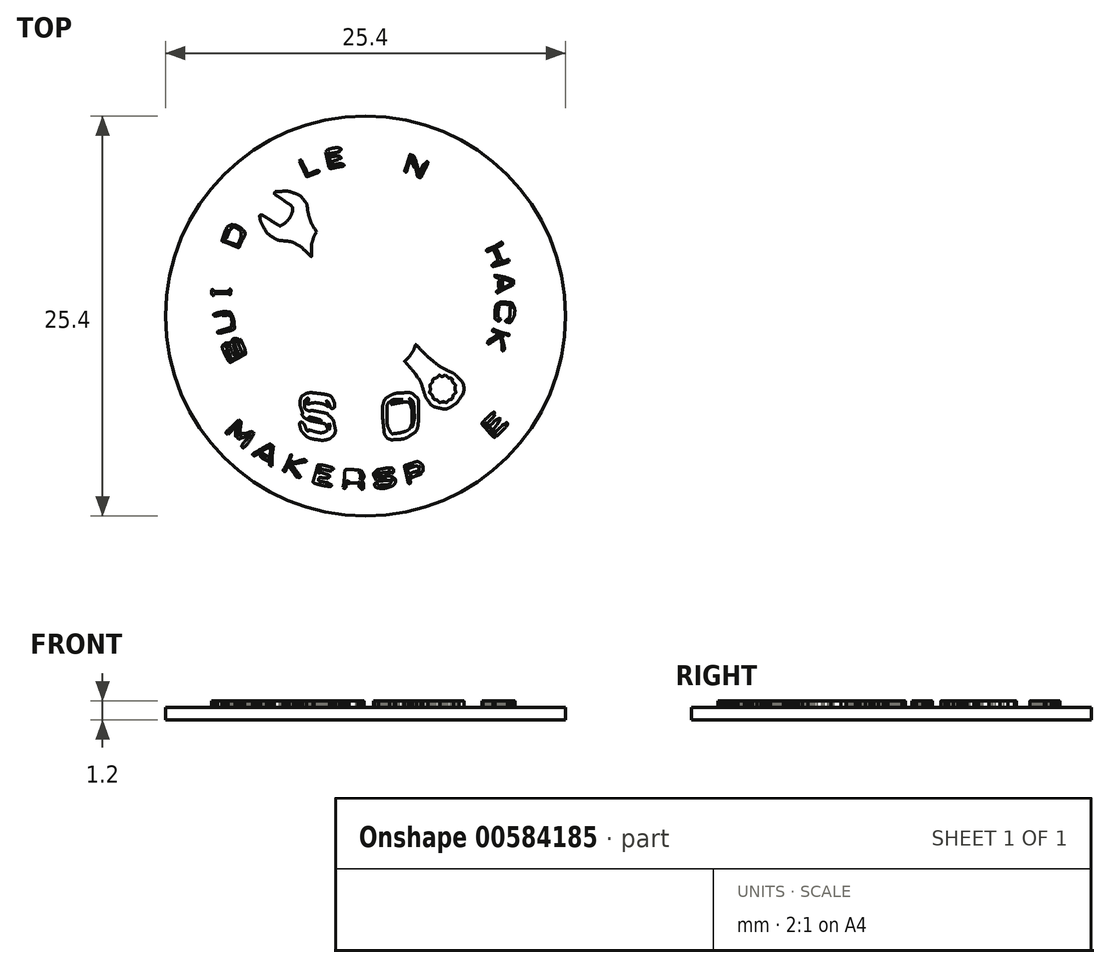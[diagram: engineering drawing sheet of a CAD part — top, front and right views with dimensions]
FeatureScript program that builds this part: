
annotation { "Feature Type Name" : "Feature", "Feature Type Description" : "" }
export const myFeature = defineFeature(function(context is Context, id is Id, definition is map)
    precondition{}
    {
        {
            var Q0;
            Q0=qCreatedBy(makeId("Top.planeOp"),FACE);
            var sketch = newSketch(context, id + "F0", { "sketchPlane" : qUnion([Q0])});
            skCircle(sketch, "E0", {"center": v(0, 0) * mm, "radius": 12.7 * mm});
            skSolve(sketch);
        }
        {
            var Q0;
            Q0=makeQuery(id+"F0.imprint","IMPRINT",FACE,{"disambiguationData":[TD([[makeQuery(id+"F0.imprint","IMPRINT",EDGE,{"derivedFrom":sQuery(id+"F0.wireOp",EDGE,"E0")}),1.0]])]});
            extrude(context, id + "F1", {"entities" : qUnion([Q0]), "depth" : .8 * mm, "offsetDistance" : 25.4 * mm});
        }
        {
            var Q0;
            Q0=makeQuery(id+"F1.opExtrude","CAP_FACE",FACE,{"disambiguationData":[OSD([sQuery(id+"F0.wireOp",EDGE,"E0")])],"isStart":false});
            var sketch = newSketch(context, id + "F2", { "sketchPlane" : qUnion([Q0])});
            skFitSpline(sketch, "E1", {"points": [v(-0.28, -10.95) * mm, v(-0.3, -10.92) * mm, v(-0.3, -10.87) * mm, v(-0.3, -10.8) * mm]});
            skFitSpline(sketch, "E2", {"points": [v(-0.3, -10.8) * mm, v(-0.28, -10.68) * mm, v(-0.3, -10.63) * mm, v(-0.35, -10.58) * mm]});
            skFitSpline(sketch, "E3", {"points": [v(-0.35, -10.58) * mm, v(-0.4, -10.53) * mm, v(-0.42, -10.54) * mm, v(-0.38, -10.6) * mm]});
            skFitSpline(sketch, "E4", {"points": [v(-0.38, -10.6) * mm, v(-0.36, -10.63) * mm, v(-0.35, -10.67) * mm, v(-0.35, -10.76) * mm]});
            skFitSpline(sketch, "E5", {"points": [v(-0.35, -10.76) * mm, v(-0.35, -10.82) * mm, v(-0.36, -10.87) * mm, v(-0.36, -10.87) * mm]});
            skFitSpline(sketch, "E6", {"points": [v(-0.36, -10.87) * mm, v(-0.38, -10.88) * mm, v(-0.41, -10.8) * mm, v(-0.41, -10.76) * mm]});
            skFitSpline(sketch, "E7", {"points": [v(-0.41, -10.76) * mm, v(-0.41, -10.7) * mm, v(-0.44, -10.66) * mm, v(-0.49, -10.64) * mm]});
            skFitSpline(sketch, "E8", {"points": [v(-0.49, -10.64) * mm, v(-0.54, -10.62) * mm, v(-0.96, -10.61) * mm, v(-1.05, -10.63) * mm]});
            skFitSpline(sketch, "E9", {"points": [v(-1.05, -10.63) * mm, v(-1.12, -10.64) * mm, v(-1.13, -10.62) * mm, v(-1.08, -10.57) * mm]});
            skFitSpline(sketch, "E10", {"points": [v(-1.08, -10.57) * mm, v(-1.04, -10.53) * mm, v(-1.04, -10.5) * mm, v(-1.08, -10.5) * mm]});
            skFitSpline(sketch, "E11", {"points": [v(-1.08, -10.5) * mm, v(-1.2, -10.47) * mm, v(-1.22, -10.5) * mm, v(-1.23, -10.7) * mm]});
            skFitSpline(sketch, "E12", {"points": [v(-1.23, -10.7) * mm, v(-1.24, -10.84) * mm, v(-1.24, -10.87) * mm, v(-1.27, -10.9) * mm]});
            skFitSpline(sketch, "E13", {"points": [v(-1.27, -10.9) * mm, v(-1.31, -10.96) * mm, v(-1.35, -10.97) * mm, v(-1.4, -10.92) * mm]});
            skLineSegment(sketch, "E14", {"start": v(-1.4, -10.92) * mm, "end": v(-1.43, -10.89) * mm});
            skLineSegment(sketch, "E15", {"start": v(-1.43, -10.89) * mm, "end": v(-1.4, -10.75) * mm});
            skFitSpline(sketch, "E16", {"points": [v(-1.4, -10.75) * mm, v(-1.38, -10.67) * mm, v(-1.36, -10.44) * mm, v(-1.35, -10.25) * mm]});
            skFitSpline(sketch, "E17", {"points": [v(-1.35, -10.25) * mm, v(-1.32, -9.83) * mm, v(-1.31, -9.8) * mm, v(-1.28, -9.77) * mm]});
            skFitSpline(sketch, "E18", {"points": [v(-1.28, -9.77) * mm, v(-1.24, -9.75) * mm, v(-0.81, -9.76) * mm, v(-0.62, -9.77) * mm]});
            skFitSpline(sketch, "E19", {"points": [v(-0.62, -9.77) * mm, v(-0.36, -9.8) * mm, v(-0.23, -9.86) * mm, v(-0.17, -10) * mm]});
            skFitSpline(sketch, "E20", {"points": [v(-0.17, -10) * mm, v(-0.12, -10.1) * mm, v(-0.1, -10.25) * mm, v(-0.15, -10.33) * mm]});
            skFitSpline(sketch, "E21", {"points": [v(-0.15, -10.33) * mm, v(-0.17, -10.36) * mm, v(-0.2, -10.4) * mm, v(-0.2, -10.4) * mm]});
            skFitSpline(sketch, "E22", {"points": [v(-0.2, -10.4) * mm, v(-0.22, -10.43) * mm, v(-0.22, -10.44) * mm, v(-0.18, -10.52) * mm]});
            skFitSpline(sketch, "E23", {"points": [v(-0.18, -10.52) * mm, v(-0.13, -10.61) * mm, v(-0.13, -10.62) * mm, v(-0.13, -10.8) * mm]});
            skFitSpline(sketch, "E24", {"points": [v(-0.13, -10.8) * mm, v(-0.14, -10.9) * mm, v(-0.14, -10.98) * mm, v(-0.14, -10.98) * mm]});
            skFitSpline(sketch, "E25", {"points": [v(-0.14, -10.98) * mm, v(-0.14, -10.98) * mm, v(-0.17, -11) * mm, v(-0.2, -11) * mm]});
            skFitSpline(sketch, "E26", {"points": [v(-0.2, -11) * mm, v(-0.26, -11) * mm, v(-0.26, -11) * mm, v(-0.28, -10.95) * mm]});
            skLineSegment(sketch, "E27", {"start": v(-0.28, -10.95) * mm, "end": v(-0.28, -10.95) * mm});
            skFitSpline(sketch, "E28", {"points": [v(-1.09, -10.33) * mm, v(-1.02, -10.3) * mm, v(-0.88, -10.3) * mm, v(-0.71, -10.33) * mm]});
            skFitSpline(sketch, "E29", {"points": [v(-0.71, -10.33) * mm, v(-0.45, -10.38) * mm, v(-0.4, -10.36) * mm, v(-0.4, -10.2) * mm]});
            skLineSegment(sketch, "E30", {"start": v(-0.4, -10.2) * mm, "end": v(-0.4, -10.1) * mm});
            skLineSegment(sketch, "E31", {"start": v(-0.4, -10.1) * mm, "end": v(-0.47, -10.07) * mm});
            skFitSpline(sketch, "E32", {"points": [v(-0.47, -10.07) * mm, v(-0.53, -10.04) * mm, v(-0.57, -10.04) * mm, v(-0.8, -10.03) * mm]});
            skLineSegment(sketch, "E33", {"start": v(-0.8, -10.03) * mm, "end": v(-1.08, -10.03) * mm});
            skLineSegment(sketch, "E34", {"start": v(-1.08, -10.03) * mm, "end": v(-1.08, -9.97) * mm});
            skFitSpline(sketch, "E35", {"points": [v(-1.08, -9.97) * mm, v(-1.08, -9.94) * mm, v(-1.1, -9.92) * mm, v(-1.1, -9.92) * mm]});
            skFitSpline(sketch, "E36", {"points": [v(-1.1, -9.92) * mm, v(-1.13, -9.92) * mm, v(-1.14, -9.95) * mm, v(-1.16, -10.05) * mm]});
            skFitSpline(sketch, "E37", {"points": [v(-1.16, -10.05) * mm, v(-1.2, -10.3) * mm, v(-1.2, -10.3) * mm, v(-1.18, -10.33) * mm]});
            skFitSpline(sketch, "E38", {"points": [v(-1.18, -10.33) * mm, v(-1.15, -10.36) * mm, v(-1.16, -10.36) * mm, v(-1.09, -10.33) * mm]});
            skLineSegment(sketch, "E39", {"start": v(-1.09, -10.33) * mm, "end": v(-1.09, -10.33) * mm});
            skFitSpline(sketch, "E40", {"points": [v(-0.3, -10.28) * mm, v(-0.27, -10.2) * mm, v(-0.3, -10.06) * mm, v(-0.34, -10) * mm]});
            skFitSpline(sketch, "E41", {"points": [v(-0.34, -10) * mm, v(-0.4, -9.94) * mm, v(-0.42, -9.94) * mm, v(-0.38, -10) * mm]});
            skFitSpline(sketch, "E42", {"points": [v(-0.38, -10) * mm, v(-0.32, -10.08) * mm, v(-0.31, -10.23) * mm, v(-0.35, -10.3) * mm]});
            skFitSpline(sketch, "E43", {"points": [v(-0.35, -10.3) * mm, v(-0.36, -10.33) * mm, v(-0.36, -10.34) * mm, v(-0.35, -10.34) * mm]});
            skFitSpline(sketch, "E44", {"points": [v(-0.35, -10.34) * mm, v(-0.34, -10.34) * mm, v(-0.32, -10.31) * mm, v(-0.3, -10.28) * mm]});
            skFitSpline(sketch, "E45", {"points": [v(1.08, -11) * mm, v(1.08, -11) * mm, v(1.15, -10.99) * mm, v(1.22, -10.98) * mm]});
            skFitSpline(sketch, "E46", {"points": [v(1.22, -10.98) * mm, v(1.31, -10.98) * mm, v(1.34, -10.98) * mm, v(1.3, -10.99) * mm]});
            skFitSpline(sketch, "E47", {"points": [v(1.3, -10.99) * mm, v(1.24, -11) * mm, v(1.07, -11) * mm, v(1.08, -11) * mm]});
            skFitSpline(sketch, "E48", {"points": [v(0.84, -10.93) * mm, v(0.7, -10.9) * mm, v(0.6, -10.82) * mm, v(0.58, -10.72) * mm]});
            skFitSpline(sketch, "E49", {"points": [v(0.58, -10.72) * mm, v(0.57, -10.67) * mm, v(0.6, -10.63) * mm, v(0.66, -10.62) * mm]});
            skFitSpline(sketch, "E50", {"points": [v(0.66, -10.62) * mm, v(0.7, -10.6) * mm, v(0.7, -10.61) * mm, v(0.78, -10.7) * mm]});
            skFitSpline(sketch, "E51", {"points": [v(0.78, -10.7) * mm, v(0.86, -10.78) * mm, v(0.88, -10.8) * mm, v(0.93, -10.75) * mm]});
            skFitSpline(sketch, "E52", {"points": [v(0.93, -10.75) * mm, v(0.95, -10.74) * mm, v(1, -10.73) * mm, v(1.08, -10.73) * mm]});
            skFitSpline(sketch, "E53", {"points": [v(1.08, -10.73) * mm, v(1.3, -10.73) * mm, v(1.57, -10.65) * mm, v(1.6, -10.58) * mm]});
            skFitSpline(sketch, "E54", {"points": [v(1.6, -10.58) * mm, v(1.63, -10.55) * mm, v(1.6, -10.49) * mm, v(1.55, -10.46) * mm]});
            skFitSpline(sketch, "E55", {"points": [v(1.55, -10.46) * mm, v(1.5, -10.44) * mm, v(1.5, -10.44) * mm, v(1, -10.47) * mm]});
            skFitSpline(sketch, "E56", {"points": [v(1, -10.47) * mm, v(0.83, -10.48) * mm, v(0.76, -10.46) * mm, v(0.67, -10.41) * mm]});
            skFitSpline(sketch, "E57", {"points": [v(0.67, -10.41) * mm, v(0.63, -10.39) * mm, v(0.62, -10.38) * mm, v(0.64, -10.37) * mm]});
            skFitSpline(sketch, "E58", {"points": [v(0.64, -10.37) * mm, v(0.66, -10.35) * mm, v(0.66, -10.35) * mm, v(0.64, -10.32) * mm]});
            skFitSpline(sketch, "E59", {"points": [v(0.64, -10.32) * mm, v(0.52, -10.13) * mm, v(0.52, -10) * mm, v(0.63, -9.86) * mm]});
            skFitSpline(sketch, "E60", {"points": [v(0.63, -9.86) * mm, v(0.7, -9.8) * mm, v(0.79, -9.76) * mm, v(0.99, -9.72) * mm]});
            skFitSpline(sketch, "E61", {"points": [v(0.99, -9.72) * mm, v(1.47, -9.64) * mm, v(1.75, -9.7) * mm, v(1.76, -9.89) * mm]});
            skFitSpline(sketch, "E62", {"points": [v(1.76, -9.89) * mm, v(1.77, -9.92) * mm, v(1.76, -9.94) * mm, v(1.72, -9.96) * mm]});
            skLineSegment(sketch, "E63", {"start": v(1.72, -9.96) * mm, "end": v(1.67, -10) * mm});
            skLineSegment(sketch, "E64", {"start": v(1.67, -10) * mm, "end": v(1.6, -9.91) * mm});
            skFitSpline(sketch, "E65", {"points": [v(1.6, -9.91) * mm, v(1.56, -9.87) * mm, v(1.51, -9.83) * mm, v(1.5, -9.83) * mm]});
            skFitSpline(sketch, "E66", {"points": [v(1.5, -9.83) * mm, v(1.47, -9.83) * mm, v(1.47, -9.84) * mm, v(1.5, -9.88) * mm]});
            skFitSpline(sketch, "E67", {"points": [v(1.5, -9.88) * mm, v(1.51, -9.9) * mm, v(1.53, -9.93) * mm, v(1.54, -9.93) * mm]});
            skFitSpline(sketch, "E68", {"points": [v(1.54, -9.93) * mm, v(1.54, -9.94) * mm, v(1.47, -9.95) * mm, v(1.32, -9.95) * mm]});
            skFitSpline(sketch, "E69", {"points": [v(1.32, -9.95) * mm, v(1.11, -9.95) * mm, v(1.1, -9.95) * mm, v(0.96, -10) * mm]});
            skFitSpline(sketch, "E70", {"points": [v(0.96, -10) * mm, v(0.88, -10.03) * mm, v(0.81, -10.05) * mm, v(0.81, -10.05) * mm]});
            skFitSpline(sketch, "E71", {"points": [v(0.81, -10.05) * mm, v(0.8, -10.05) * mm, v(0.81, -10.02) * mm, v(0.82, -9.99) * mm]});
            skFitSpline(sketch, "E72", {"points": [v(0.82, -9.99) * mm, v(0.84, -9.89) * mm, v(0.81, -9.87) * mm, v(0.74, -9.94) * mm]});
            skFitSpline(sketch, "E73", {"points": [v(0.74, -9.94) * mm, v(0.69, -10) * mm, v(0.68, -10.07) * mm, v(0.72, -10.15) * mm]});
            skFitSpline(sketch, "E74", {"points": [v(0.72, -10.15) * mm, v(0.76, -10.22) * mm, v(0.84, -10.25) * mm, v(0.91, -10.22) * mm]});
            skFitSpline(sketch, "E75", {"points": [v(0.91, -10.22) * mm, v(0.94, -10.2) * mm, v(1.09, -10.19) * mm, v(1.24, -10.17) * mm]});
            skLineSegment(sketch, "E76", {"start": v(1.24, -10.17) * mm, "end": v(1.51, -10.15) * mm});
            skLineSegment(sketch, "E77", {"start": v(1.51, -10.15) * mm, "end": v(1.62, -10.2) * mm});
            skFitSpline(sketch, "E78", {"points": [v(1.62, -10.2) * mm, v(1.68, -10.21) * mm, v(1.75, -10.25) * mm, v(1.78, -10.27) * mm]});
            skFitSpline(sketch, "E79", {"points": [v(1.78, -10.27) * mm, v(1.87, -10.35) * mm, v(1.91, -10.53) * mm, v(1.85, -10.64) * mm]});
            skFitSpline(sketch, "E80", {"points": [v(1.85, -10.64) * mm, v(1.81, -10.71) * mm, v(1.66, -10.81) * mm, v(1.52, -10.86) * mm]});
            skFitSpline(sketch, "E81", {"points": [v(1.52, -10.86) * mm, v(1.3, -10.93) * mm, v(1, -10.96) * mm, v(0.84, -10.93) * mm]});
            skFitSpline(sketch, "E82", {"points": [v(1.68, -10.4) * mm, v(1.64, -10.37) * mm, v(1.63, -10.38) * mm, v(1.66, -10.43) * mm]});
            skFitSpline(sketch, "E83", {"points": [v(1.66, -10.43) * mm, v(1.68, -10.45) * mm, v(1.7, -10.46) * mm, v(1.7, -10.44) * mm]});
            skFitSpline(sketch, "E84", {"points": [v(1.7, -10.44) * mm, v(1.7, -10.43) * mm, v(1.7, -10.41) * mm, v(1.68, -10.4) * mm]});
            skFitSpline(sketch, "E85", {"points": [v(1.29, -10.38) * mm, v(1.33, -10.37) * mm, v(1.29, -10.37) * mm, v(1.16, -10.38) * mm]});
            skFitSpline(sketch, "E86", {"points": [v(1.16, -10.38) * mm, v(1.07, -10.38) * mm, v(0.97, -10.39) * mm, v(0.94, -10.4) * mm]});
            skFitSpline(sketch, "E87", {"points": [v(0.94, -10.4) * mm, v(0.89, -10.42) * mm, v(1.22, -10.4) * mm, v(1.29, -10.38) * mm]});
            skFitSpline(sketch, "E88", {"points": [v(-2.66, -10.83) * mm, v(-2.82, -10.8) * mm, v(-2.98, -10.76) * mm, v(-2.97, -10.75) * mm]});
            skFitSpline(sketch, "E89", {"points": [v(-2.97, -10.75) * mm, v(-2.97, -10.75) * mm, v(-2.88, -10.77) * mm, v(-2.76, -10.8) * mm]});
            skFitSpline(sketch, "E90", {"points": [v(-2.76, -10.8) * mm, v(-2.65, -10.81) * mm, v(-2.58, -10.83) * mm, v(-2.6, -10.83) * mm]});
            skFitSpline(sketch, "E91", {"points": [v(-2.6, -10.83) * mm, v(-2.62, -10.83) * mm, v(-2.65, -10.83) * mm, v(-2.66, -10.83) * mm]});
            skFitSpline(sketch, "E92", {"points": [v(-2.29, -10.83) * mm, v(-2.48, -10.8) * mm, v(-3.25, -10.63) * mm, v(-3.29, -10.6) * mm]});
            skFitSpline(sketch, "E93", {"points": [v(-3.29, -10.6) * mm, v(-3.33, -10.56) * mm, v(-3.31, -10.43) * mm, v(-3.21, -10.1) * mm]});
            skFitSpline(sketch, "E94", {"points": [v(-3.21, -10.1) * mm, v(-3.17, -9.95) * mm, v(-3.1, -9.75) * mm, v(-3.09, -9.66) * mm]});
            skFitSpline(sketch, "E95", {"points": [v(-3.09, -9.66) * mm, v(-3.04, -9.47) * mm, v(-3.02, -9.46) * mm, v(-2.9, -9.46) * mm]});
            skFitSpline(sketch, "E96", {"points": [v(-2.9, -9.46) * mm, v(-2.84, -9.46) * mm, v(-2.48, -9.53) * mm, v(-2.3, -9.58) * mm]});
            skFitSpline(sketch, "E97", {"points": [v(-2.3, -9.58) * mm, v(-2.17, -9.61) * mm, v(-2.04, -9.68) * mm, v(-2.04, -9.7) * mm]});
            skFitSpline(sketch, "E98", {"points": [v(-2.04, -9.7) * mm, v(-2.04, -9.74) * mm, v(-2.07, -9.76) * mm, v(-2.13, -9.76) * mm]});
            skFitSpline(sketch, "E99", {"points": [v(-2.13, -9.76) * mm, v(-2.19, -9.76) * mm, v(-2.19, -9.76) * mm, v(-2.18, -9.8) * mm]});
            skFitSpline(sketch, "E100", {"points": [v(-2.18, -9.8) * mm, v(-2.17, -9.83) * mm, v(-2.17, -9.83) * mm, v(-2.23, -9.83) * mm]});
            skFitSpline(sketch, "E101", {"points": [v(-2.23, -9.83) * mm, v(-2.26, -9.83) * mm, v(-2.4, -9.81) * mm, v(-2.55, -9.78) * mm]});
            skLineSegment(sketch, "E102", {"start": v(-2.55, -9.78) * mm, "end": v(-2.82, -9.73) * mm});
            skLineSegment(sketch, "E103", {"start": v(-2.82, -9.73) * mm, "end": v(-2.84, -9.76) * mm});
            skFitSpline(sketch, "E104", {"points": [v(-2.84, -9.76) * mm, v(-2.86, -9.78) * mm, v(-2.87, -9.81) * mm, v(-2.87, -9.84) * mm]});
            skFitSpline(sketch, "E105", {"points": [v(-2.87, -9.84) * mm, v(-2.87, -9.86) * mm, v(-2.88, -9.88) * mm, v(-2.89, -9.89) * mm]});
            skFitSpline(sketch, "E106", {"points": [v(-2.89, -9.89) * mm, v(-2.9, -9.9) * mm, v(-2.9, -9.8) * mm, v(-2.86, -9.7) * mm]});
            skFitSpline(sketch, "E107", {"points": [v(-2.86, -9.7) * mm, v(-2.85, -9.66) * mm, v(-2.84, -9.63) * mm, v(-2.84, -9.63) * mm]});
            skFitSpline(sketch, "E108", {"points": [v(-2.84, -9.63) * mm, v(-2.85, -9.62) * mm, v(-2.86, -9.63) * mm, v(-2.88, -9.65) * mm]});
            skFitSpline(sketch, "E109", {"points": [v(-2.88, -9.65) * mm, v(-2.92, -9.68) * mm, v(-2.97, -9.76) * mm, v(-3, -9.86) * mm]});
            skFitSpline(sketch, "E110", {"points": [v(-3, -9.86) * mm, v(-3, -9.92) * mm, v(-3, -9.93) * mm, v(-2.98, -9.95) * mm]});
            skFitSpline(sketch, "E111", {"points": [v(-2.98, -9.95) * mm, v(-2.94, -9.98) * mm, v(-2.88, -9.98) * mm, v(-2.88, -9.95) * mm]});
            skFitSpline(sketch, "E112", {"points": [v(-2.88, -9.95) * mm, v(-2.88, -9.94) * mm, v(-2.88, -9.93) * mm, v(-2.87, -9.93) * mm]});
            skFitSpline(sketch, "E113", {"points": [v(-2.87, -9.93) * mm, v(-2.87, -9.93) * mm, v(-2.76, -9.96) * mm, v(-2.64, -10) * mm]});
            skFitSpline(sketch, "E114", {"points": [v(-2.64, -10) * mm, v(-2.4, -10.08) * mm, v(-2.3, -10.13) * mm, v(-2.3, -10.2) * mm]});
            skFitSpline(sketch, "E115", {"points": [v(-2.3, -10.2) * mm, v(-2.3, -10.25) * mm, v(-2.3, -10.25) * mm, v(-2.37, -10.26) * mm]});
            skFitSpline(sketch, "E116", {"points": [v(-2.37, -10.26) * mm, v(-2.44, -10.26) * mm, v(-2.44, -10.26) * mm, v(-2.43, -10.28) * mm]});
            skFitSpline(sketch, "E117", {"points": [v(-2.43, -10.28) * mm, v(-2.4, -10.3) * mm, v(-2.41, -10.3) * mm, v(-2.72, -10.27) * mm]});
            skFitSpline(sketch, "E118", {"points": [v(-2.72, -10.27) * mm, v(-2.92, -10.25) * mm, v(-2.92, -10.25) * mm, v(-2.96, -10.31) * mm]});
            skFitSpline(sketch, "E119", {"points": [v(-2.96, -10.31) * mm, v(-2.98, -10.34) * mm, v(-3, -10.38) * mm, v(-2.99, -10.4) * mm]});
            skFitSpline(sketch, "E120", {"points": [v(-2.99, -10.4) * mm, v(-2.98, -10.46) * mm, v(-2.9, -10.5) * mm, v(-2.59, -10.56) * mm]});
            skFitSpline(sketch, "E121", {"points": [v(-2.59, -10.56) * mm, v(-2.4, -10.6) * mm, v(-2.35, -10.6) * mm, v(-2.38, -10.62) * mm]});
            skFitSpline(sketch, "E122", {"points": [v(-2.38, -10.62) * mm, v(-2.41, -10.63) * mm, v(-2.4, -10.64) * mm, v(-2.33, -10.66) * mm]});
            skFitSpline(sketch, "E123", {"points": [v(-2.33, -10.66) * mm, v(-2.22, -10.7) * mm, v(-2.17, -10.73) * mm, v(-2.17, -10.78) * mm]});
            skFitSpline(sketch, "E124", {"points": [v(-2.17, -10.78) * mm, v(-2.18, -10.82) * mm, v(-2.22, -10.83) * mm, v(-2.29, -10.83) * mm]});
            skFitSpline(sketch, "E125", {"points": [v(-3, -10.33) * mm, v(-2.95, -10.14) * mm, v(-2.95, -10.14) * mm, v(-3, -10.14) * mm]});
            skFitSpline(sketch, "E126", {"points": [v(-3, -10.14) * mm, v(-3.02, -10.14) * mm, v(-3.04, -10.15) * mm, v(-3.05, -10.16) * mm]});
            skFitSpline(sketch, "E127", {"points": [v(-3.05, -10.16) * mm, v(-3.07, -10.19) * mm, v(-3.11, -10.34) * mm, v(-3.11, -10.4) * mm]});
            skFitSpline(sketch, "E128", {"points": [v(-3.11, -10.4) * mm, v(-3.11, -10.45) * mm, v(-3.07, -10.5) * mm, v(-3.05, -10.5) * mm]});
            skFitSpline(sketch, "E129", {"points": [v(-3.05, -10.5) * mm, v(-3.04, -10.5) * mm, v(-3.02, -10.42) * mm, v(-3, -10.33) * mm]});
            skFitSpline(sketch, "E130", {"points": [v(2.77, -10.64) * mm, v(2.75, -10.64) * mm, v(2.73, -10.63) * mm, v(2.73, -10.63) * mm]});
            skFitSpline(sketch, "E131", {"points": [v(2.73, -10.63) * mm, v(2.72, -10.62) * mm, v(2.66, -10.38) * mm, v(2.6, -10.1) * mm]});
            skFitSpline(sketch, "E132", {"points": [v(2.6, -10.1) * mm, v(2.53, -9.82) * mm, v(2.47, -9.57) * mm, v(2.47, -9.56) * mm]});
            skFitSpline(sketch, "E133", {"points": [v(2.47, -9.56) * mm, v(2.46, -9.52) * mm, v(2.58, -9.46) * mm, v(2.84, -9.38) * mm]});
            skFitSpline(sketch, "E134", {"points": [v(2.84, -9.38) * mm, v(3.17, -9.27) * mm, v(3.34, -9.25) * mm, v(3.46, -9.32) * mm]});
            skFitSpline(sketch, "E135", {"points": [v(3.46, -9.32) * mm, v(3.56, -9.38) * mm, v(3.66, -9.6) * mm, v(3.66, -9.76) * mm]});
            skFitSpline(sketch, "E136", {"points": [v(3.66, -9.76) * mm, v(3.66, -9.85) * mm, v(3.63, -9.88) * mm, v(3.49, -9.94) * mm]});
            skFitSpline(sketch, "E137", {"points": [v(3.49, -9.94) * mm, v(3.32, -10) * mm, v(3.24, -10.05) * mm, v(3.26, -10.07) * mm]});
            skFitSpline(sketch, "E138", {"points": [v(3.26, -10.07) * mm, v(3.27, -10.08) * mm, v(3.3, -10.07) * mm, v(3.4, -10.05) * mm]});
            skFitSpline(sketch, "E139", {"points": [v(3.4, -10.05) * mm, v(3.46, -10.03) * mm, v(3.51, -10.02) * mm, v(3.52, -10.02) * mm]});
            skFitSpline(sketch, "E140", {"points": [v(3.52, -10.02) * mm, v(3.53, -10.04) * mm, v(3.41, -10.08) * mm, v(3.23, -10.15) * mm]});
            skFitSpline(sketch, "E141", {"points": [v(3.23, -10.15) * mm, v(3.13, -10.19) * mm, v(3.02, -10.23) * mm, v(3, -10.25) * mm]});
            skFitSpline(sketch, "E142", {"points": [v(3, -10.25) * mm, v(2.93, -10.28) * mm, v(2.9, -10.27) * mm, v(2.92, -10.2) * mm]});
            skFitSpline(sketch, "E143", {"points": [v(2.92, -10.2) * mm, v(2.93, -10.16) * mm, v(2.93, -10.15) * mm, v(2.88, -10.15) * mm]});
            skFitSpline(sketch, "E144", {"points": [v(2.88, -10.15) * mm, v(2.82, -10.15) * mm, v(2.8, -10.21) * mm, v(2.83, -10.42) * mm]});
            skFitSpline(sketch, "E145", {"points": [v(2.83, -10.42) * mm, v(2.85, -10.54) * mm, v(2.85, -10.6) * mm, v(2.84, -10.62) * mm]});
            skFitSpline(sketch, "E146", {"points": [v(2.84, -10.62) * mm, v(2.83, -10.64) * mm, v(2.82, -10.65) * mm, v(2.81, -10.65) * mm]});
            skFitSpline(sketch, "E147", {"points": [v(2.81, -10.65) * mm, v(2.8, -10.65) * mm, v(2.79, -10.65) * mm, v(2.77, -10.64) * mm]});
            skFitSpline(sketch, "E148", {"points": [v(2.88, -9.98) * mm, v(2.92, -9.96) * mm, v(3.02, -9.93) * mm, v(3.1, -9.9) * mm]});
            skFitSpline(sketch, "E149", {"points": [v(3.1, -9.9) * mm, v(3.25, -9.86) * mm, v(3.33, -9.82) * mm, v(3.37, -9.78) * mm]});
            skFitSpline(sketch, "E150", {"points": [v(3.37, -9.78) * mm, v(3.4, -9.75) * mm, v(3.4, -9.74) * mm, v(3.38, -9.68) * mm]});
            skFitSpline(sketch, "E151", {"points": [v(3.38, -9.68) * mm, v(3.37, -9.64) * mm, v(3.35, -9.6) * mm, v(3.33, -9.57) * mm]});
            skFitSpline(sketch, "E152", {"points": [v(3.33, -9.57) * mm, v(3.3, -9.53) * mm, v(3.3, -9.53) * mm, v(3.23, -9.54) * mm]});
            skFitSpline(sketch, "E153", {"points": [v(3.23, -9.54) * mm, v(3.15, -9.54) * mm, v(2.98, -9.6) * mm, v(2.84, -9.65) * mm]});
            skLineSegment(sketch, "E154", {"start": v(2.84, -9.65) * mm, "end": v(2.76, -9.68) * mm});
            skLineSegment(sketch, "E155", {"start": v(2.76, -9.68) * mm, "end": v(2.73, -9.63) * mm});
            skFitSpline(sketch, "E156", {"points": [v(2.73, -9.63) * mm, v(2.7, -9.57) * mm, v(2.63, -9.55) * mm, v(2.64, -9.6) * mm]});
            skFitSpline(sketch, "E157", {"points": [v(2.64, -9.6) * mm, v(2.65, -9.62) * mm, v(2.66, -9.68) * mm, v(2.67, -9.74) * mm]});
            skFitSpline(sketch, "E158", {"points": [v(2.67, -9.74) * mm, v(2.7, -9.89) * mm, v(2.71, -9.97) * mm, v(2.73, -10) * mm]});
            skFitSpline(sketch, "E159", {"points": [v(2.73, -10) * mm, v(2.76, -10.03) * mm, v(2.8, -10.02) * mm, v(2.88, -9.98) * mm]});
            skFitSpline(sketch, "E160", {"points": [v(3.45, -9.58) * mm, v(3.43, -9.55) * mm, v(3.42, -9.56) * mm, v(3.44, -9.6) * mm]});
            skFitSpline(sketch, "E161", {"points": [v(3.44, -9.6) * mm, v(3.44, -9.61) * mm, v(3.45, -9.62) * mm, v(3.45, -9.62) * mm]});
            skFitSpline(sketch, "E162", {"points": [v(3.45, -9.62) * mm, v(3.46, -9.61) * mm, v(3.45, -9.6) * mm, v(3.45, -9.58) * mm]});
            skFitSpline(sketch, "E163", {"points": [v(2.99, -9.51) * mm, v(3.06, -9.5) * mm, v(3.07, -9.46) * mm, v(3, -9.48) * mm]});
            skFitSpline(sketch, "E164", {"points": [v(3, -9.48) * mm, v(2.96, -9.5) * mm, v(2.88, -9.53) * mm, v(2.88, -9.54) * mm]});
            skFitSpline(sketch, "E165", {"points": [v(2.88, -9.54) * mm, v(2.88, -9.55) * mm, v(2.9, -9.55) * mm, v(2.9, -9.54) * mm]});
            skFitSpline(sketch, "E166", {"points": [v(2.9, -9.54) * mm, v(2.92, -9.54) * mm, v(2.95, -9.53) * mm, v(2.99, -9.51) * mm]});
            skLineSegment(sketch, "E167", {"start": v(2.99, -9.51) * mm, "end": v(2.99, -9.51) * mm});
            skFitSpline(sketch, "E168", {"points": [v(-4.3, -10.23) * mm, v(-4.34, -10.21) * mm, v(-4.37, -10.2) * mm, v(-4.37, -10.22) * mm]});
            skFitSpline(sketch, "E169", {"points": [v(-4.37, -10.22) * mm, v(-4.38, -10.23) * mm, v(-4.44, -10.15) * mm, v(-4.58, -9.94) * mm]});
            skFitSpline(sketch, "E170", {"points": [v(-4.58, -9.94) * mm, v(-4.64, -9.86) * mm, v(-4.72, -9.74) * mm, v(-4.77, -9.7) * mm]});
            skFitSpline(sketch, "E171", {"points": [v(-4.77, -9.7) * mm, v(-4.84, -9.63) * mm, v(-4.86, -9.6) * mm, v(-4.85, -9.58) * mm]});
            skFitSpline(sketch, "E172", {"points": [v(-4.85, -9.58) * mm, v(-4.84, -9.53) * mm, v(-4.82, -9.54) * mm, v(-4.77, -9.63) * mm]});
            skFitSpline(sketch, "E173", {"points": [v(-4.77, -9.63) * mm, v(-4.7, -9.72) * mm, v(-4.45, -10.08) * mm, v(-4.4, -10.14) * mm]});
            skLineSegment(sketch, "E174", {"start": v(-4.4, -10.14) * mm, "end": v(-4.37, -10.18) * mm});
            skLineSegment(sketch, "E175", {"start": v(-4.37, -10.18) * mm, "end": v(-4.4, -10.12) * mm});
            skFitSpline(sketch, "E176", {"points": [v(-4.4, -10.12) * mm, v(-4.42, -10.08) * mm, v(-4.52, -9.9) * mm, v(-4.63, -9.72) * mm]});
            skFitSpline(sketch, "E177", {"points": [v(-4.63, -9.72) * mm, v(-4.82, -9.41) * mm, v(-4.84, -9.39) * mm, v(-4.88, -9.39) * mm]});
            skFitSpline(sketch, "E178", {"points": [v(-4.88, -9.39) * mm, v(-4.92, -9.39) * mm, v(-4.93, -9.4) * mm, v(-5, -9.61) * mm]});
            skFitSpline(sketch, "E179", {"points": [v(-5, -9.61) * mm, v(-5.04, -9.74) * mm, v(-5.08, -9.85) * mm, v(-5.1, -9.86) * mm]});
            skFitSpline(sketch, "E180", {"points": [v(-5.1, -9.86) * mm, v(-5.12, -9.89) * mm, v(-5.19, -9.87) * mm, v(-5.22, -9.83) * mm]});
            skFitSpline(sketch, "E181", {"points": [v(-5.22, -9.83) * mm, v(-5.23, -9.8) * mm, v(-5.23, -9.78) * mm, v(-5.17, -9.68) * mm]});
            skFitSpline(sketch, "E182", {"points": [v(-5.17, -9.68) * mm, v(-5.06, -9.52) * mm, v(-4.92, -9.22) * mm, v(-4.83, -9) * mm]});
            skFitSpline(sketch, "E183", {"points": [v(-4.83, -9) * mm, v(-4.77, -8.84) * mm, v(-4.76, -8.82) * mm, v(-4.73, -8.82) * mm]});
            skFitSpline(sketch, "E184", {"points": [v(-4.73, -8.82) * mm, v(-4.69, -8.83) * mm, v(-4.7, -8.87) * mm, v(-4.78, -9.03) * mm]});
            skFitSpline(sketch, "E185", {"points": [v(-4.78, -9.03) * mm, v(-4.85, -9.18) * mm, v(-4.86, -9.25) * mm, v(-4.81, -9.3) * mm]});
            skFitSpline(sketch, "E186", {"points": [v(-4.81, -9.3) * mm, v(-4.79, -9.34) * mm, v(-4.78, -9.34) * mm, v(-4.74, -9.32) * mm]});
            skFitSpline(sketch, "E187", {"points": [v(-4.74, -9.32) * mm, v(-4.7, -9.3) * mm, v(-4.7, -9.3) * mm, v(-4.7, -9.27) * mm]});
            skFitSpline(sketch, "E188", {"points": [v(-4.7, -9.27) * mm, v(-4.7, -9.24) * mm, v(-4.7, -9.23) * mm, v(-4.65, -9.24) * mm]});
            skFitSpline(sketch, "E189", {"points": [v(-4.65, -9.24) * mm, v(-4.63, -9.24) * mm, v(-4.62, -9.25) * mm, v(-4.63, -9.27) * mm]});
            skFitSpline(sketch, "E190", {"points": [v(-4.63, -9.27) * mm, v(-4.64, -9.3) * mm, v(-4.5, -9.28) * mm, v(-4.25, -9.2) * mm]});
            skFitSpline(sketch, "E191", {"points": [v(-4.25, -9.2) * mm, v(-4.13, -9.17) * mm, v(-4, -9.13) * mm, v(-3.94, -9.13) * mm]});
            skFitSpline(sketch, "E192", {"points": [v(-3.94, -9.13) * mm, v(-3.87, -9.12) * mm, v(-3.85, -9.12) * mm, v(-3.82, -9.15) * mm]});
            skFitSpline(sketch, "E193", {"points": [v(-3.82, -9.15) * mm, v(-3.74, -9.23) * mm, v(-3.77, -9.25) * mm, v(-4, -9.29) * mm]});
            skFitSpline(sketch, "E194", {"points": [v(-4, -9.29) * mm, v(-4.28, -9.34) * mm, v(-4.64, -9.42) * mm, v(-4.64, -9.43) * mm]});
            skFitSpline(sketch, "E195", {"points": [v(-4.64, -9.43) * mm, v(-4.65, -9.46) * mm, v(-4.5, -9.68) * mm, v(-4.36, -9.88) * mm]});
            skFitSpline(sketch, "E196", {"points": [v(-4.36, -9.88) * mm, v(-4.3, -9.97) * mm, v(-4.22, -10.08) * mm, v(-4.19, -10.13) * mm]});
            skFitSpline(sketch, "E197", {"points": [v(-4.19, -10.13) * mm, v(-4.13, -10.2) * mm, v(-4.13, -10.21) * mm, v(-4.16, -10.24) * mm]});
            skFitSpline(sketch, "E198", {"points": [v(-4.16, -10.24) * mm, v(-4.2, -10.27) * mm, v(-4.23, -10.26) * mm, v(-4.3, -10.23) * mm]});
            skFitSpline(sketch, "E199", {"points": [v(4.56, -9.51) * mm, v(4.56, -9.24) * mm, v(4.57, -8.95) * mm, v(4.58, -8.88) * mm]});
            skFitSpline(sketch, "E200", {"points": [v(4.58, -8.88) * mm, v(4.59, -8.74) * mm, v(4.6, -8.72) * mm, v(4.74, -8.67) * mm]});
            skLineSegment(sketch, "E201", {"start": v(4.74, -8.67) * mm, "end": v(4.83, -8.63) * mm});
            skLineSegment(sketch, "E202", {"start": v(4.83, -8.63) * mm, "end": v(4.96, -8.75) * mm});
            skFitSpline(sketch, "E203", {"points": [v(4.96, -8.75) * mm, v(5.15, -8.93) * mm, v(5.3, -9.05) * mm, v(5.56, -9.23) * mm]});
            skFitSpline(sketch, "E204", {"points": [v(5.56, -9.23) * mm, v(5.7, -9.31) * mm, v(5.8, -9.4) * mm, v(5.8, -9.4) * mm]});
            skFitSpline(sketch, "E205", {"points": [v(5.8, -9.4) * mm, v(5.8, -9.41) * mm, v(5.78, -9.44) * mm, v(5.75, -9.46) * mm]});
            skLineSegment(sketch, "E206", {"start": v(5.75, -9.46) * mm, "end": v(5.7, -9.5) * mm});
            skLineSegment(sketch, "E207", {"start": v(5.7, -9.5) * mm, "end": v(5.65, -9.46) * mm});
            skFitSpline(sketch, "E208", {"points": [v(5.65, -9.46) * mm, v(5.62, -9.44) * mm, v(5.58, -9.4) * mm, v(5.55, -9.39) * mm]});
            skFitSpline(sketch, "E209", {"points": [v(5.55, -9.39) * mm, v(5.49, -9.34) * mm, v(5.44, -9.34) * mm, v(5.4, -9.38) * mm]});
            skLineSegment(sketch, "E210", {"start": v(5.4, -9.38) * mm, "end": v(5.36, -9.42) * mm});
            skLineSegment(sketch, "E211", {"start": v(5.36, -9.42) * mm, "end": v(5.4, -9.43) * mm});
            skFitSpline(sketch, "E212", {"points": [v(5.4, -9.43) * mm, v(5.45, -9.43) * mm, v(5.43, -9.45) * mm, v(5.21, -9.55) * mm]});
            skFitSpline(sketch, "E213", {"points": [v(5.21, -9.55) * mm, v(5.08, -9.62) * mm, v(4.97, -9.67) * mm, v(4.97, -9.67) * mm]});
            skFitSpline(sketch, "E214", {"points": [v(4.97, -9.67) * mm, v(4.97, -9.66) * mm, v(5.03, -9.63) * mm, v(5.11, -9.59) * mm]});
            skFitSpline(sketch, "E215", {"points": [v(5.11, -9.59) * mm, v(5.2, -9.55) * mm, v(5.28, -9.5) * mm, v(5.3, -9.48) * mm]});
            skFitSpline(sketch, "E216", {"points": [v(5.3, -9.48) * mm, v(5.36, -9.43) * mm, v(5.38, -9.42) * mm, v(5.03, -9.56) * mm]});
            skFitSpline(sketch, "E217", {"points": [v(5.03, -9.56) * mm, v(4.7, -9.69) * mm, v(4.7, -9.7) * mm, v(4.7, -9.85) * mm]});
            skFitSpline(sketch, "E218", {"points": [v(4.7, -9.85) * mm, v(4.7, -9.95) * mm, v(4.68, -10) * mm, v(4.6, -10.01) * mm]});
            skLineSegment(sketch, "E219", {"start": v(4.6, -10.01) * mm, "end": v(4.55, -10.02) * mm});
            skLineSegment(sketch, "E220", {"start": v(4.55, -10.02) * mm, "end": v(4.56, -9.51) * mm});
            skFitSpline(sketch, "E221", {"points": [v(4.8, -9.5) * mm, v(4.82, -9.48) * mm, v(4.84, -9.46) * mm, v(4.84, -9.44) * mm]});
            skFitSpline(sketch, "E222", {"points": [v(4.84, -9.44) * mm, v(4.84, -9.42) * mm, v(4.85, -9.4) * mm, v(4.86, -9.4) * mm]});
            skFitSpline(sketch, "E223", {"points": [v(4.86, -9.4) * mm, v(4.9, -9.4) * mm, v(5.03, -9.36) * mm, v(5.13, -9.3) * mm]});
            skFitSpline(sketch, "E224", {"points": [v(5.13, -9.3) * mm, v(5.2, -9.26) * mm, v(5.24, -9.24) * mm, v(5.26, -9.25) * mm]});
            skFitSpline(sketch, "E225", {"points": [v(5.26, -9.25) * mm, v(5.35, -9.27) * mm, v(5.3, -9.21) * mm, v(4.88, -8.87) * mm]});
            skLineSegment(sketch, "E226", {"start": v(4.88, -8.87) * mm, "end": v(4.77, -8.78) * mm});
            skLineSegment(sketch, "E227", {"start": v(4.77, -8.78) * mm, "end": v(4.76, -8.86) * mm});
            skFitSpline(sketch, "E228", {"points": [v(4.76, -8.86) * mm, v(4.76, -8.91) * mm, v(4.75, -8.97) * mm, v(4.73, -9) * mm]});
            skFitSpline(sketch, "E229", {"points": [v(4.73, -9) * mm, v(4.72, -9.02) * mm, v(4.71, -9.14) * mm, v(4.7, -9.28) * mm]});
            skFitSpline(sketch, "E230", {"points": [v(4.7, -9.28) * mm, v(4.7, -9.56) * mm, v(4.7, -9.56) * mm, v(4.8, -9.5) * mm]});
            skFitSpline(sketch, "E231", {"points": [v(4.82, -8.95) * mm, v(4.82, -8.9) * mm, v(4.83, -8.9) * mm, v(4.85, -8.93) * mm]});
            skFitSpline(sketch, "E232", {"points": [v(4.85, -8.93) * mm, v(4.88, -8.95) * mm, v(4.88, -8.96) * mm, v(4.85, -8.98) * mm]});
            skFitSpline(sketch, "E233", {"points": [v(4.85, -8.98) * mm, v(4.83, -9) * mm, v(4.82, -9) * mm, v(4.82, -8.95) * mm]});
            skFitSpline(sketch, "E234", {"points": [v(-4.5, -9.58) * mm, v(-4.5, -9.56) * mm, v(-4.52, -9.54) * mm, v(-4.52, -9.53) * mm]});
            skFitSpline(sketch, "E235", {"points": [v(-4.52, -9.53) * mm, v(-4.52, -9.52) * mm, v(-4.46, -9.5) * mm, v(-4.36, -9.48) * mm]});
            skFitSpline(sketch, "E236", {"points": [v(-4.36, -9.48) * mm, v(-4.33, -9.47) * mm, v(-4.33, -9.47) * mm, v(-4.35, -9.49) * mm]});
            skFitSpline(sketch, "E237", {"points": [v(-4.35, -9.49) * mm, v(-4.37, -9.5) * mm, v(-4.4, -9.5) * mm, v(-4.42, -9.52) * mm]});
            skFitSpline(sketch, "E238", {"points": [v(-4.42, -9.52) * mm, v(-4.46, -9.53) * mm, v(-4.46, -9.54) * mm, v(-4.46, -9.58) * mm]});
            skFitSpline(sketch, "E239", {"points": [v(-4.46, -9.58) * mm, v(-4.44, -9.63) * mm, v(-4.45, -9.63) * mm, v(-4.5, -9.58) * mm]});
            skFitSpline(sketch, "E240", {"points": [v(-6.07, -9.5) * mm, v(-6.1, -9.48) * mm, v(-6.1, -9.48) * mm, v(-6.1, -9.35) * mm]});
            skFitSpline(sketch, "E241", {"points": [v(-6.1, -9.35) * mm, v(-6.08, -9.2) * mm, v(-6.1, -9.17) * mm, v(-6.18, -9.17) * mm]});
            skFitSpline(sketch, "E242", {"points": [v(-6.18, -9.17) * mm, v(-6.22, -9.17) * mm, v(-6.23, -9.17) * mm, v(-6.21, -9.19) * mm]});
            skFitSpline(sketch, "E243", {"points": [v(-6.21, -9.19) * mm, v(-6.17, -9.23) * mm, v(-6.2, -9.23) * mm, v(-6.27, -9.19) * mm]});
            skFitSpline(sketch, "E244", {"points": [v(-6.27, -9.19) * mm, v(-6.36, -9.15) * mm, v(-6.68, -8.94) * mm, v(-6.68, -8.93) * mm]});
            skFitSpline(sketch, "E245", {"points": [v(-6.68, -8.93) * mm, v(-6.68, -8.92) * mm, v(-6.68, -8.92) * mm, v(-6.52, -9.02) * mm]});
            skFitSpline(sketch, "E246", {"points": [v(-6.52, -9.02) * mm, v(-6.4, -9.1) * mm, v(-6.27, -9.16) * mm, v(-6.26, -9.15) * mm]});
            skFitSpline(sketch, "E247", {"points": [v(-6.26, -9.15) * mm, v(-6.26, -9.15) * mm, v(-6.37, -9.06) * mm, v(-6.51, -8.96) * mm]});
            skFitSpline(sketch, "E248", {"points": [v(-6.51, -8.96) * mm, v(-6.69, -8.83) * mm, v(-6.79, -8.77) * mm, v(-6.81, -8.77) * mm]});
            skFitSpline(sketch, "E249", {"points": [v(-6.81, -8.77) * mm, v(-6.84, -8.77) * mm, v(-6.89, -8.8) * mm, v(-6.93, -8.81) * mm]});
            skFitSpline(sketch, "E250", {"points": [v(-6.93, -8.81) * mm, v(-7.05, -8.88) * mm, v(-7.08, -8.88) * mm, v(-7.14, -8.84) * mm]});
            skFitSpline(sketch, "E251", {"points": [v(-7.14, -8.84) * mm, v(-7.17, -8.8) * mm, v(-7.18, -8.8) * mm, v(-7.16, -8.78) * mm]});
            skFitSpline(sketch, "E252", {"points": [v(-7.16, -8.78) * mm, v(-7.14, -8.76) * mm, v(-6.26, -8.23) * mm, v(-6.17, -8.18) * mm]});
            skFitSpline(sketch, "E253", {"points": [v(-6.17, -8.18) * mm, v(-6.1, -8.14) * mm, v(-6.05, -8.14) * mm, v(-6, -8.18) * mm]});
            skFitSpline(sketch, "E254", {"points": [v(-6, -8.18) * mm, v(-5.87, -8.26) * mm, v(-5.85, -8.28) * mm, v(-5.85, -8.3) * mm]});
            skFitSpline(sketch, "E255", {"points": [v(-5.85, -8.3) * mm, v(-5.86, -8.3) * mm, v(-5.87, -8.41) * mm, v(-5.9, -8.53) * mm]});
            skFitSpline(sketch, "E256", {"points": [v(-5.9, -8.53) * mm, v(-5.92, -8.77) * mm, v(-5.95, -9.11) * mm, v(-5.95, -9.36) * mm]});
            skLineSegment(sketch, "E257", {"start": v(-5.95, -9.36) * mm, "end": v(-5.95, -9.52) * mm});
            skLineSegment(sketch, "E258", {"start": v(-5.95, -9.52) * mm, "end": v(-6, -9.52) * mm});
            skFitSpline(sketch, "E259", {"points": [v(-6, -9.52) * mm, v(-6.02, -9.51) * mm, v(-6.05, -9.5) * mm, v(-6.07, -9.5) * mm]});
            skLineSegment(sketch, "E260", {"start": v(-6.07, -9.5) * mm, "end": v(-6.07, -9.5) * mm});
            skFitSpline(sketch, "E261", {"points": [v(-6.08, -8.91) * mm, v(-6.07, -8.86) * mm, v(-6.06, -8.72) * mm, v(-6.04, -8.61) * mm]});
            skFitSpline(sketch, "E262", {"points": [v(-6.04, -8.61) * mm, v(-6.02, -8.5) * mm, v(-6.01, -8.4) * mm, v(-6.01, -8.36) * mm]});
            skLineSegment(sketch, "E263", {"start": v(-6.01, -8.36) * mm, "end": v(-6.01, -8.3) * mm});
            skLineSegment(sketch, "E264", {"start": v(-6.01, -8.3) * mm, "end": v(-6.07, -8.34) * mm});
            skFitSpline(sketch, "E265", {"points": [v(-6.07, -8.34) * mm, v(-6.1, -8.36) * mm, v(-6.15, -8.38) * mm, v(-6.18, -8.39) * mm]});
            skFitSpline(sketch, "E266", {"points": [v(-6.18, -8.39) * mm, v(-6.26, -8.4) * mm, v(-6.35, -8.45) * mm, v(-6.48, -8.53) * mm]});
            skFitSpline(sketch, "E267", {"points": [v(-6.48, -8.53) * mm, v(-6.54, -8.57) * mm, v(-6.61, -8.61) * mm, v(-6.64, -8.62) * mm]});
            skFitSpline(sketch, "E268", {"points": [v(-6.64, -8.62) * mm, v(-6.66, -8.63) * mm, v(-6.68, -8.65) * mm, v(-6.68, -8.65) * mm]});
            skFitSpline(sketch, "E269", {"points": [v(-6.68, -8.65) * mm, v(-6.68, -8.68) * mm, v(-6.58, -8.73) * mm, v(-6.54, -8.72) * mm]});
            skFitSpline(sketch, "E270", {"points": [v(-6.54, -8.72) * mm, v(-6.51, -8.72) * mm, v(-6.48, -8.74) * mm, v(-6.44, -8.78) * mm]});
            skFitSpline(sketch, "E271", {"points": [v(-6.44, -8.78) * mm, v(-6.4, -8.8) * mm, v(-6.32, -8.86) * mm, v(-6.25, -8.9) * mm]});
            skFitSpline(sketch, "E272", {"points": [v(-6.25, -8.9) * mm, v(-6.17, -8.93) * mm, v(-6.13, -8.96) * mm, v(-6.13, -8.98) * mm]});
            skFitSpline(sketch, "E273", {"points": [v(-6.13, -8.98) * mm, v(-6.1, -9.04) * mm, v(-6.1, -9.02) * mm, v(-6.08, -8.91) * mm]});
            skLineSegment(sketch, "E274", {"start": v(-6.08, -8.91) * mm, "end": v(-6.08, -8.91) * mm});
            skFitSpline(sketch, "E275", {"points": [v(-6.14, -8.46) * mm, v(-6.1, -8.43) * mm, v(-6.09, -8.43) * mm, v(-6.09, -8.46) * mm]});
            skFitSpline(sketch, "E276", {"points": [v(-6.09, -8.46) * mm, v(-6.09, -8.48) * mm, v(-6.1, -8.48) * mm, v(-6.13, -8.48) * mm]});
            skFitSpline(sketch, "E277", {"points": [v(-6.13, -8.48) * mm, v(-6.17, -8.48) * mm, v(-6.17, -8.48) * mm, v(-6.14, -8.46) * mm]});
            skLineSegment(sketch, "E278", {"start": v(-6.14, -8.46) * mm, "end": v(-6.14, -8.46) * mm});
            skFitSpline(sketch, "E279", {"points": [v(-0.5, -9.21) * mm, v(-2.56, -9.16) * mm, v(-4.55, -8.48) * mm, v(-6.24, -7.25) * mm]});
            skFitSpline(sketch, "E280", {"points": [v(-6.24, -7.25) * mm, v(-6.5, -7.07) * mm, v(-6.84, -6.8) * mm, v(-6.88, -6.74) * mm]});
            skFitSpline(sketch, "E281", {"points": [v(-6.88, -6.74) * mm, v(-6.98, -6.6) * mm, v(-7.02, -6.43) * mm, v(-7, -6.28) * mm]});
            skFitSpline(sketch, "E282", {"points": [v(-7, -6.28) * mm, v(-6.97, -6.12) * mm, v(-6.92, -6.04) * mm, v(-6.7, -5.8) * mm]});
            skLineSegment(sketch, "E283", {"start": v(-6.7, -5.8) * mm, "end": v(-6.5, -5.6) * mm});
            skLineSegment(sketch, "E284", {"start": v(-6.5, -5.6) * mm, "end": v(-6.53, -5.53) * mm});
            skFitSpline(sketch, "E285", {"points": [v(-6.53, -5.53) * mm, v(-6.56, -5.46) * mm, v(-6.56, -5.39) * mm, v(-6.52, -5.29) * mm]});
            skFitSpline(sketch, "E286", {"points": [v(-6.52, -5.29) * mm, v(-6.5, -5.25) * mm, v(-5.56, -4.1) * mm, v(-5.07, -3.53) * mm]});
            skFitSpline(sketch, "E287", {"points": [v(-5.07, -3.53) * mm, v(-5, -3.45) * mm, v(-4.94, -3.38) * mm, v(-4.93, -3.36) * mm]});
            skFitSpline(sketch, "E288", {"points": [v(-4.93, -3.36) * mm, v(-4.9, -3.34) * mm, v(-4.87, -3.3) * mm, v(-4.84, -3.26) * mm]});
            skFitSpline(sketch, "E289", {"points": [v(-4.84, -3.26) * mm, v(-4.81, -3.22) * mm, v(-4.73, -3.12) * mm, v(-4.66, -3.04) * mm]});
            skFitSpline(sketch, "E290", {"points": [v(-4.66, -3.04) * mm, v(-4.6, -2.95) * mm, v(-4.47, -2.8) * mm, v(-4.4, -2.72) * mm]});
            skFitSpline(sketch, "E291", {"points": [v(-4.4, -2.72) * mm, v(-4.32, -2.63) * mm, v(-4.17, -2.45) * mm, v(-4.07, -2.32) * mm]});
            skFitSpline(sketch, "E292", {"points": [v(-4.07, -2.32) * mm, v(-3.96, -2.2) * mm, v(-3.87, -2.08) * mm, v(-3.86, -2.06) * mm]});
            skFitSpline(sketch, "E293", {"points": [v(-3.86, -2.06) * mm, v(-3.84, -2.05) * mm, v(-3.74, -1.93) * mm, v(-3.63, -1.8) * mm]});
            skFitSpline(sketch, "E294", {"points": [v(-3.63, -1.8) * mm, v(-3.52, -1.66) * mm, v(-3.42, -1.55) * mm, v(-3.42, -1.55) * mm]});
            skFitSpline(sketch, "E295", {"points": [v(-3.42, -1.55) * mm, v(-3.42, -1.56) * mm, v(-3.4, -1.6) * mm, v(-3.4, -1.67) * mm]});
            skFitSpline(sketch, "E296", {"points": [v(-3.4, -1.67) * mm, v(-3.38, -1.73) * mm, v(-3.35, -1.84) * mm, v(-3.33, -1.9) * mm]});
            skFitSpline(sketch, "E297", {"points": [v(-3.33, -1.9) * mm, v(-3.24, -2.18) * mm, v(-3.15, -2.34) * mm, v(-2.9, -2.64) * mm]});
            skLineSegment(sketch, "E298", {"start": v(-2.9, -2.64) * mm, "end": v(-2.87, -2.68) * mm});
            skLineSegment(sketch, "E299", {"start": v(-2.87, -2.68) * mm, "end": v(-3.08, -2.9) * mm});
            skFitSpline(sketch, "E300", {"points": [v(-3.08, -2.9) * mm, v(-3.2, -3.03) * mm, v(-3.44, -3.29) * mm, v(-3.62, -3.48) * mm]});
            skFitSpline(sketch, "E301", {"points": [v(-3.62, -3.48) * mm, v(-3.8, -3.67) * mm, v(-4.02, -3.9) * mm, v(-4.1, -3.99) * mm]});
            skFitSpline(sketch, "E302", {"points": [v(-4.1, -3.99) * mm, v(-4.18, -4.08) * mm, v(-4.33, -4.25) * mm, v(-4.45, -4.36) * mm]});
            skFitSpline(sketch, "E303", {"points": [v(-4.45, -4.36) * mm, v(-4.56, -4.48) * mm, v(-4.74, -4.66) * mm, v(-4.84, -4.77) * mm]});
            skFitSpline(sketch, "E304", {"points": [v(-4.84, -4.77) * mm, v(-4.94, -4.88) * mm, v(-5.07, -5.03) * mm, v(-5.14, -5.1) * mm]});
            skFitSpline(sketch, "E305", {"points": [v(-5.14, -5.1) * mm, v(-5.43, -5.4) * mm, v(-5.83, -5.8) * mm, v(-5.9, -5.85) * mm]});
            skFitSpline(sketch, "E306", {"points": [v(-5.9, -5.85) * mm, v(-6, -5.92) * mm, v(-6.08, -5.92) * mm, v(-6.18, -5.87) * mm]});
            skLineSegment(sketch, "E307", {"start": v(-6.18, -5.87) * mm, "end": v(-6.24, -5.83) * mm});
            skLineSegment(sketch, "E308", {"start": v(-6.24, -5.83) * mm, "end": v(-6.36, -5.93) * mm});
            skFitSpline(sketch, "E309", {"points": [v(-6.36, -5.93) * mm, v(-6.54, -6.08) * mm, v(-6.6, -6.18) * mm, v(-6.6, -6.34) * mm]});
            skFitSpline(sketch, "E310", {"points": [v(-6.6, -6.34) * mm, v(-6.6, -6.5) * mm, v(-6.54, -6.6) * mm, v(-6.33, -6.77) * mm]});
            skFitSpline(sketch, "E311", {"points": [v(-6.33, -6.77) * mm, v(-6.05, -6.98) * mm, v(-5.96, -7.04) * mm, v(-5.68, -7.23) * mm]});
            skFitSpline(sketch, "E312", {"points": [v(-5.68, -7.23) * mm, v(-4.43, -8.06) * mm, v(-3.02, -8.6) * mm, v(-1.51, -8.8) * mm]});
            skFitSpline(sketch, "E313", {"points": [v(-1.51, -8.8) * mm, v(-1, -8.86) * mm, v(-0.86, -8.87) * mm, v(-0.18, -8.87) * mm]});
            skFitSpline(sketch, "E314", {"points": [v(-0.18, -8.87) * mm, v(0.52, -8.87) * mm, v(0.7, -8.86) * mm, v(1.24, -8.78) * mm]});
            skFitSpline(sketch, "E315", {"points": [v(1.24, -8.78) * mm, v(2.62, -8.58) * mm, v(3.97, -8.08) * mm, v(5.15, -7.33) * mm]});
            skFitSpline(sketch, "E316", {"points": [v(5.15, -7.33) * mm, v(6.24, -6.63) * mm, v(7.18, -5.74) * mm, v(7.93, -4.69) * mm]});
            skFitSpline(sketch, "E317", {"points": [v(7.93, -4.69) * mm, v(8.8, -3.47) * mm, v(9.37, -2.06) * mm, v(9.62, -0.59) * mm]});
            skFitSpline(sketch, "E318", {"points": [v(9.62, -0.59) * mm, v(9.72, 0) * mm, v(9.75, 0.4) * mm, v(9.75, 1.08) * mm]});
            skFitSpline(sketch, "E319", {"points": [v(9.75, 1.08) * mm, v(9.75, 1.69) * mm, v(9.73, 1.97) * mm, v(9.66, 2.47) * mm]});
            skFitSpline(sketch, "E320", {"points": [v(9.66, 2.47) * mm, v(9.48, 3.7) * mm, v(9.07, 4.9) * mm, v(8.46, 5.99) * mm]});
            skFitSpline(sketch, "E321", {"points": [v(8.46, 5.99) * mm, v(7.4, 7.83) * mm, v(5.78, 9.3) * mm, v(3.84, 10.16) * mm]});
            skFitSpline(sketch, "E322", {"points": [v(3.84, 10.16) * mm, v(1.96, 11) * mm, v(-0.15, 11.23) * mm, v(-2.2, 10.81) * mm]});
            skFitSpline(sketch, "E323", {"points": [v(-2.2, 10.81) * mm, v(-3.6, 10.53) * mm, v(-5, 9.9) * mm, v(-6.15, 9.03) * mm]});
            skFitSpline(sketch, "E324", {"points": [v(-6.15, 9.03) * mm, v(-6.53, 8.75) * mm, v(-6.83, 8.48) * mm, v(-7.2, 8.11) * mm]});
            skFitSpline(sketch, "E325", {"points": [v(-7.2, 8.11) * mm, v(-7.76, 7.56) * mm, v(-8.08, 7.16) * mm, v(-8.51, 6.53) * mm]});
            skFitSpline(sketch, "E326", {"points": [v(-8.51, 6.53) * mm, v(-8.9, 5.94) * mm, v(-9.3, 5.13) * mm, v(-9.56, 4.42) * mm]});
            skFitSpline(sketch, "E327", {"points": [v(-9.56, 4.42) * mm, v(-9.97, 3.26) * mm, v(-10.16, 2.1) * mm, v(-10.13, 0.86) * mm]});
            skFitSpline(sketch, "E328", {"points": [v(-10.13, 0.86) * mm, v(-10.11, -0.23) * mm, v(-9.95, -1.14) * mm, v(-9.6, -2.16) * mm]});
            skFitSpline(sketch, "E329", {"points": [v(-9.6, -2.16) * mm, v(-9.34, -2.95) * mm, v(-8.9, -3.85) * mm, v(-8.56, -4.29) * mm]});
            skFitSpline(sketch, "E330", {"points": [v(-8.56, -4.29) * mm, v(-8.42, -4.48) * mm, v(-8.3, -4.55) * mm, v(-8.14, -4.55) * mm]});
            skFitSpline(sketch, "E331", {"points": [v(-8.14, -4.55) * mm, v(-8.01, -4.55) * mm, v(-7.98, -4.53) * mm, v(-7.8, -4.35) * mm]});
            skFitSpline(sketch, "E332", {"points": [v(-7.8, -4.35) * mm, v(-7.71, -4.26) * mm, v(-7.61, -4.15) * mm, v(-7.58, -4.12) * mm]});
            skLineSegment(sketch, "E333", {"start": v(-7.58, -4.12) * mm, "end": v(-7.53, -4.05) * mm});
            skLineSegment(sketch, "E334", {"start": v(-7.53, -4.05) * mm, "end": v(-7.57, -4) * mm});
            skFitSpline(sketch, "E335", {"points": [v(-7.57, -4) * mm, v(-7.6, -3.97) * mm, v(-7.62, -3.93) * mm, v(-7.62, -3.92) * mm]});
            skFitSpline(sketch, "E336", {"points": [v(-7.62, -3.92) * mm, v(-7.62, -3.9) * mm, v(-7.53, -3.79) * mm, v(-7.36, -3.59) * mm]});
            skFitSpline(sketch, "E337", {"points": [v(-7.36, -3.59) * mm, v(-7.2, -3.42) * mm, v(-7.12, -3.3) * mm, v(-7.1, -3.27) * mm]});
            skFitSpline(sketch, "E338", {"points": [v(-7.1, -3.27) * mm, v(-7.07, -3.22) * mm, v(-7.07, -3.22) * mm, v(-7.1, -3.15) * mm]});
            skLineSegment(sketch, "E339", {"start": v(-7.1, -3.15) * mm, "end": v(-7.14, -3.08) * mm});
            skLineSegment(sketch, "E340", {"start": v(-7.14, -3.08) * mm, "end": v(-7.08, -3.02) * mm});
            skFitSpline(sketch, "E341", {"points": [v(-7.08, -3.02) * mm, v(-7.03, -2.97) * mm, v(-7.01, -2.96) * mm, v(-6.97, -2.96) * mm]});
            skFitSpline(sketch, "E342", {"points": [v(-6.97, -2.96) * mm, v(-6.9, -2.96) * mm, v(-6.82, -2.9) * mm, v(-6.8, -2.83) * mm]});
            skFitSpline(sketch, "E343", {"points": [v(-6.8, -2.83) * mm, v(-6.8, -2.8) * mm, v(-6.78, -2.73) * mm, v(-6.77, -2.69) * mm]});
            skFitSpline(sketch, "E344", {"points": [v(-6.77, -2.69) * mm, v(-6.74, -2.55) * mm, v(-6.7, -2.46) * mm, v(-6.53, -2.28) * mm]});
            skFitSpline(sketch, "E345", {"points": [v(-6.53, -2.28) * mm, v(-6.37, -2.1) * mm, v(-6.36, -2.08) * mm, v(-6.41, -2.03) * mm]});
            skFitSpline(sketch, "E346", {"points": [v(-6.41, -2.03) * mm, v(-6.46, -2) * mm, v(-6.42, -1.89) * mm, v(-6.32, -1.77) * mm]});
            skFitSpline(sketch, "E347", {"points": [v(-6.32, -1.77) * mm, v(-6.24, -1.68) * mm, v(-6.25, -1.68) * mm, v(-6.08, -1.83) * mm]});
            skFitSpline(sketch, "E348", {"points": [v(-6.08, -1.83) * mm, v(-6.02, -1.88) * mm, v(-5.96, -1.93) * mm, v(-5.95, -1.93) * mm]});
            skFitSpline(sketch, "E349", {"points": [v(-5.95, -1.93) * mm, v(-5.95, -1.93) * mm, v(-5.8, -1.77) * mm, v(-5.62, -1.57) * mm]});
            skFitSpline(sketch, "E350", {"points": [v(-5.62, -1.57) * mm, v(-5.2, -1.12) * mm, v(-5.25, -1.16) * mm, v(-5.23, -1.19) * mm]});
            skFitSpline(sketch, "E351", {"points": [v(-5.23, -1.19) * mm, v(-5.21, -1.2) * mm, v(-5.2, -1.22) * mm, v(-5.22, -1.23) * mm]});
            skFitSpline(sketch, "E352", {"points": [v(-5.22, -1.23) * mm, v(-5.22, -1.25) * mm, v(-5.37, -1.42) * mm, v(-5.55, -1.61) * mm]});
            skFitSpline(sketch, "E353", {"points": [v(-5.55, -1.61) * mm, v(-5.72, -1.81) * mm, v(-5.87, -1.98) * mm, v(-5.87, -2) * mm]});
            skFitSpline(sketch, "E354", {"points": [v(-5.87, -2) * mm, v(-5.88, -2.01) * mm, v(-5.63, -2.24) * mm, v(-5.39, -2.46) * mm]});
            skLineSegment(sketch, "E355", {"start": v(-5.39, -2.46) * mm, "end": v(-5.33, -2.5) * mm});
            skLineSegment(sketch, "E356", {"start": v(-5.33, -2.5) * mm, "end": v(-4.96, -2.13) * mm});
            skFitSpline(sketch, "E357", {"points": [v(-4.96, -2.13) * mm, v(-4.61, -1.78) * mm, v(-4.6, -1.76) * mm, v(-4.57, -1.79) * mm]});
            skFitSpline(sketch, "E358", {"points": [v(-4.57, -1.79) * mm, v(-4.54, -1.8) * mm, v(-4.55, -1.82) * mm, v(-4.82, -2.1) * mm]});
            skFitSpline(sketch, "E359", {"points": [v(-4.82, -2.1) * mm, v(-4.97, -2.26) * mm, v(-5.13, -2.43) * mm, v(-5.17, -2.48) * mm]});
            skLineSegment(sketch, "E360", {"start": v(-5.17, -2.48) * mm, "end": v(-5.26, -2.57) * mm});
            skLineSegment(sketch, "E361", {"start": v(-5.26, -2.57) * mm, "end": v(-5.13, -2.7) * mm});
            skFitSpline(sketch, "E362", {"points": [v(-5.13, -2.7) * mm, v(-5.07, -2.76) * mm, v(-5, -2.83) * mm, v(-5, -2.84) * mm]});
            skFitSpline(sketch, "E363", {"points": [v(-5, -2.84) * mm, v(-5, -2.86) * mm, v(-5.21, -3.08) * mm, v(-5.23, -3.08) * mm]});
            skFitSpline(sketch, "E364", {"points": [v(-5.23, -3.08) * mm, v(-5.25, -3.08) * mm, v(-5.28, -3.06) * mm, v(-5.3, -3.04) * mm]});
            skFitSpline(sketch, "E365", {"points": [v(-5.3, -3.04) * mm, v(-5.33, -3.02) * mm, v(-5.37, -3) * mm, v(-5.38, -3) * mm]});
            skFitSpline(sketch, "E366", {"points": [v(-5.38, -3) * mm, v(-5.39, -3) * mm, v(-5.48, -3.08) * mm, v(-5.57, -3.18) * mm]});
            skFitSpline(sketch, "E367", {"points": [v(-5.57, -3.18) * mm, v(-5.79, -3.4) * mm, v(-5.85, -3.44) * mm, v(-5.96, -3.45) * mm]});
            skFitSpline(sketch, "E368", {"points": [v(-5.96, -3.45) * mm, v(-6.12, -3.47) * mm, v(-6.2, -3.56) * mm, v(-6.19, -3.67) * mm]});
            skFitSpline(sketch, "E369", {"points": [v(-6.19, -3.67) * mm, v(-6.18, -3.73) * mm, v(-6.19, -3.74) * mm, v(-6.25, -3.8) * mm]});
            skLineSegment(sketch, "E370", {"start": v(-6.25, -3.8) * mm, "end": v(-6.31, -3.86) * mm});
            skLineSegment(sketch, "E371", {"start": v(-6.31, -3.86) * mm, "end": v(-6.37, -3.83) * mm});
            skFitSpline(sketch, "E372", {"points": [v(-6.37, -3.83) * mm, v(-6.44, -3.78) * mm, v(-6.5, -3.8) * mm, v(-6.58, -3.89) * mm]});
            skFitSpline(sketch, "E373", {"points": [v(-6.58, -3.89) * mm, v(-6.71, -4.03) * mm, v(-7.05, -4.36) * mm, v(-7.09, -4.38) * mm]});
            skFitSpline(sketch, "E374", {"points": [v(-7.09, -4.38) * mm, v(-7.12, -4.4) * mm, v(-7.12, -4.4) * mm, v(-7.2, -4.36) * mm]});
            skLineSegment(sketch, "E375", {"start": v(-7.2, -4.36) * mm, "end": v(-7.26, -4.3) * mm});
            skLineSegment(sketch, "E376", {"start": v(-7.26, -4.3) * mm, "end": v(-7.51, -4.56) * mm});
            skFitSpline(sketch, "E377", {"points": [v(-7.51, -4.56) * mm, v(-7.65, -4.7) * mm, v(-7.8, -4.82) * mm, v(-7.83, -4.84) * mm]});
            skFitSpline(sketch, "E378", {"points": [v(-7.83, -4.84) * mm, v(-8.04, -4.97) * mm, v(-8.25, -4.99) * mm, v(-8.45, -4.89) * mm]});
            skFitSpline(sketch, "E379", {"points": [v(-8.45, -4.89) * mm, v(-8.68, -4.77) * mm, v(-8.98, -4.35) * mm, v(-9.36, -3.59) * mm]});
            skFitSpline(sketch, "E380", {"points": [v(-9.36, -3.59) * mm, v(-10.26, -1.83) * mm, v(-10.63, 0.16) * mm, v(-10.42, 2.16) * mm]});
            skFitSpline(sketch, "E381", {"points": [v(-10.42, 2.16) * mm, v(-10.34, 2.88) * mm, v(-10.17, 3.67) * mm, v(-9.95, 4.34) * mm]});
            skFitSpline(sketch, "E382", {"points": [v(-9.95, 4.34) * mm, v(-9.04, 7.02) * mm, v(-7.08, 9.2) * mm, v(-4.52, 10.4) * mm]});
            skFitSpline(sketch, "E383", {"points": [v(-4.52, 10.4) * mm, v(-3.6, 10.82) * mm, v(-2.5, 11.14) * mm, v(-1.51, 11.27) * mm]});
            skFitSpline(sketch, "E384", {"points": [v(-1.51, 11.27) * mm, v(-0.74, 11.37) * mm, v(0.1, 11.38) * mm, v(0.86, 11.3) * mm]});
            skFitSpline(sketch, "E385", {"points": [v(0.86, 11.3) * mm, v(2, 11.18) * mm, v(3.12, 10.87) * mm, v(4.16, 10.39) * mm]});
            skFitSpline(sketch, "E386", {"points": [v(4.16, 10.39) * mm, v(4.9, 10.04) * mm, v(5.67, 9.56) * mm, v(6.3, 9.05) * mm]});
            skFitSpline(sketch, "E387", {"points": [v(6.3, 9.05) * mm, v(8.25, 7.45) * mm, v(9.54, 5.24) * mm, v(9.95, 2.77) * mm]});
            skFitSpline(sketch, "E388", {"points": [v(9.95, 2.77) * mm, v(10.1, 1.9) * mm, v(10.13, 0.86) * mm, v(10.04, -0.02) * mm]});
            skFitSpline(sketch, "E389", {"points": [v(10.04, -0.02) * mm, v(9.79, -2.34) * mm, v(8.78, -4.47) * mm, v(7.16, -6.13) * mm]});
            skFitSpline(sketch, "E390", {"points": [v(7.16, -6.13) * mm, v(6, -7.3) * mm, v(4.66, -8.15) * mm, v(3.09, -8.69) * mm]});
            skFitSpline(sketch, "E391", {"points": [v(3.09, -8.69) * mm, v(2.28, -8.96) * mm, v(1.37, -9.14) * mm, v(0.47, -9.2) * mm]});
            skFitSpline(sketch, "E392", {"points": [v(0.47, -9.2) * mm, v(0.12, -9.22) * mm, v(-0.06, -9.22) * mm, v(-0.5, -9.21) * mm]});
            skFitSpline(sketch, "E393", {"points": [v(6.37, -8.88) * mm, v(6.28, -8.82) * mm, v(6.12, -8.6) * mm, v(6.03, -8.43) * mm]});
            skFitSpline(sketch, "E394", {"points": [v(6.03, -8.43) * mm, v(5.94, -8.25) * mm, v(5.93, -8.13) * mm, v(5.98, -8.03) * mm]});
            skFitSpline(sketch, "E395", {"points": [v(5.98, -8.03) * mm, v(6.06, -7.86) * mm, v(6.53, -7.5) * mm, v(6.72, -7.45) * mm]});
            skFitSpline(sketch, "E396", {"points": [v(6.72, -7.45) * mm, v(6.85, -7.42) * mm, v(7, -7.49) * mm, v(7.04, -7.6) * mm]});
            skFitSpline(sketch, "E397", {"points": [v(7.04, -7.6) * mm, v(7.06, -7.64) * mm, v(7.06, -7.65) * mm, v(7.03, -7.68) * mm]});
            skFitSpline(sketch, "E398", {"points": [v(7.03, -7.68) * mm, v(7, -7.73) * mm, v(6.95, -7.72) * mm, v(6.87, -7.64) * mm]});
            skFitSpline(sketch, "E399", {"points": [v(6.87, -7.64) * mm, v(6.8, -7.58) * mm, v(6.8, -7.57) * mm, v(6.76, -7.59) * mm]});
            skFitSpline(sketch, "E400", {"points": [v(6.76, -7.59) * mm, v(6.71, -7.6) * mm, v(6.71, -7.63) * mm, v(6.76, -7.64) * mm]});
            skFitSpline(sketch, "E401", {"points": [v(6.76, -7.64) * mm, v(6.81, -7.65) * mm, v(6.83, -7.64) * mm, v(6.6, -7.79) * mm]});
            skFitSpline(sketch, "E402", {"points": [v(6.6, -7.79) * mm, v(6.52, -7.84) * mm, v(6.4, -7.94) * mm, v(6.33, -8) * mm]});
            skFitSpline(sketch, "E403", {"points": [v(6.33, -8) * mm, v(6.25, -8.08) * mm, v(6.2, -8.14) * mm, v(6.18, -8.14) * mm]});
            skFitSpline(sketch, "E404", {"points": [v(6.18, -8.14) * mm, v(6.18, -8.14) * mm, v(6.18, -8.1) * mm, v(6.18, -8.07) * mm]});
            skLineSegment(sketch, "E405", {"start": v(6.18, -8.07) * mm, "end": v(6.2, -8.01) * mm});
            skLineSegment(sketch, "E406", {"start": v(6.2, -8.01) * mm, "end": v(6.15, -8.03) * mm});
            skFitSpline(sketch, "E407", {"points": [v(6.15, -8.03) * mm, v(6.1, -8.06) * mm, v(6.08, -8.09) * mm, v(6.09, -8.16) * mm]});
            skFitSpline(sketch, "E408", {"points": [v(6.09, -8.16) * mm, v(6.09, -8.24) * mm, v(6.14, -8.36) * mm, v(6.23, -8.5) * mm]});
            skFitSpline(sketch, "E409", {"points": [v(6.23, -8.5) * mm, v(6.32, -8.64) * mm, v(6.4, -8.72) * mm, v(6.45, -8.74) * mm]});
            skFitSpline(sketch, "E410", {"points": [v(6.45, -8.74) * mm, v(6.54, -8.77) * mm, v(6.68, -8.75) * mm, v(6.68, -8.7) * mm]});
            skFitSpline(sketch, "E411", {"points": [v(6.68, -8.7) * mm, v(6.68, -8.7) * mm, v(6.72, -8.66) * mm, v(6.76, -8.64) * mm]});
            skFitSpline(sketch, "E412", {"points": [v(6.76, -8.64) * mm, v(6.92, -8.55) * mm, v(7.06, -8.44) * mm, v(7.16, -8.34) * mm]});
            skFitSpline(sketch, "E413", {"points": [v(7.16, -8.34) * mm, v(7.22, -8.29) * mm, v(7.27, -8.24) * mm, v(7.28, -8.24) * mm]});
            skFitSpline(sketch, "E414", {"points": [v(7.28, -8.24) * mm, v(7.3, -8.24) * mm, v(7.3, -8.2) * mm, v(7.27, -8.11) * mm]});
            skFitSpline(sketch, "E415", {"points": [v(7.27, -8.11) * mm, v(7.24, -8.05) * mm, v(7.24, -8.04) * mm, v(7.26, -8) * mm]});
            skFitSpline(sketch, "E416", {"points": [v(7.26, -8) * mm, v(7.3, -7.96) * mm, v(7.33, -7.95) * mm, v(7.39, -7.97) * mm]});
            skFitSpline(sketch, "E417", {"points": [v(7.39, -7.97) * mm, v(7.61, -8.1) * mm, v(7.5, -8.35) * mm, v(7.06, -8.67) * mm]});
            skFitSpline(sketch, "E418", {"points": [v(7.06, -8.67) * mm, v(6.84, -8.83) * mm, v(6.68, -8.91) * mm, v(6.54, -8.92) * mm]});
            skFitSpline(sketch, "E419", {"points": [v(6.54, -8.92) * mm, v(6.45, -8.93) * mm, v(6.44, -8.92) * mm, v(6.37, -8.88) * mm]});
            skLineSegment(sketch, "E420", {"start": v(6.37, -8.88) * mm, "end": v(6.37, -8.88) * mm});
            skFitSpline(sketch, "E421", {"points": [v(-7.83, -8.33) * mm, v(-7.85, -8.31) * mm, v(-7.86, -8.29) * mm, v(-7.86, -8.27) * mm]});
            skFitSpline(sketch, "E422", {"points": [v(-7.86, -8.27) * mm, v(-7.86, -8.24) * mm, v(-7.55, -7.82) * mm, v(-7.41, -7.68) * mm]});
            skFitSpline(sketch, "E423", {"points": [v(-7.41, -7.68) * mm, v(-7.35, -7.62) * mm, v(-7.3, -7.56) * mm, v(-7.31, -7.55) * mm]});
            skFitSpline(sketch, "E424", {"points": [v(-7.31, -7.55) * mm, v(-7.32, -7.52) * mm, v(-7.4, -7.52) * mm, v(-7.43, -7.56) * mm]});
            skFitSpline(sketch, "E425", {"points": [v(-7.43, -7.56) * mm, v(-7.48, -7.61) * mm, v(-7.58, -7.66) * mm, v(-7.72, -7.7) * mm]});
            skFitSpline(sketch, "E426", {"points": [v(-7.72, -7.7) * mm, v(-7.8, -7.72) * mm, v(-7.9, -7.75) * mm, v(-7.93, -7.77) * mm]});
            skFitSpline(sketch, "E427", {"points": [v(-7.93, -7.77) * mm, v(-8.02, -7.8) * mm, v(-8.08, -7.8) * mm, v(-8.14, -7.73) * mm]});
            skFitSpline(sketch, "E428", {"points": [v(-8.14, -7.73) * mm, v(-8.17, -7.7) * mm, v(-8.17, -7.7) * mm, v(-8.15, -7.54) * mm]});
            skFitSpline(sketch, "E429", {"points": [v(-8.15, -7.54) * mm, v(-8.14, -7.39) * mm, v(-8.13, -7.15) * mm, v(-8.14, -7.16) * mm]});
            skFitSpline(sketch, "E430", {"points": [v(-8.14, -7.16) * mm, v(-8.15, -7.17) * mm, v(-8.17, -7.25) * mm, v(-8.19, -7.35) * mm]});
            skFitSpline(sketch, "E431", {"points": [v(-8.19, -7.35) * mm, v(-8.24, -7.6) * mm, v(-8.26, -7.63) * mm, v(-8.26, -7.48) * mm]});
            skFitSpline(sketch, "E432", {"points": [v(-8.26, -7.48) * mm, v(-8.25, -7.42) * mm, v(-8.26, -7.34) * mm, v(-8.27, -7.31) * mm]});
            skFitSpline(sketch, "E433", {"points": [v(-8.27, -7.31) * mm, v(-8.28, -7.23) * mm, v(-8.26, -7.18) * mm, v(-8.16, -7.1) * mm]});
            skFitSpline(sketch, "E434", {"points": [v(-8.16, -7.1) * mm, v(-8.07, -7.02) * mm, v(-8.02, -6.94) * mm, v(-8.04, -6.89) * mm]});
            skFitSpline(sketch, "E435", {"points": [v(-8.04, -6.89) * mm, v(-8.05, -6.86) * mm, v(-8.05, -6.86) * mm, v(-8.08, -6.88) * mm]});
            skFitSpline(sketch, "E436", {"points": [v(-8.08, -6.88) * mm, v(-8.15, -6.91) * mm, v(-8.27, -7.02) * mm, v(-8.5, -7.27) * mm]});
            skLineSegment(sketch, "E437", {"start": v(-8.5, -7.27) * mm, "end": v(-8.73, -7.53) * mm});
            skLineSegment(sketch, "E438", {"start": v(-8.73, -7.53) * mm, "end": v(-8.78, -7.5) * mm});
            skFitSpline(sketch, "E439", {"points": [v(-8.78, -7.5) * mm, v(-8.82, -7.48) * mm, v(-8.85, -7.44) * mm, v(-8.85, -7.4) * mm]});
            skFitSpline(sketch, "E440", {"points": [v(-8.85, -7.4) * mm, v(-8.85, -7.38) * mm, v(-8.7, -7.22) * mm, v(-8.46, -6.98) * mm]});
            skLineSegment(sketch, "E441", {"start": v(-8.46, -6.98) * mm, "end": v(-8.06, -6.6) * mm});
            skLineSegment(sketch, "E442", {"start": v(-8.06, -6.6) * mm, "end": v(-8, -6.62) * mm});
            skFitSpline(sketch, "E443", {"points": [v(-8, -6.62) * mm, v(-7.98, -6.64) * mm, v(-7.94, -6.67) * mm, v(-7.92, -6.69) * mm]});
            skFitSpline(sketch, "E444", {"points": [v(-7.92, -6.69) * mm, v(-7.9, -6.72) * mm, v(-7.9, -6.72) * mm, v(-7.91, -6.87) * mm]});
            skFitSpline(sketch, "E445", {"points": [v(-7.91, -6.87) * mm, v(-7.95, -7.08) * mm, v(-7.98, -7.37) * mm, v(-7.99, -7.49) * mm]});
            skFitSpline(sketch, "E446", {"points": [v(-7.99, -7.49) * mm, v(-8, -7.58) * mm, v(-7.99, -7.6) * mm, v(-7.96, -7.6) * mm]});
            skFitSpline(sketch, "E447", {"points": [v(-7.96, -7.6) * mm, v(-7.94, -7.6) * mm, v(-7.94, -7.6) * mm, v(-7.95, -7.56) * mm]});
            skFitSpline(sketch, "E448", {"points": [v(-7.95, -7.56) * mm, v(-7.96, -7.48) * mm, v(-7.93, -7.47) * mm, v(-7.77, -7.47) * mm]});
            skFitSpline(sketch, "E449", {"points": [v(-7.77, -7.47) * mm, v(-7.64, -7.47) * mm, v(-7.62, -7.47) * mm, v(-7.5, -7.42) * mm]});
            skFitSpline(sketch, "E450", {"points": [v(-7.5, -7.42) * mm, v(-7.38, -7.37) * mm, v(-7.26, -7.35) * mm, v(-7.2, -7.37) * mm]});
            skFitSpline(sketch, "E451", {"points": [v(-7.2, -7.37) * mm, v(-7.17, -7.37) * mm, v(-7.14, -7.4) * mm, v(-7.11, -7.41) * mm]});
            skLineSegment(sketch, "E452", {"start": v(-7.11, -7.41) * mm, "end": v(-7.07, -7.45) * mm});
            skLineSegment(sketch, "E453", {"start": v(-7.07, -7.45) * mm, "end": v(-7.1, -7.5) * mm});
            skFitSpline(sketch, "E454", {"points": [v(-7.1, -7.5) * mm, v(-7.28, -7.8) * mm, v(-7.6, -8.23) * mm, v(-7.68, -8.3) * mm]});
            skFitSpline(sketch, "E455", {"points": [v(-7.68, -8.3) * mm, v(-7.75, -8.37) * mm, v(-7.78, -8.38) * mm, v(-7.83, -8.33) * mm]});
            skFitSpline(sketch, "E456", {"points": [v(0.13, -8.3) * mm, v(0.16, -8.29) * mm, v(0.17, -8.29) * mm, v(0.18, -8.3) * mm]});
            skFitSpline(sketch, "E457", {"points": [v(0.18, -8.3) * mm, v(0.2, -8.31) * mm, v(0.19, -8.32) * mm, v(0.15, -8.32) * mm]});
            skFitSpline(sketch, "E458", {"points": [v(0.15, -8.32) * mm, v(0.1, -8.32) * mm, v(0.1, -8.31) * mm, v(0.13, -8.3) * mm]});
            skLineSegment(sketch, "E459", {"start": v(0.13, -8.3) * mm, "end": v(0.13, -8.3) * mm});
            skLineSegment(sketch, "E460", {"start": v(-0.71, -8.13) * mm, "end": v(-1, -8.12) * mm});
            skLineSegment(sketch, "E461", {"start": v(-1, -8.12) * mm, "end": v(-1.04, -8.07) * mm});
            skLineSegment(sketch, "E462", {"start": v(-1.04, -8.07) * mm, "end": v(-1.1, -8.02) * mm});
            skLineSegment(sketch, "E463", {"start": v(-1.1, -8.02) * mm, "end": v(-1.1, -6.58) * mm});
            skFitSpline(sketch, "E464", {"points": [v(-1.1, -6.58) * mm, v(-1.1, -4.96) * mm, v(-1.1, -5.1) * mm, v(-0.98, -5.08) * mm]});
            skFitSpline(sketch, "E465", {"points": [v(-0.98, -5.08) * mm, v(-0.92, -5.07) * mm, v(-0.9, -5.08) * mm, v(-0.87, -5.13) * mm]});
            skLineSegment(sketch, "E466", {"start": v(-0.87, -5.13) * mm, "end": v(-0.82, -5.18) * mm});
            skLineSegment(sketch, "E467", {"start": v(-0.82, -5.18) * mm, "end": v(-0.82, -5.81) * mm});
            skFitSpline(sketch, "E468", {"points": [v(-0.82, -5.81) * mm, v(-0.82, -6.16) * mm, v(-0.82, -6.73) * mm, v(-0.81, -7.08) * mm]});
            skLineSegment(sketch, "E469", {"start": v(-0.81, -7.08) * mm, "end": v(-0.8, -7.72) * mm});
            skLineSegment(sketch, "E470", {"start": v(-0.8, -7.72) * mm, "end": v(-0.72, -7.75) * mm});
            skFitSpline(sketch, "E471", {"points": [v(-0.72, -7.75) * mm, v(-0.6, -7.79) * mm, v(-0.44, -7.8) * mm, v(-0.17, -7.76) * mm]});
            skFitSpline(sketch, "E472", {"points": [v(-0.17, -7.76) * mm, v(0.27, -7.72) * mm, v(0.46, -7.73) * mm, v(0.6, -7.82) * mm]});
            skFitSpline(sketch, "E473", {"points": [v(0.6, -7.82) * mm, v(0.65, -7.84) * mm, v(0.67, -7.86) * mm, v(0.67, -7.88) * mm]});
            skFitSpline(sketch, "E474", {"points": [v(0.67, -7.88) * mm, v(0.67, -7.95) * mm, v(0.62, -8.07) * mm, v(0.58, -8.1) * mm]});
            skLineSegment(sketch, "E475", {"start": v(0.58, -8.1) * mm, "end": v(0.54, -8.14) * mm});
            skLineSegment(sketch, "E476", {"start": v(0.54, -8.14) * mm, "end": v(0.05, -8.14) * mm});
            skFitSpline(sketch, "E477", {"points": [v(0.05, -8.14) * mm, v(-0.21, -8.15) * mm, v(-0.56, -8.14) * mm, v(-0.71, -8.13) * mm]});
            skFitSpline(sketch, "E478", {"points": [v(-7.83, -8.08) * mm, v(-7.83, -8.08) * mm, v(-7.8, -8.03) * mm, v(-7.77, -7.97) * mm]});
            skFitSpline(sketch, "E479", {"points": [v(-7.77, -7.97) * mm, v(-7.71, -7.87) * mm, v(-7.7, -7.85) * mm, v(-7.75, -7.85) * mm]});
            skFitSpline(sketch, "E480", {"points": [v(-7.75, -7.85) * mm, v(-7.77, -7.85) * mm, v(-7.77, -7.84) * mm, v(-7.76, -7.83) * mm]});
            skFitSpline(sketch, "E481", {"points": [v(-7.76, -7.83) * mm, v(-7.74, -7.81) * mm, v(-7.56, -7.74) * mm, v(-7.55, -7.75) * mm]});
            skFitSpline(sketch, "E482", {"points": [v(-7.55, -7.75) * mm, v(-7.54, -7.76) * mm, v(-7.61, -7.88) * mm, v(-7.68, -7.96) * mm]});
            skFitSpline(sketch, "E483", {"points": [v(-7.68, -7.96) * mm, v(-7.74, -8.03) * mm, v(-7.83, -8.1) * mm, v(-7.83, -8.08) * mm]});
            skFitSpline(sketch, "E484", {"points": [v(-2.84, -8.06) * mm, v(-2.83, -8.06) * mm, v(-2.82, -8.06) * mm, v(-2.81, -8.07) * mm]});
            skFitSpline(sketch, "E485", {"points": [v(-2.81, -8.07) * mm, v(-2.8, -8.07) * mm, v(-2.82, -8.07) * mm, v(-2.83, -8.07) * mm]});
            skFitSpline(sketch, "E486", {"points": [v(-2.83, -8.07) * mm, v(-2.85, -8.07) * mm, v(-2.85, -8.07) * mm, v(-2.84, -8.06) * mm]});
            skLineSegment(sketch, "E487", {"start": v(-2.84, -8.06) * mm, "end": v(-2.84, -8.06) * mm});
            skFitSpline(sketch, "E488", {"points": [v(-3.11, -8.03) * mm, v(-3.24, -8) * mm, v(-3.45, -7.93) * mm, v(-3.52, -7.88) * mm]});
            skFitSpline(sketch, "E489", {"points": [v(-3.52, -7.88) * mm, v(-3.57, -7.86) * mm, v(-3.59, -7.85) * mm, v(-3.21, -7.96) * mm]});
            skFitSpline(sketch, "E490", {"points": [v(-3.21, -7.96) * mm, v(-3.05, -8) * mm, v(-2.9, -8.04) * mm, v(-2.9, -8.05) * mm]});
            skFitSpline(sketch, "E491", {"points": [v(-2.9, -8.05) * mm, v(-2.8, -8.07) * mm, v(-3, -8.05) * mm, v(-3.11, -8.03) * mm]});
            skFitSpline(sketch, "E492", {"points": [v(-3.1, -7.85) * mm, v(-3.5, -7.78) * mm, v(-3.75, -7.66) * mm, v(-3.95, -7.43) * mm]});
            skFitSpline(sketch, "E493", {"points": [v(-3.95, -7.43) * mm, v(-4.05, -7.33) * mm, v(-4.12, -7.2) * mm, v(-4.15, -7.06) * mm]});
            skFitSpline(sketch, "E494", {"points": [v(-4.15, -7.06) * mm, v(-4.19, -6.84) * mm, v(-4.1, -6.73) * mm, v(-3.97, -6.82) * mm]});
            skFitSpline(sketch, "E495", {"points": [v(-3.97, -6.82) * mm, v(-3.92, -6.84) * mm, v(-3.88, -6.9) * mm, v(-3.79, -7.13) * mm]});
            skFitSpline(sketch, "E496", {"points": [v(-3.79, -7.13) * mm, v(-3.73, -7.26) * mm, v(-3.67, -7.3) * mm, v(-3.6, -7.28) * mm]});
            skFitSpline(sketch, "E497", {"points": [v(-3.6, -7.28) * mm, v(-3.57, -7.27) * mm, v(-3.57, -7.26) * mm, v(-3.59, -7.24) * mm]});
            skFitSpline(sketch, "E498", {"points": [v(-3.59, -7.24) * mm, v(-3.6, -7.22) * mm, v(-3.6, -7.22) * mm, v(-3.58, -7.23) * mm]});
            skFitSpline(sketch, "E499", {"points": [v(-3.58, -7.23) * mm, v(-3.53, -7.25) * mm, v(-3.2, -7.35) * mm, v(-3.11, -7.37) * mm]});
            skFitSpline(sketch, "E500", {"points": [v(-3.11, -7.37) * mm, v(-2.98, -7.4) * mm, v(-2.78, -7.41) * mm, v(-2.69, -7.4) * mm]});
            skFitSpline(sketch, "E501", {"points": [v(-2.69, -7.4) * mm, v(-2.6, -7.37) * mm, v(-2.5, -7.32) * mm, v(-2.45, -7.28) * mm]});
            skFitSpline(sketch, "E502", {"points": [v(-2.45, -7.28) * mm, v(-2.42, -7.24) * mm, v(-2.42, -7.12) * mm, v(-2.47, -7.03) * mm]});
            skFitSpline(sketch, "E503", {"points": [v(-2.47, -7.03) * mm, v(-2.54, -6.88) * mm, v(-2.66, -6.83) * mm, v(-3.08, -6.74) * mm]});
            skFitSpline(sketch, "E504", {"points": [v(-3.08, -6.74) * mm, v(-3.46, -6.66) * mm, v(-3.54, -6.64) * mm, v(-3.69, -6.57) * mm]});
            skFitSpline(sketch, "E505", {"points": [v(-3.69, -6.57) * mm, v(-3.83, -6.5) * mm, v(-3.97, -6.37) * mm, v(-4.04, -6.26) * mm]});
            skLineSegment(sketch, "E506", {"start": v(-4.04, -6.26) * mm, "end": v(-4.07, -6.2) * mm});
            skLineSegment(sketch, "E507", {"start": v(-4.07, -6.2) * mm, "end": v(-4.03, -6.2) * mm});
            skFitSpline(sketch, "E508", {"points": [v(-4.03, -6.2) * mm, v(-4, -6.21) * mm, v(-3.99, -6.2) * mm, v(-4, -6.17) * mm]});
            skFitSpline(sketch, "E509", {"points": [v(-4, -6.17) * mm, v(-4, -6.14) * mm, v(-4.04, -6.04) * mm, v(-4.07, -5.93) * mm]});
            skFitSpline(sketch, "E510", {"points": [v(-4.07, -5.93) * mm, v(-4.14, -5.75) * mm, v(-4.14, -5.71) * mm, v(-4.14, -5.6) * mm]});
            skFitSpline(sketch, "E511", {"points": [v(-4.14, -5.6) * mm, v(-4.14, -5.31) * mm, v(-4.04, -5.1) * mm, v(-3.86, -4.99) * mm]});
            skFitSpline(sketch, "E512", {"points": [v(-3.86, -4.99) * mm, v(-3.71, -4.9) * mm, v(-3.38, -4.87) * mm, v(-2.98, -4.93) * mm]});
            skFitSpline(sketch, "E513", {"points": [v(-2.98, -4.93) * mm, v(-2.46, -5) * mm, v(-2.16, -5.14) * mm, v(-2.03, -5.4) * mm]});
            skFitSpline(sketch, "E514", {"points": [v(-2.03, -5.4) * mm, v(-1.99, -5.5) * mm, v(-1.98, -5.51) * mm, v(-1.98, -5.66) * mm]});
            skFitSpline(sketch, "E515", {"points": [v(-1.98, -5.66) * mm, v(-1.98, -5.74) * mm, v(-1.99, -5.82) * mm, v(-2, -5.83) * mm]});
            skFitSpline(sketch, "E516", {"points": [v(-2, -5.83) * mm, v(-2, -5.83) * mm, v(-2.05, -5.85) * mm, v(-2.09, -5.86) * mm]});
            skFitSpline(sketch, "E517", {"points": [v(-2.09, -5.86) * mm, v(-2.16, -5.88) * mm, v(-2.16, -5.88) * mm, v(-2.2, -5.84) * mm]});
            skFitSpline(sketch, "E518", {"points": [v(-2.2, -5.84) * mm, v(-2.22, -5.8) * mm, v(-2.26, -5.73) * mm, v(-2.28, -5.65) * mm]});
            skFitSpline(sketch, "E519", {"points": [v(-2.28, -5.65) * mm, v(-2.32, -5.55) * mm, v(-2.34, -5.5) * mm, v(-2.38, -5.46) * mm]});
            skFitSpline(sketch, "E520", {"points": [v(-2.38, -5.46) * mm, v(-2.46, -5.39) * mm, v(-2.48, -5.39) * mm, v(-2.46, -5.45) * mm]});
            skFitSpline(sketch, "E521", {"points": [v(-2.46, -5.45) * mm, v(-2.41, -5.6) * mm, v(-2.38, -5.74) * mm, v(-2.39, -5.74) * mm]});
            skFitSpline(sketch, "E522", {"points": [v(-2.39, -5.74) * mm, v(-2.4, -5.75) * mm, v(-2.43, -5.73) * mm, v(-2.47, -5.7) * mm]});
            skFitSpline(sketch, "E523", {"points": [v(-2.47, -5.7) * mm, v(-2.58, -5.64) * mm, v(-2.74, -5.57) * mm, v(-2.9, -5.55) * mm]});
            skFitSpline(sketch, "E524", {"points": [v(-2.9, -5.55) * mm, v(-3.08, -5.51) * mm, v(-3.37, -5.52) * mm, v(-3.55, -5.57) * mm]});
            skFitSpline(sketch, "E525", {"points": [v(-3.55, -5.57) * mm, v(-3.62, -5.59) * mm, v(-3.68, -5.6) * mm, v(-3.68, -5.6) * mm]});
            skFitSpline(sketch, "E526", {"points": [v(-3.68, -5.6) * mm, v(-3.69, -5.6) * mm, v(-3.68, -5.53) * mm, v(-3.66, -5.47) * mm]});
            skFitSpline(sketch, "E527", {"points": [v(-3.66, -5.47) * mm, v(-3.63, -5.34) * mm, v(-3.62, -5.25) * mm, v(-3.64, -5.23) * mm]});
            skFitSpline(sketch, "E528", {"points": [v(-3.64, -5.23) * mm, v(-3.65, -5.22) * mm, v(-3.75, -5.26) * mm, v(-3.79, -5.3) * mm]});
            skFitSpline(sketch, "E529", {"points": [v(-3.79, -5.3) * mm, v(-3.84, -5.35) * mm, v(-3.87, -5.43) * mm, v(-3.87, -5.57) * mm]});
            skFitSpline(sketch, "E530", {"points": [v(-3.87, -5.57) * mm, v(-3.87, -5.8) * mm, v(-3.81, -5.92) * mm, v(-3.68, -5.99) * mm]});
            skFitSpline(sketch, "E531", {"points": [v(-3.68, -5.99) * mm, v(-3.6, -6.03) * mm, v(-3.53, -6.04) * mm, v(-3.47, -6) * mm]});
            skFitSpline(sketch, "E532", {"points": [v(-3.47, -6) * mm, v(-3.44, -6) * mm, v(-3.37, -6) * mm, v(-3.14, -6.05) * mm]});
            skFitSpline(sketch, "E533", {"points": [v(-3.14, -6.05) * mm, v(-2.83, -6.1) * mm, v(-2.45, -6.2) * mm, v(-2.38, -6.22) * mm]});
            skLineSegment(sketch, "E534", {"start": v(-2.38, -6.22) * mm, "end": v(-2.35, -6.24) * mm});
            skLineSegment(sketch, "E535", {"start": v(-2.35, -6.24) * mm, "end": v(-2.39, -6.23) * mm});
            skFitSpline(sketch, "E536", {"points": [v(-2.39, -6.23) * mm, v(-2.41, -6.23) * mm, v(-2.43, -6.23) * mm, v(-2.43, -6.23) * mm]});
            skFitSpline(sketch, "E537", {"points": [v(-2.43, -6.23) * mm, v(-2.43, -6.24) * mm, v(-2.4, -6.27) * mm, v(-2.35, -6.31) * mm]});
            skFitSpline(sketch, "E538", {"points": [v(-2.35, -6.31) * mm, v(-2.12, -6.51) * mm, v(-2.04, -6.65) * mm, v(-1.99, -6.88) * mm]});
            skFitSpline(sketch, "E539", {"points": [v(-1.99, -6.88) * mm, v(-1.92, -7.22) * mm, v(-1.97, -7.51) * mm, v(-2.14, -7.68) * mm]});
            skFitSpline(sketch, "E540", {"points": [v(-2.14, -7.68) * mm, v(-2.23, -7.77) * mm, v(-2.3, -7.8) * mm, v(-2.46, -7.85) * mm]});
            skFitSpline(sketch, "E541", {"points": [v(-2.46, -7.85) * mm, v(-2.6, -7.89) * mm, v(-2.9, -7.89) * mm, v(-3.1, -7.85) * mm]});
            skLineSegment(sketch, "E542", {"start": v(-3.1, -7.85) * mm, "end": v(-3.1, -7.85) * mm});
            skFitSpline(sketch, "E543", {"points": [v(-2.28, -7.13) * mm, v(-2.29, -7.12) * mm, v(-2.3, -7.13) * mm, v(-2.3, -7.15) * mm]});
            skFitSpline(sketch, "E544", {"points": [v(-2.3, -7.15) * mm, v(-2.3, -7.17) * mm, v(-2.29, -7.18) * mm, v(-2.28, -7.17) * mm]});
            skFitSpline(sketch, "E545", {"points": [v(-2.28, -7.17) * mm, v(-2.28, -7.16) * mm, v(-2.28, -7.14) * mm, v(-2.28, -7.13) * mm]});
            skLineSegment(sketch, "E546", {"start": v(-2.3, -6.86) * mm, "end": v(-2.32, -6.8) * mm});
            skLineSegment(sketch, "E547", {"start": v(-2.32, -6.8) * mm, "end": v(-2.32, -6.85) * mm});
            skFitSpline(sketch, "E548", {"points": [v(-2.32, -6.85) * mm, v(-2.32, -6.9) * mm, v(-2.3, -6.99) * mm, v(-2.28, -7.04) * mm]});
            skFitSpline(sketch, "E549", {"points": [v(-2.28, -7.04) * mm, v(-2.28, -7.05) * mm, v(-2.27, -7.03) * mm, v(-2.27, -7) * mm]});
            skFitSpline(sketch, "E550", {"points": [v(-2.27, -7) * mm, v(-2.26, -6.94) * mm, v(-2.27, -6.9) * mm, v(-2.3, -6.86) * mm]});
            skFitSpline(sketch, "E551", {"points": [v(-2.82, -6.61) * mm, v(-2.82, -6.6) * mm, v(-2.9, -6.58) * mm, v(-2.99, -6.56) * mm]});
            skFitSpline(sketch, "E552", {"points": [v(-2.99, -6.56) * mm, v(-3.17, -6.5) * mm, v(-3.6, -6.42) * mm, v(-3.59, -6.44) * mm]});
            skFitSpline(sketch, "E553", {"points": [v(-3.59, -6.44) * mm, v(-3.56, -6.48) * mm, v(-2.82, -6.65) * mm, v(-2.82, -6.61) * mm]});
            skFitSpline(sketch, "E554", {"points": [v(1.55, -7.83) * mm, v(1.42, -7.78) * mm, v(1.35, -7.73) * mm, v(1.28, -7.63) * mm]});
            skFitSpline(sketch, "E555", {"points": [v(1.28, -7.63) * mm, v(1.2, -7.52) * mm, v(1.19, -7.44) * mm, v(1.16, -7.18) * mm]});
            skFitSpline(sketch, "E556", {"points": [v(1.16, -7.18) * mm, v(1.1, -6.52) * mm, v(1.07, -5.81) * mm, v(1.11, -5.63) * mm]});
            skFitSpline(sketch, "E557", {"points": [v(1.11, -5.63) * mm, v(1.17, -5.41) * mm, v(1.31, -5.2) * mm, v(1.5, -5.1) * mm]});
            skFitSpline(sketch, "E558", {"points": [v(1.5, -5.1) * mm, v(1.7, -4.98) * mm, v(2.06, -4.9) * mm, v(2.43, -4.88) * mm]});
            skFitSpline(sketch, "E559", {"points": [v(2.43, -4.88) * mm, v(2.75, -4.86) * mm, v(2.96, -4.92) * mm, v(3.12, -5.06) * mm]});
            skFitSpline(sketch, "E560", {"points": [v(3.12, -5.06) * mm, v(3.3, -5.22) * mm, v(3.37, -5.52) * mm, v(3.37, -6.22) * mm]});
            skFitSpline(sketch, "E561", {"points": [v(3.37, -6.22) * mm, v(3.37, -6.53) * mm, v(3.37, -6.64) * mm, v(3.35, -6.77) * mm]});
            skFitSpline(sketch, "E562", {"points": [v(3.35, -6.77) * mm, v(3.28, -7.15) * mm, v(3.18, -7.35) * mm, v(2.94, -7.51) * mm]});
            skFitSpline(sketch, "E563", {"points": [v(2.94, -7.51) * mm, v(2.69, -7.7) * mm, v(2.2, -7.84) * mm, v(1.82, -7.86) * mm]});
            skFitSpline(sketch, "E564", {"points": [v(1.82, -7.86) * mm, v(1.66, -7.86) * mm, v(1.63, -7.86) * mm, v(1.55, -7.83) * mm]});
            skFitSpline(sketch, "E565", {"points": [v(1.96, -7.45) * mm, v(2.2, -7.42) * mm, v(2.28, -7.4) * mm, v(2.43, -7.35) * mm]});
            skFitSpline(sketch, "E566", {"points": [v(2.43, -7.35) * mm, v(2.64, -7.28) * mm, v(2.79, -7.16) * mm, v(2.86, -7) * mm]});
            skFitSpline(sketch, "E567", {"points": [v(2.86, -7) * mm, v(2.93, -6.85) * mm, v(2.95, -6.74) * mm, v(2.95, -6.4) * mm]});
            skFitSpline(sketch, "E568", {"points": [v(2.95, -6.4) * mm, v(2.95, -6.05) * mm, v(2.93, -5.9) * mm, v(2.86, -5.7) * mm]});
            skFitSpline(sketch, "E569", {"points": [v(2.86, -5.7) * mm, v(2.8, -5.52) * mm, v(2.79, -5.5) * mm, v(2.7, -5.49) * mm]});
            skFitSpline(sketch, "E570", {"points": [v(2.7, -5.49) * mm, v(2.58, -5.47) * mm, v(2.3, -5.5) * mm, v(2.01, -5.55) * mm]});
            skFitSpline(sketch, "E571", {"points": [v(2.01, -5.55) * mm, v(1.74, -5.6) * mm, v(1.64, -5.61) * mm, v(1.64, -5.6) * mm]});
            skFitSpline(sketch, "E572", {"points": [v(1.64, -5.6) * mm, v(1.64, -5.57) * mm, v(1.69, -5.48) * mm, v(1.72, -5.45) * mm]});
            skFitSpline(sketch, "E573", {"points": [v(1.72, -5.45) * mm, v(1.78, -5.38) * mm, v(1.83, -5.37) * mm, v(2.04, -5.37) * mm]});
            skFitSpline(sketch, "E574", {"points": [v(2.04, -5.37) * mm, v(2.2, -5.36) * mm, v(2.25, -5.36) * mm, v(2.3, -5.33) * mm]});
            skLineSegment(sketch, "E575", {"start": v(2.3, -5.33) * mm, "end": v(2.37, -5.3) * mm});
            skLineSegment(sketch, "E576", {"start": v(2.37, -5.3) * mm, "end": v(2.12, -5.3) * mm});
            skFitSpline(sketch, "E577", {"points": [v(2.12, -5.3) * mm, v(1.84, -5.3) * mm, v(1.73, -5.32) * mm, v(1.62, -5.4) * mm]});
            skFitSpline(sketch, "E578", {"points": [v(1.62, -5.4) * mm, v(1.42, -5.55) * mm, v(1.36, -5.76) * mm, v(1.36, -6.31) * mm]});
            skFitSpline(sketch, "E579", {"points": [v(1.36, -6.31) * mm, v(1.37, -6.73) * mm, v(1.41, -7.02) * mm, v(1.52, -7.23) * mm]});
            skFitSpline(sketch, "E580", {"points": [v(1.52, -7.23) * mm, v(1.57, -7.34) * mm, v(1.7, -7.48) * mm, v(1.73, -7.48) * mm]});
            skFitSpline(sketch, "E581", {"points": [v(1.73, -7.48) * mm, v(1.74, -7.48) * mm, v(1.84, -7.47) * mm, v(1.96, -7.45) * mm]});
            skLineSegment(sketch, "E582", {"start": v(1.96, -7.45) * mm, "end": v(1.96, -7.45) * mm});
            skFitSpline(sketch, "E583", {"points": [v(3.02, -6.84) * mm, v(3.09, -6.6) * mm, v(3.1, -6.46) * mm, v(3.1, -6.1) * mm]});
            skFitSpline(sketch, "E584", {"points": [v(3.1, -6.1) * mm, v(3.09, -5.87) * mm, v(3.07, -5.72) * mm, v(3.06, -5.65) * mm]});
            skFitSpline(sketch, "E585", {"points": [v(3.06, -5.65) * mm, v(3.02, -5.5) * mm, v(2.95, -5.34) * mm, v(2.88, -5.3) * mm]});
            skFitSpline(sketch, "E586", {"points": [v(2.88, -5.3) * mm, v(2.8, -5.24) * mm, v(2.79, -5.26) * mm, v(2.84, -5.37) * mm]});
            skFitSpline(sketch, "E587", {"points": [v(2.84, -5.37) * mm, v(2.91, -5.51) * mm, v(2.96, -5.67) * mm, v(3, -5.85) * mm]});
            skFitSpline(sketch, "E588", {"points": [v(3, -5.85) * mm, v(3.05, -6.12) * mm, v(3.03, -6.58) * mm, v(2.96, -6.99) * mm]});
            skFitSpline(sketch, "E589", {"points": [v(2.96, -6.99) * mm, v(2.95, -7.08) * mm, v(2.99, -7) * mm, v(3.02, -6.84) * mm]});
            skFitSpline(sketch, "E590", {"points": [v(8.1, -7.66) * mm, v(8.07, -7.64) * mm, v(7.93, -7.48) * mm, v(7.78, -7.31) * mm]});
            skFitSpline(sketch, "E591", {"points": [v(7.78, -7.31) * mm, v(7.63, -7.14) * mm, v(7.49, -6.98) * mm, v(7.46, -6.95) * mm]});
            skFitSpline(sketch, "E592", {"points": [v(7.46, -6.95) * mm, v(7.43, -6.92) * mm, v(7.4, -6.88) * mm, v(7.4, -6.87) * mm]});
            skFitSpline(sketch, "E593", {"points": [v(7.4, -6.87) * mm, v(7.4, -6.8) * mm, v(7.53, -6.65) * mm, v(7.76, -6.42) * mm]});
            skFitSpline(sketch, "E594", {"points": [v(7.76, -6.42) * mm, v(7.92, -6.27) * mm, v(8.03, -6.17) * mm, v(8.09, -6.14) * mm]});
            skFitSpline(sketch, "E595", {"points": [v(8.09, -6.14) * mm, v(8.13, -6.12) * mm, v(8.17, -6.1) * mm, v(8.17, -6.1) * mm]});
            skFitSpline(sketch, "E596", {"points": [v(8.17, -6.1) * mm, v(8.17, -6.1) * mm, v(8.18, -6.13) * mm, v(8.18, -6.15) * mm]});
            skFitSpline(sketch, "E597", {"points": [v(8.18, -6.15) * mm, v(8.2, -6.18) * mm, v(8.19, -6.2) * mm, v(8.16, -6.22) * mm]});
            skFitSpline(sketch, "E598", {"points": [v(8.16, -6.22) * mm, v(8.12, -6.25) * mm, v(8.13, -6.28) * mm, v(8.17, -6.3) * mm]});
            skFitSpline(sketch, "E599", {"points": [v(8.17, -6.3) * mm, v(8.2, -6.3) * mm, v(8.2, -6.31) * mm, v(8.13, -6.4) * mm]});
            skFitSpline(sketch, "E600", {"points": [v(8.13, -6.4) * mm, v(8.1, -6.45) * mm, v(7.99, -6.56) * mm, v(7.9, -6.65) * mm]});
            skFitSpline(sketch, "E601", {"points": [v(7.9, -6.65) * mm, v(7.8, -6.74) * mm, v(7.74, -6.82) * mm, v(7.74, -6.84) * mm]});
            skFitSpline(sketch, "E602", {"points": [v(7.74, -6.84) * mm, v(7.74, -6.85) * mm, v(7.76, -6.9) * mm, v(7.8, -6.93) * mm]});
            skFitSpline(sketch, "E603", {"points": [v(7.8, -6.93) * mm, v(7.83, -6.96) * mm, v(7.84, -6.98) * mm, v(7.82, -6.97) * mm]});
            skFitSpline(sketch, "E604", {"points": [v(7.82, -6.97) * mm, v(7.8, -6.96) * mm, v(7.76, -6.92) * mm, v(7.72, -6.88) * mm]});
            skFitSpline(sketch, "E605", {"points": [v(7.72, -6.88) * mm, v(7.68, -6.83) * mm, v(7.64, -6.8) * mm, v(7.63, -6.8) * mm]});
            skFitSpline(sketch, "E606", {"points": [v(7.63, -6.8) * mm, v(7.62, -6.8) * mm, v(7.64, -6.89) * mm, v(7.66, -6.94) * mm]});
            skFitSpline(sketch, "E607", {"points": [v(7.66, -6.94) * mm, v(7.7, -7) * mm, v(7.79, -7.09) * mm, v(7.82, -7.09) * mm]});
            skFitSpline(sketch, "E608", {"points": [v(7.82, -7.09) * mm, v(7.84, -7.09) * mm, v(7.9, -7.04) * mm, v(7.9, -7.02) * mm]});
            skFitSpline(sketch, "E609", {"points": [v(7.9, -7.02) * mm, v(7.9, -7) * mm, v(7.88, -7) * mm, v(7.87, -7) * mm]});
            skFitSpline(sketch, "E610", {"points": [v(7.87, -7) * mm, v(7.86, -6.99) * mm, v(7.87, -6.97) * mm, v(7.9, -6.94) * mm]});
            skFitSpline(sketch, "E611", {"points": [v(7.9, -6.94) * mm, v(7.93, -6.92) * mm, v(8.02, -6.85) * mm, v(8.09, -6.79) * mm]});
            skFitSpline(sketch, "E612", {"points": [v(8.09, -6.79) * mm, v(8.35, -6.57) * mm, v(8.55, -6.53) * mm, v(8.44, -6.72) * mm]});
            skFitSpline(sketch, "E613", {"points": [v(8.44, -6.72) * mm, v(8.41, -6.76) * mm, v(8.4, -6.77) * mm, v(8.43, -6.76) * mm]});
            skFitSpline(sketch, "E614", {"points": [v(8.43, -6.76) * mm, v(8.47, -6.75) * mm, v(8.44, -6.79) * mm, v(8.28, -7) * mm]});
            skFitSpline(sketch, "E615", {"points": [v(8.28, -7) * mm, v(8.2, -7.09) * mm, v(8.13, -7.18) * mm, v(8.13, -7.2) * mm]});
            skFitSpline(sketch, "E616", {"points": [v(8.13, -7.2) * mm, v(8.13, -7.24) * mm, v(8.19, -7.33) * mm, v(8.22, -7.34) * mm]});
            skFitSpline(sketch, "E617", {"points": [v(8.22, -7.34) * mm, v(8.26, -7.36) * mm, v(8.36, -7.28) * mm, v(8.56, -7.07) * mm]});
            skFitSpline(sketch, "E618", {"points": [v(8.56, -7.07) * mm, v(8.67, -6.96) * mm, v(8.75, -6.88) * mm, v(8.74, -6.9) * mm]});
            skFitSpline(sketch, "E619", {"points": [v(8.74, -6.9) * mm, v(8.72, -6.95) * mm, v(8.73, -6.95) * mm, v(8.82, -6.87) * mm]});
            skFitSpline(sketch, "E620", {"points": [v(8.82, -6.87) * mm, v(8.93, -6.79) * mm, v(8.98, -6.77) * mm, v(9, -6.8) * mm]});
            skFitSpline(sketch, "E621", {"points": [v(9, -6.8) * mm, v(9.02, -6.82) * mm, v(9.03, -6.84) * mm, v(9.03, -6.85) * mm]});
            skFitSpline(sketch, "E622", {"points": [v(9.03, -6.85) * mm, v(9.03, -6.89) * mm, v(8.31, -7.63) * mm, v(8.24, -7.67) * mm]});
            skFitSpline(sketch, "E623", {"points": [v(8.24, -7.67) * mm, v(8.18, -7.7) * mm, v(8.16, -7.7) * mm, v(8.1, -7.66) * mm]});
            skFitSpline(sketch, "E624", {"points": [v(8.25, -7.44) * mm, v(8.27, -7.43) * mm, v(8.25, -7.4) * mm, v(8.14, -7.3) * mm]});
            skFitSpline(sketch, "E625", {"points": [v(8.14, -7.3) * mm, v(8.02, -7.18) * mm, v(8, -7.17) * mm, v(7.99, -7.2) * mm]});
            skFitSpline(sketch, "E626", {"points": [v(7.99, -7.2) * mm, v(7.95, -7.23) * mm, v(7.96, -7.27) * mm, v(8.05, -7.36) * mm]});
            skFitSpline(sketch, "E627", {"points": [v(8.05, -7.36) * mm, v(8.12, -7.44) * mm, v(8.15, -7.45) * mm, v(8.18, -7.45) * mm]});
            skFitSpline(sketch, "E628", {"points": [v(8.18, -7.45) * mm, v(8.21, -7.45) * mm, v(8.24, -7.45) * mm, v(8.25, -7.44) * mm]});
            skFitSpline(sketch, "E629", {"points": [v(8.62, -7.38) * mm, v(8.68, -7.32) * mm, v(8.75, -7.25) * mm, v(8.77, -7.23) * mm]});
            skFitSpline(sketch, "E630", {"points": [v(8.77, -7.23) * mm, v(8.79, -7.2) * mm, v(8.8, -7.2) * mm, v(8.8, -7.2) * mm]});
            skFitSpline(sketch, "E631", {"points": [v(8.8, -7.2) * mm, v(8.8, -7.22) * mm, v(8.66, -7.37) * mm, v(8.57, -7.45) * mm]});
            skFitSpline(sketch, "E632", {"points": [v(8.57, -7.45) * mm, v(8.53, -7.48) * mm, v(8.56, -7.45) * mm, v(8.62, -7.38) * mm]});
            skFitSpline(sketch, "E633", {"points": [v(4.74, -5.85) * mm, v(4.4, -5.78) * mm, v(4.16, -5.63) * mm, v(3.97, -5.38) * mm]});
            skFitSpline(sketch, "E634", {"points": [v(3.97, -5.38) * mm, v(3.85, -5.2) * mm, v(3.79, -5.08) * mm, v(3.68, -4.72) * mm]});
            skFitSpline(sketch, "E635", {"points": [v(3.68, -4.72) * mm, v(3.56, -4.36) * mm, v(3.45, -4.09) * mm, v(3.31, -3.9) * mm]});
            skFitSpline(sketch, "E636", {"points": [v(3.31, -3.9) * mm, v(3.27, -3.83) * mm, v(3.2, -3.73) * mm, v(3.17, -3.69) * mm]});
            skFitSpline(sketch, "E637", {"points": [v(3.17, -3.69) * mm, v(3.14, -3.64) * mm, v(2.97, -3.44) * mm, v(2.8, -3.24) * mm]});
            skFitSpline(sketch, "E638", {"points": [v(2.8, -3.24) * mm, v(2.63, -3.04) * mm, v(2.49, -2.87) * mm, v(2.49, -2.87) * mm]});
            skFitSpline(sketch, "E639", {"points": [v(2.49, -2.87) * mm, v(2.49, -2.86) * mm, v(2.52, -2.83) * mm, v(2.56, -2.8) * mm]});
            skFitSpline(sketch, "E640", {"points": [v(2.56, -2.8) * mm, v(2.65, -2.72) * mm, v(2.82, -2.52) * mm, v(2.9, -2.4) * mm]});
            skFitSpline(sketch, "E641", {"points": [v(2.9, -2.4) * mm, v(3, -2.27) * mm, v(3.08, -2.1) * mm, v(3.13, -1.94) * mm]});
            skFitSpline(sketch, "E642", {"points": [v(3.13, -1.94) * mm, v(3.16, -1.86) * mm, v(3.19, -1.8) * mm, v(3.19, -1.8) * mm]});
            skFitSpline(sketch, "E643", {"points": [v(3.19, -1.8) * mm, v(3.2, -1.8) * mm, v(3.23, -1.84) * mm, v(3.27, -1.88) * mm]});
            skFitSpline(sketch, "E644", {"points": [v(3.27, -1.88) * mm, v(3.3, -1.93) * mm, v(3.48, -2.1) * mm, v(3.65, -2.28) * mm]});
            skFitSpline(sketch, "E645", {"points": [v(3.65, -2.28) * mm, v(3.9, -2.54) * mm, v(4.01, -2.65) * mm, v(4.29, -2.87) * mm]});
            skFitSpline(sketch, "E646", {"points": [v(4.29, -2.87) * mm, v(4.47, -3.01) * mm, v(4.66, -3.16) * mm, v(4.72, -3.2) * mm]});
            skFitSpline(sketch, "E647", {"points": [v(4.72, -3.2) * mm, v(4.77, -3.24) * mm, v(4.98, -3.35) * mm, v(5.19, -3.45) * mm]});
            skFitSpline(sketch, "E648", {"points": [v(5.19, -3.45) * mm, v(5.58, -3.64) * mm, v(5.68, -3.7) * mm, v(5.81, -3.86) * mm]});
            skFitSpline(sketch, "E649", {"points": [v(5.81, -3.86) * mm, v(6.17, -4.27) * mm, v(6.22, -4.83) * mm, v(5.94, -5.3) * mm]});
            skFitSpline(sketch, "E650", {"points": [v(5.94, -5.3) * mm, v(5.85, -5.45) * mm, v(5.76, -5.54) * mm, v(5.6, -5.65) * mm]});
            skFitSpline(sketch, "E651", {"points": [v(5.6, -5.65) * mm, v(5.31, -5.84) * mm, v(5, -5.9) * mm, v(4.74, -5.85) * mm]});
            skFitSpline(sketch, "E652", {"points": [v(4.85, -5.46) * mm, v(4.93, -5.45) * mm, v(4.96, -5.45) * mm, v(5.01, -5.46) * mm]});
            skFitSpline(sketch, "E653", {"points": [v(5.01, -5.46) * mm, v(5.11, -5.5) * mm, v(5.16, -5.5) * mm, v(5.16, -5.48) * mm]});
            skFitSpline(sketch, "E654", {"points": [v(5.16, -5.48) * mm, v(5.16, -5.48) * mm, v(5.18, -5.44) * mm, v(5.21, -5.4) * mm]});
            skFitSpline(sketch, "E655", {"points": [v(5.21, -5.4) * mm, v(5.25, -5.36) * mm, v(5.29, -5.34) * mm, v(5.37, -5.31) * mm]});
            skFitSpline(sketch, "E656", {"points": [v(5.37, -5.31) * mm, v(5.5, -5.28) * mm, v(5.52, -5.25) * mm, v(5.54, -5.15) * mm]});
            skFitSpline(sketch, "E657", {"points": [v(5.54, -5.15) * mm, v(5.56, -5.05) * mm, v(5.58, -5) * mm, v(5.65, -4.94) * mm]});
            skFitSpline(sketch, "E658", {"points": [v(5.65, -4.94) * mm, v(5.72, -4.9) * mm, v(5.73, -4.83) * mm, v(5.7, -4.72) * mm]});
            skFitSpline(sketch, "E659", {"points": [v(5.7, -4.72) * mm, v(5.67, -4.64) * mm, v(5.67, -4.57) * mm, v(5.7, -4.46) * mm]});
            skFitSpline(sketch, "E660", {"points": [v(5.7, -4.46) * mm, v(5.72, -4.4) * mm, v(5.7, -4.37) * mm, v(5.61, -4.28) * mm]});
            skFitSpline(sketch, "E661", {"points": [v(5.61, -4.28) * mm, v(5.55, -4.22) * mm, v(5.5, -4.14) * mm, v(5.5, -4.06) * mm]});
            skFitSpline(sketch, "E662", {"points": [v(5.5, -4.06) * mm, v(5.5, -4) * mm, v(5.44, -3.96) * mm, v(5.35, -3.95) * mm]});
            skFitSpline(sketch, "E663", {"points": [v(5.35, -3.95) * mm, v(5.27, -3.94) * mm, v(5.26, -3.93) * mm, v(5.17, -3.85) * mm]});
            skLineSegment(sketch, "E664", {"start": v(5.17, -3.85) * mm, "end": v(5.08, -3.76) * mm});
            skLineSegment(sketch, "E665", {"start": v(5.08, -3.76) * mm, "end": v(5, -3.8) * mm});
            skFitSpline(sketch, "E666", {"points": [v(5, -3.8) * mm, v(4.9, -3.83) * mm, v(4.8, -3.83) * mm, v(4.74, -3.79) * mm]});
            skFitSpline(sketch, "E667", {"points": [v(4.74, -3.79) * mm, v(4.7, -3.76) * mm, v(4.66, -3.77) * mm, v(4.58, -3.86) * mm]});
            skFitSpline(sketch, "E668", {"points": [v(4.58, -3.86) * mm, v(4.53, -3.91) * mm, v(4.5, -3.93) * mm, v(4.42, -3.96) * mm]});
            skFitSpline(sketch, "E669", {"points": [v(4.42, -3.96) * mm, v(4.37, -3.97) * mm, v(4.32, -4) * mm, v(4.3, -4) * mm]});
            skFitSpline(sketch, "E670", {"points": [v(4.3, -4) * mm, v(4.29, -4) * mm, v(4.27, -4.06) * mm, v(4.26, -4.12) * mm]});
            skFitSpline(sketch, "E671", {"points": [v(4.26, -4.12) * mm, v(4.24, -4.22) * mm, v(4.23, -4.23) * mm, v(4.16, -4.3) * mm]});
            skFitSpline(sketch, "E672", {"points": [v(4.16, -4.3) * mm, v(4.12, -4.34) * mm, v(4.08, -4.38) * mm, v(4.08, -4.4) * mm]});
            skFitSpline(sketch, "E673", {"points": [v(4.08, -4.4) * mm, v(4.08, -4.42) * mm, v(4.1, -4.48) * mm, v(4.1, -4.54) * mm]});
            skFitSpline(sketch, "E674", {"points": [v(4.1, -4.54) * mm, v(4.13, -4.64) * mm, v(4.13, -4.65) * mm, v(4.1, -4.73) * mm]});
            skFitSpline(sketch, "E675", {"points": [v(4.1, -4.73) * mm, v(4.07, -4.83) * mm, v(4.1, -4.91) * mm, v(4.16, -4.96) * mm]});
            skFitSpline(sketch, "E676", {"points": [v(4.16, -4.96) * mm, v(4.21, -4.99) * mm, v(4.25, -5.05) * mm, v(4.29, -5.18) * mm]});
            skFitSpline(sketch, "E677", {"points": [v(4.29, -5.18) * mm, v(4.3, -5.23) * mm, v(4.32, -5.27) * mm, v(4.33, -5.28) * mm]});
            skFitSpline(sketch, "E678", {"points": [v(4.33, -5.28) * mm, v(4.34, -5.29) * mm, v(4.4, -5.3) * mm, v(4.45, -5.32) * mm]});
            skFitSpline(sketch, "E679", {"points": [v(4.45, -5.32) * mm, v(4.54, -5.34) * mm, v(4.57, -5.35) * mm, v(4.6, -5.4) * mm]});
            skFitSpline(sketch, "E680", {"points": [v(4.6, -5.4) * mm, v(4.66, -5.48) * mm, v(4.69, -5.5) * mm, v(4.72, -5.5) * mm]});
            skFitSpline(sketch, "E681", {"points": [v(4.72, -5.5) * mm, v(4.74, -5.49) * mm, v(4.8, -5.47) * mm, v(4.85, -5.46) * mm]});
            skLineSegment(sketch, "E682", {"start": v(4.85, -5.46) * mm, "end": v(4.85, -5.46) * mm});
            skFitSpline(sketch, "E683", {"points": [v(-1.53, -3.13) * mm, v(-2, -3.05) * mm, v(-2.42, -2.82) * mm, v(-2.73, -2.47) * mm]});
            skFitSpline(sketch, "E684", {"points": [v(-2.73, -2.47) * mm, v(-3.05, -2.1) * mm, v(-3.21, -1.71) * mm, v(-3.25, -1.21) * mm]});
            skFitSpline(sketch, "E685", {"points": [v(-3.25, -1.21) * mm, v(-3.26, -1.07) * mm, v(-3.26, -0.1) * mm, v(-3.26, 1.65) * mm]});
            skFitSpline(sketch, "E686", {"points": [v(-3.26, 1.65) * mm, v(-3.25, 4.56) * mm, v(-3.26, 4.37) * mm, v(-3.16, 4.69) * mm]});
            skFitSpline(sketch, "E687", {"points": [v(-3.16, 4.69) * mm, v(-2.94, 5.41) * mm, v(-2.3, 5.98) * mm, v(-1.55, 6.1) * mm]});
            skFitSpline(sketch, "E688", {"points": [v(-1.55, 6.1) * mm, v(-1.43, 6.13) * mm, v(-1.23, 6.13) * mm, v(-0.09, 6.13) * mm]});
            skFitSpline(sketch, "E689", {"points": [v(-0.09, 6.13) * mm, v(1.38, 6.13) * mm, v(1.39, 6.13) * mm, v(1.68, 6.03) * mm]});
            skFitSpline(sketch, "E690", {"points": [v(1.68, 6.03) * mm, v(2.4, 5.8) * mm, v(2.92, 5.19) * mm, v(3.06, 4.44) * mm]});
            skFitSpline(sketch, "E691", {"points": [v(3.06, 4.44) * mm, v(3.09, 4.31) * mm, v(3.09, 4.1) * mm, v(3.09, 1.48) * mm]});
            skLineSegment(sketch, "E692", {"start": v(3.09, 1.48) * mm, "end": v(3.09, -1.34) * mm});
            skLineSegment(sketch, "E693", {"start": v(3.09, -1.34) * mm, "end": v(3.05, -1.5) * mm});
            skFitSpline(sketch, "E694", {"points": [v(3.05, -1.5) * mm, v(2.88, -2.26) * mm, v(2.38, -2.82) * mm, v(1.66, -3.06) * mm]});
            skFitSpline(sketch, "E695", {"points": [v(1.66, -3.06) * mm, v(1.36, -3.16) * mm, v(1.34, -3.16) * mm, v(-0.1, -3.16) * mm]});
            skFitSpline(sketch, "E696", {"points": [v(-0.1, -3.16) * mm, v(-1.12, -3.15) * mm, v(-1.43, -3.15) * mm, v(-1.53, -3.13) * mm]});
            skLineSegment(sketch, "E697", {"start": v(1.84, 2.57) * mm, "end": v(1.84, 3.66) * mm});
            skLineSegment(sketch, "E698", {"start": v(1.84, 3.66) * mm, "end": v(-0.07, 3.66) * mm});
            skLineSegment(sketch, "E699", {"start": v(-0.07, 3.66) * mm, "end": v(-1.97, 3.66) * mm});
            skLineSegment(sketch, "E700", {"start": v(-1.97, 3.66) * mm, "end": v(-1.97, 2.57) * mm});
            skLineSegment(sketch, "E701", {"start": v(-1.97, 2.57) * mm, "end": v(-1.97, 1.49) * mm});
            skLineSegment(sketch, "E702", {"start": v(-1.97, 1.49) * mm, "end": v(-0.07, 1.49) * mm});
            skLineSegment(sketch, "E703", {"start": v(-0.07, 1.49) * mm, "end": v(1.84, 1.49) * mm});
            skLineSegment(sketch, "E704", {"start": v(1.84, 1.49) * mm, "end": v(1.84, 2.57) * mm});
            skFitSpline(sketch, "E705", {"points": [v(-8.62, -2.93) * mm, v(-8.66, -2.9) * mm, v(-8.91, -2.48) * mm, v(-8.98, -2.32) * mm]});
            skFitSpline(sketch, "E706", {"points": [v(-8.98, -2.32) * mm, v(-9.09, -2.07) * mm, v(-9.08, -1.89) * mm, v(-8.97, -1.78) * mm]});
            skFitSpline(sketch, "E707", {"points": [v(-8.97, -1.78) * mm, v(-8.94, -1.75) * mm, v(-8.9, -1.73) * mm, v(-8.9, -1.73) * mm]});
            skFitSpline(sketch, "E708", {"points": [v(-8.9, -1.73) * mm, v(-8.9, -1.73) * mm, v(-8.82, -1.72) * mm, v(-8.74, -1.7) * mm]});
            skFitSpline(sketch, "E709", {"points": [v(-8.74, -1.7) * mm, v(-8.57, -1.68) * mm, v(-8.52, -1.65) * mm, v(-8.48, -1.56) * mm]});
            skFitSpline(sketch, "E710", {"points": [v(-8.48, -1.56) * mm, v(-8.45, -1.48) * mm, v(-8.35, -1.44) * mm, v(-8.23, -1.44) * mm]});
            skFitSpline(sketch, "E711", {"points": [v(-8.23, -1.44) * mm, v(-8.12, -1.45) * mm, v(-8.03, -1.51) * mm, v(-7.95, -1.63) * mm]});
            skFitSpline(sketch, "E712", {"points": [v(-7.95, -1.63) * mm, v(-7.91, -1.68) * mm, v(-7.88, -1.71) * mm, v(-7.88, -1.7) * mm]});
            skFitSpline(sketch, "E713", {"points": [v(-7.88, -1.7) * mm, v(-7.87, -1.7) * mm, v(-7.9, -1.6) * mm, v(-7.93, -1.55) * mm]});
            skFitSpline(sketch, "E714", {"points": [v(-7.93, -1.55) * mm, v(-7.95, -1.53) * mm, v(-7.95, -1.51) * mm, v(-7.95, -1.5) * mm]});
            skFitSpline(sketch, "E715", {"points": [v(-7.95, -1.5) * mm, v(-7.93, -1.5) * mm, v(-7.84, -1.66) * mm, v(-7.74, -1.9) * mm]});
            skFitSpline(sketch, "E716", {"points": [v(-7.74, -1.9) * mm, v(-7.68, -2.04) * mm, v(-7.64, -2.16) * mm, v(-7.64, -2.17) * mm]});
            skFitSpline(sketch, "E717", {"points": [v(-7.64, -2.17) * mm, v(-7.64, -2.17) * mm, v(-7.65, -2.17) * mm, v(-7.66, -2.15) * mm]});
            skFitSpline(sketch, "E718", {"points": [v(-7.66, -2.15) * mm, v(-7.68, -2.14) * mm, v(-7.67, -2.16) * mm, v(-7.64, -2.22) * mm]});
            skFitSpline(sketch, "E719", {"points": [v(-7.64, -2.22) * mm, v(-7.62, -2.28) * mm, v(-7.6, -2.33) * mm, v(-7.6, -2.37) * mm]});
            skFitSpline(sketch, "E720", {"points": [v(-7.6, -2.37) * mm, v(-7.61, -2.42) * mm, v(-7.62, -2.42) * mm, v(-8.1, -2.68) * mm]});
            skFitSpline(sketch, "E721", {"points": [v(-8.1, -2.68) * mm, v(-8.35, -2.83) * mm, v(-8.57, -2.94) * mm, v(-8.58, -2.94) * mm]});
            skFitSpline(sketch, "E722", {"points": [v(-8.58, -2.94) * mm, v(-8.58, -2.94) * mm, v(-8.6, -2.94) * mm, v(-8.62, -2.93) * mm]});
            skFitSpline(sketch, "E723", {"points": [v(-8.4, -2.7) * mm, v(-8.32, -2.67) * mm, v(-8.24, -2.6) * mm, v(-8.24, -2.57) * mm]});
            skFitSpline(sketch, "E724", {"points": [v(-8.24, -2.57) * mm, v(-8.24, -2.53) * mm, v(-8.3, -2.47) * mm, v(-8.32, -2.48) * mm]});
            skFitSpline(sketch, "E725", {"points": [v(-8.32, -2.48) * mm, v(-8.35, -2.49) * mm, v(-8.64, -1.88) * mm, v(-8.62, -1.87) * mm]});
            skFitSpline(sketch, "E726", {"points": [v(-8.62, -1.87) * mm, v(-8.59, -1.85) * mm, v(-8.64, -1.83) * mm, v(-8.7, -1.84) * mm]});
            skFitSpline(sketch, "E727", {"points": [v(-8.7, -1.84) * mm, v(-8.78, -1.86) * mm, v(-8.87, -1.9) * mm, v(-8.88, -1.95) * mm]});
            skFitSpline(sketch, "E728", {"points": [v(-8.88, -1.95) * mm, v(-8.88, -1.98) * mm, v(-8.88, -1.98) * mm, v(-8.86, -1.95) * mm]});
            skFitSpline(sketch, "E729", {"points": [v(-8.86, -1.95) * mm, v(-8.83, -1.92) * mm, v(-8.8, -1.93) * mm, v(-8.8, -1.99) * mm]});
            skFitSpline(sketch, "E730", {"points": [v(-8.8, -1.99) * mm, v(-8.8, -2.06) * mm, v(-8.76, -2.18) * mm, v(-8.66, -2.4) * mm]});
            skFitSpline(sketch, "E731", {"points": [v(-8.66, -2.4) * mm, v(-8.6, -2.52) * mm, v(-8.56, -2.62) * mm, v(-8.57, -2.64) * mm]});
            skFitSpline(sketch, "E732", {"points": [v(-8.57, -2.64) * mm, v(-8.58, -2.66) * mm, v(-8.58, -2.66) * mm, v(-8.6, -2.64) * mm]});
            skFitSpline(sketch, "E733", {"points": [v(-8.6, -2.64) * mm, v(-8.62, -2.62) * mm, v(-8.8, -2.3) * mm, v(-8.81, -2.24) * mm]});
            skFitSpline(sketch, "E734", {"points": [v(-8.81, -2.24) * mm, v(-8.82, -2.23) * mm, v(-8.83, -2.22) * mm, v(-8.84, -2.22) * mm]});
            skFitSpline(sketch, "E735", {"points": [v(-8.84, -2.22) * mm, v(-8.87, -2.22) * mm, v(-8.66, -2.68) * mm, v(-8.6, -2.73) * mm]});
            skFitSpline(sketch, "E736", {"points": [v(-8.6, -2.73) * mm, v(-8.56, -2.77) * mm, v(-8.53, -2.76) * mm, v(-8.4, -2.7) * mm]});
            skFitSpline(sketch, "E737", {"points": [v(-7.97, -2.47) * mm, v(-7.92, -2.46) * mm, v(-7.86, -2.42) * mm, v(-7.83, -2.4) * mm]});
            skFitSpline(sketch, "E738", {"points": [v(-7.83, -2.4) * mm, v(-7.78, -2.36) * mm, v(-7.78, -2.35) * mm, v(-7.8, -2.3) * mm]});
            skFitSpline(sketch, "E739", {"points": [v(-7.8, -2.3) * mm, v(-7.8, -2.27) * mm, v(-7.82, -2.25) * mm, v(-7.84, -2.25) * mm]});
            skFitSpline(sketch, "E740", {"points": [v(-7.84, -2.25) * mm, v(-7.88, -2.25) * mm, v(-7.9, -2.21) * mm, v(-7.99, -2) * mm]});
            skFitSpline(sketch, "E741", {"points": [v(-7.99, -2) * mm, v(-8.03, -1.89) * mm, v(-8.08, -1.77) * mm, v(-8.1, -1.73) * mm]});
            skFitSpline(sketch, "E742", {"points": [v(-8.1, -1.73) * mm, v(-8.16, -1.63) * mm, v(-8.23, -1.61) * mm, v(-8.3, -1.68) * mm]});
            skLineSegment(sketch, "E743", {"start": v(-8.3, -1.68) * mm, "end": v(-8.35, -1.73) * mm});
            skLineSegment(sketch, "E744", {"start": v(-8.35, -1.73) * mm, "end": v(-8.29, -1.88) * mm});
            skFitSpline(sketch, "E745", {"points": [v(-8.29, -1.88) * mm, v(-8.25, -1.96) * mm, v(-8.2, -2.1) * mm, v(-8.15, -2.19) * mm]});
            skFitSpline(sketch, "E746", {"points": [v(-8.15, -2.19) * mm, v(-8.06, -2.38) * mm, v(-8.06, -2.39) * mm, v(-8.1, -2.4) * mm]});
            skFitSpline(sketch, "E747", {"points": [v(-8.1, -2.4) * mm, v(-8.11, -2.4) * mm, v(-8.15, -2.35) * mm, v(-8.23, -2.17) * mm]});
            skFitSpline(sketch, "E748", {"points": [v(-8.23, -2.17) * mm, v(-8.37, -1.9) * mm, v(-8.4, -1.85) * mm, v(-8.36, -2) * mm]});
            skFitSpline(sketch, "E749", {"points": [v(-8.36, -2) * mm, v(-8.3, -2.15) * mm, v(-8.14, -2.48) * mm, v(-8.12, -2.5) * mm]});
            skFitSpline(sketch, "E750", {"points": [v(-8.12, -2.5) * mm, v(-8.08, -2.5) * mm, v(-8.05, -2.5) * mm, v(-7.97, -2.47) * mm]});
            skFitSpline(sketch, "E751", {"points": [v(-8.4, -1.68) * mm, v(-8.4, -1.67) * mm, v(-8.4, -1.66) * mm, v(-8.41, -1.66) * mm]});
            skFitSpline(sketch, "E752", {"points": [v(-8.41, -1.66) * mm, v(-8.42, -1.67) * mm, v(-8.42, -1.68) * mm, v(-8.42, -1.7) * mm]});
            skFitSpline(sketch, "E753", {"points": [v(-8.42, -1.7) * mm, v(-8.42, -1.72) * mm, v(-8.41, -1.72) * mm, v(-8.4, -1.68) * mm]});
            skFitSpline(sketch, "E754", {"points": [v(-8.22, -1.6) * mm, v(-8.2, -1.6) * mm, v(-8.32, -1.6) * mm, v(-8.35, -1.63) * mm]});
            skFitSpline(sketch, "E755", {"points": [v(-8.35, -1.63) * mm, v(-8.36, -1.64) * mm, v(-8.35, -1.64) * mm, v(-8.3, -1.63) * mm]});
            skFitSpline(sketch, "E756", {"points": [v(-8.3, -1.63) * mm, v(-8.27, -1.63) * mm, v(-8.23, -1.62) * mm, v(-8.22, -1.6) * mm]});
            skFitSpline(sketch, "E757", {"points": [v(8.68, -2.18) * mm, v(8.67, -2.17) * mm, v(8.66, -2.12) * mm, v(8.66, -2.04) * mm]});
            skFitSpline(sketch, "E758", {"points": [v(8.66, -2.04) * mm, v(8.66, -1.85) * mm, v(8.57, -1.35) * mm, v(8.54, -1.34) * mm]});
            skFitSpline(sketch, "E759", {"points": [v(8.54, -1.34) * mm, v(8.53, -1.34) * mm, v(8.41, -1.4) * mm, v(8.29, -1.49) * mm]});
            skFitSpline(sketch, "E760", {"points": [v(8.29, -1.49) * mm, v(7.98, -1.69) * mm, v(7.8, -1.77) * mm, v(7.78, -1.75) * mm]});
            skFitSpline(sketch, "E761", {"points": [v(7.78, -1.75) * mm, v(7.75, -1.72) * mm, v(7.75, -1.7) * mm, v(7.79, -1.6) * mm]});
            skFitSpline(sketch, "E762", {"points": [v(7.79, -1.6) * mm, v(7.82, -1.55) * mm, v(7.84, -1.53) * mm, v(7.94, -1.47) * mm]});
            skFitSpline(sketch, "E763", {"points": [v(7.94, -1.47) * mm, v(8.11, -1.37) * mm, v(8.18, -1.32) * mm, v(8.27, -1.23) * mm]});
            skFitSpline(sketch, "E764", {"points": [v(8.27, -1.23) * mm, v(8.33, -1.18) * mm, v(8.37, -1.15) * mm, v(8.38, -1.16) * mm]});
            skFitSpline(sketch, "E765", {"points": [v(8.38, -1.16) * mm, v(8.4, -1.16) * mm, v(8.4, -1.18) * mm, v(8.4, -1.18) * mm]});
            skFitSpline(sketch, "E766", {"points": [v(8.4, -1.18) * mm, v(8.39, -1.2) * mm, v(8.08, -1.4) * mm, v(7.94, -1.5) * mm]});
            skFitSpline(sketch, "E767", {"points": [v(7.94, -1.5) * mm, v(7.89, -1.53) * mm, v(7.85, -1.56) * mm, v(7.85, -1.56) * mm]});
            skFitSpline(sketch, "E768", {"points": [v(7.85, -1.56) * mm, v(7.88, -1.59) * mm, v(8.55, -1.2) * mm, v(8.57, -1.14) * mm]});
            skFitSpline(sketch, "E769", {"points": [v(8.57, -1.14) * mm, v(8.58, -1.1) * mm, v(8.54, -1.07) * mm, v(8.42, -1.04) * mm]});
            skFitSpline(sketch, "E770", {"points": [v(8.42, -1.04) * mm, v(8.07, -0.97) * mm, v(8.06, -0.96) * mm, v(8.08, -0.89) * mm]});
            skFitSpline(sketch, "E771", {"points": [v(8.08, -0.89) * mm, v(8.1, -0.83) * mm, v(8.12, -0.83) * mm, v(8.26, -0.9) * mm]});
            skFitSpline(sketch, "E772", {"points": [v(8.26, -0.9) * mm, v(8.43, -0.97) * mm, v(8.75, -1.07) * mm, v(8.95, -1.12) * mm]});
            skFitSpline(sketch, "E773", {"points": [v(8.95, -1.12) * mm, v(9.1, -1.16) * mm, v(9.12, -1.16) * mm, v(9.12, -1.2) * mm]});
            skFitSpline(sketch, "E774", {"points": [v(9.12, -1.2) * mm, v(9.12, -1.24) * mm, v(9.07, -1.24) * mm, v(8.93, -1.18) * mm]});
            skFitSpline(sketch, "E775", {"points": [v(8.93, -1.18) * mm, v(8.8, -1.13) * mm, v(8.68, -1.12) * mm, v(8.64, -1.16) * mm]});
            skFitSpline(sketch, "E776", {"points": [v(8.64, -1.16) * mm, v(8.61, -1.2) * mm, v(8.61, -1.2) * mm, v(8.64, -1.25) * mm]});
            skFitSpline(sketch, "E777", {"points": [v(8.64, -1.25) * mm, v(8.65, -1.28) * mm, v(8.66, -1.29) * mm, v(8.69, -1.28) * mm]});
            skFitSpline(sketch, "E778", {"points": [v(8.69, -1.28) * mm, v(8.71, -1.27) * mm, v(8.73, -1.28) * mm, v(8.73, -1.3) * mm]});
            skFitSpline(sketch, "E779", {"points": [v(8.73, -1.3) * mm, v(8.72, -1.32) * mm, v(8.7, -1.35) * mm, v(8.69, -1.36) * mm]});
            skFitSpline(sketch, "E780", {"points": [v(8.69, -1.36) * mm, v(8.66, -1.36) * mm, v(8.68, -1.45) * mm, v(8.74, -1.67) * mm]});
            skFitSpline(sketch, "E781", {"points": [v(8.74, -1.67) * mm, v(8.78, -1.8) * mm, v(8.8, -1.92) * mm, v(8.81, -2) * mm]});
            skFitSpline(sketch, "E782", {"points": [v(8.81, -2) * mm, v(8.82, -2.1) * mm, v(8.82, -2.12) * mm, v(8.79, -2.16) * mm]});
            skFitSpline(sketch, "E783", {"points": [v(8.79, -2.16) * mm, v(8.75, -2.2) * mm, v(8.71, -2.21) * mm, v(8.68, -2.18) * mm]});
            skFitSpline(sketch, "E784", {"points": [v(8.47, -1.58) * mm, v(8.46, -1.53) * mm, v(8.45, -1.53) * mm, v(8.42, -1.53) * mm]});
            skFitSpline(sketch, "E785", {"points": [v(8.42, -1.53) * mm, v(8.4, -1.53) * mm, v(8.38, -1.52) * mm, v(8.38, -1.52) * mm]});
            skFitSpline(sketch, "E786", {"points": [v(8.38, -1.52) * mm, v(8.38, -1.5) * mm, v(8.43, -1.46) * mm, v(8.45, -1.46) * mm]});
            skFitSpline(sketch, "E787", {"points": [v(8.45, -1.46) * mm, v(8.46, -1.46) * mm, v(8.5, -1.62) * mm, v(8.5, -1.63) * mm]});
            skFitSpline(sketch, "E788", {"points": [v(8.5, -1.63) * mm, v(8.49, -1.64) * mm, v(8.48, -1.61) * mm, v(8.47, -1.58) * mm]});
            skFitSpline(sketch, "E789", {"points": [v(-9.4, -1.07) * mm, v(-9.4, -1.06) * mm, v(-9.41, -1.04) * mm, v(-9.4, -1.02) * mm]});
            skFitSpline(sketch, "E790", {"points": [v(-9.4, -1.02) * mm, v(-9.4, -0.98) * mm, v(-9.37, -0.97) * mm, v(-8.98, -0.85) * mm]});
            skFitSpline(sketch, "E791", {"points": [v(-8.98, -0.85) * mm, v(-8.74, -0.78) * mm, v(-8.54, -0.71) * mm, v(-8.53, -0.7) * mm]});
            skFitSpline(sketch, "E792", {"points": [v(-8.53, -0.7) * mm, v(-8.52, -0.7) * mm, v(-8.5, -0.62) * mm, v(-8.5, -0.54) * mm]});
            skFitSpline(sketch, "E793", {"points": [v(-8.5, -0.54) * mm, v(-8.5, -0.3) * mm, v(-8.57, -0.03) * mm, v(-8.67, 0.02) * mm]});
            skFitSpline(sketch, "E794", {"points": [v(-8.67, 0.02) * mm, v(-8.72, 0.05) * mm, v(-8.78, 0.05) * mm, v(-9.05, 0.02) * mm]});
            skLineSegment(sketch, "E795", {"start": v(-9.05, 0.02) * mm, "end": v(-9.12, 0.02) * mm});
            skLineSegment(sketch, "E796", {"start": v(-9.12, 0.02) * mm, "end": v(-9.03, 0.04) * mm});
            skFitSpline(sketch, "E797", {"points": [v(-9.03, 0.04) * mm, v(-8.99, 0.05) * mm, v(-8.88, 0.06) * mm, v(-8.8, 0.07) * mm]});
            skFitSpline(sketch, "E798", {"points": [v(-8.8, 0.07) * mm, v(-8.65, 0.08) * mm, v(-8.63, 0.1) * mm, v(-8.7, 0.13) * mm]});
            skFitSpline(sketch, "E799", {"points": [v(-8.7, 0.13) * mm, v(-8.76, 0.17) * mm, v(-8.95, 0.15) * mm, v(-9.2, 0.08) * mm]});
            skFitSpline(sketch, "E800", {"points": [v(-9.2, 0.08) * mm, v(-9.32, 0.04) * mm, v(-9.46, 0.01) * mm, v(-9.5, 0) * mm]});
            skFitSpline(sketch, "E801", {"points": [v(-9.5, 0) * mm, v(-9.58, 0) * mm, v(-9.6, 0) * mm, v(-9.62, 0.03) * mm]});
            skFitSpline(sketch, "E802", {"points": [v(-9.62, 0.03) * mm, v(-9.67, 0.07) * mm, v(-9.66, 0.1) * mm, v(-9.6, 0.13) * mm]});
            skFitSpline(sketch, "E803", {"points": [v(-9.6, 0.13) * mm, v(-9.47, 0.2) * mm, v(-8.93, 0.28) * mm, v(-8.76, 0.27) * mm]});
            skFitSpline(sketch, "E804", {"points": [v(-8.76, 0.27) * mm, v(-8.62, 0.26) * mm, v(-8.56, 0.22) * mm, v(-8.5, 0.1) * mm]});
            skFitSpline(sketch, "E805", {"points": [v(-8.5, 0.1) * mm, v(-8.43, -0.04) * mm, v(-8.36, -0.31) * mm, v(-8.35, -0.5) * mm]});
            skFitSpline(sketch, "E806", {"points": [v(-8.35, -0.5) * mm, v(-8.34, -0.8) * mm, v(-8.43, -0.88) * mm, v(-8.98, -1.03) * mm]});
            skFitSpline(sketch, "E807", {"points": [v(-8.98, -1.03) * mm, v(-9.14, -1.07) * mm, v(-9.36, -1.09) * mm, v(-9.4, -1.07) * mm]});
            skFitSpline(sketch, "E808", {"points": [v(-8.3, -0.4) * mm, v(-8.32, -0.31) * mm, v(-8.34, -0.1) * mm, v(-8.33, -0.1) * mm]});
            skFitSpline(sketch, "E809", {"points": [v(-8.33, -0.1) * mm, v(-8.32, -0.12) * mm, v(-8.27, -0.42) * mm, v(-8.28, -0.44) * mm]});
            skFitSpline(sketch, "E810", {"points": [v(-8.28, -0.44) * mm, v(-8.28, -0.45) * mm, v(-8.3, -0.43) * mm, v(-8.3, -0.4) * mm]});
            skFitSpline(sketch, "E811", {"points": [v(9, -0.38) * mm, v(8.92, -0.36) * mm, v(8.9, -0.3) * mm, v(8.95, -0.25) * mm]});
            skFitSpline(sketch, "E812", {"points": [v(8.95, -0.25) * mm, v(8.97, -0.23) * mm, v(9, -0.23) * mm, v(9.06, -0.23) * mm]});
            skFitSpline(sketch, "E813", {"points": [v(9.06, -0.23) * mm, v(9.16, -0.24) * mm, v(9.18, -0.22) * mm, v(9.18, -0.17) * mm]});
            skFitSpline(sketch, "E814", {"points": [v(9.18, -0.17) * mm, v(9.18, -0.14) * mm, v(9.18, -0.14) * mm, v(9.15, -0.15) * mm]});
            skFitSpline(sketch, "E815", {"points": [v(9.15, -0.15) * mm, v(9.13, -0.17) * mm, v(9.12, -0.17) * mm, v(9.11, -0.17) * mm]});
            skFitSpline(sketch, "E816", {"points": [v(9.11, -0.17) * mm, v(9.1, -0.16) * mm, v(9.12, -0.11) * mm, v(9.14, -0.05) * mm]});
            skFitSpline(sketch, "E817", {"points": [v(9.14, -0.05) * mm, v(9.16, 0.03) * mm, v(9.17, 0.1) * mm, v(9.18, 0.3) * mm]});
            skFitSpline(sketch, "E818", {"points": [v(9.18, 0.3) * mm, v(9.18, 0.45) * mm, v(9.18, 0.57) * mm, v(9.19, 0.57) * mm]});
            skFitSpline(sketch, "E819", {"points": [v(9.19, 0.57) * mm, v(9.19, 0.58) * mm, v(9.2, 0.56) * mm, v(9.22, 0.54) * mm]});
            skFitSpline(sketch, "E820", {"points": [v(9.22, 0.54) * mm, v(9.26, 0.5) * mm, v(9.27, 0.5) * mm, v(9.28, 0.54) * mm]});
            skFitSpline(sketch, "E821", {"points": [v(9.28, 0.54) * mm, v(9.3, 0.65) * mm, v(9.18, 0.72) * mm, v(8.9, 0.75) * mm]});
            skFitSpline(sketch, "E822", {"points": [v(8.9, 0.75) * mm, v(8.71, 0.77) * mm, v(8.62, 0.76) * mm, v(8.55, 0.71) * mm]});
            skFitSpline(sketch, "E823", {"points": [v(8.55, 0.71) * mm, v(8.48, 0.67) * mm, v(8.43, 0.6) * mm, v(8.45, 0.57) * mm]});
            skFitSpline(sketch, "E824", {"points": [v(8.45, 0.57) * mm, v(8.47, 0.55) * mm, v(8.46, 0.5) * mm, v(8.44, 0.38) * mm]});
            skFitSpline(sketch, "E825", {"points": [v(8.44, 0.38) * mm, v(8.42, 0.3) * mm, v(8.4, 0.15) * mm, v(8.4, 0.06) * mm]});
            skLineSegment(sketch, "E826", {"start": v(8.4, 0.06) * mm, "end": v(8.4, -0.1) * mm});
            skLineSegment(sketch, "E827", {"start": v(8.4, -0.1) * mm, "end": v(8.47, -0.14) * mm});
            skFitSpline(sketch, "E828", {"points": [v(8.47, -0.14) * mm, v(8.56, -0.18) * mm, v(8.58, -0.21) * mm, v(8.54, -0.27) * mm]});
            skFitSpline(sketch, "E829", {"points": [v(8.54, -0.27) * mm, v(8.5, -0.3) * mm, v(8.4, -0.3) * mm, v(8.33, -0.26) * mm]});
            skFitSpline(sketch, "E830", {"points": [v(8.33, -0.26) * mm, v(8.25, -0.2) * mm, v(8.23, -0.15) * mm, v(8.23, 0.08) * mm]});
            skFitSpline(sketch, "E831", {"points": [v(8.23, 0.08) * mm, v(8.24, 0.46) * mm, v(8.31, 0.73) * mm, v(8.43, 0.81) * mm]});
            skFitSpline(sketch, "E832", {"points": [v(8.43, 0.81) * mm, v(8.5, 0.86) * mm, v(8.67, 0.89) * mm, v(8.88, 0.87) * mm]});
            skFitSpline(sketch, "E833", {"points": [v(8.88, 0.87) * mm, v(9.18, 0.86) * mm, v(9.32, 0.8) * mm, v(9.38, 0.68) * mm]});
            skFitSpline(sketch, "E834", {"points": [v(9.38, 0.68) * mm, v(9.47, 0.5) * mm, v(9.43, 0.02) * mm, v(9.32, -0.22) * mm]});
            skFitSpline(sketch, "E835", {"points": [v(9.32, -0.22) * mm, v(9.25, -0.36) * mm, v(9.14, -0.41) * mm, v(9, -0.38) * mm]});
            skFitSpline(sketch, "E836", {"points": [v(-9.74, 1.35) * mm, v(-9.78, 1.42) * mm, v(-9.76, 1.67) * mm, v(-9.7, 1.67) * mm]});
            skFitSpline(sketch, "E837", {"points": [v(-9.7, 1.67) * mm, v(-9.7, 1.67) * mm, v(-9.67, 1.65) * mm, v(-9.65, 1.63) * mm]});
            skFitSpline(sketch, "E838", {"points": [v(-9.65, 1.63) * mm, v(-9.58, 1.55) * mm, v(-9.56, 1.55) * mm, v(-9.2, 1.55) * mm]});
            skFitSpline(sketch, "E839", {"points": [v(-9.2, 1.55) * mm, v(-9, 1.55) * mm, v(-8.83, 1.55) * mm, v(-8.8, 1.56) * mm]});
            skFitSpline(sketch, "E840", {"points": [v(-8.8, 1.56) * mm, v(-8.77, 1.57) * mm, v(-8.72, 1.6) * mm, v(-8.7, 1.62) * mm]});
            skFitSpline(sketch, "E841", {"points": [v(-8.7, 1.62) * mm, v(-8.6, 1.71) * mm, v(-8.56, 1.68) * mm, v(-8.56, 1.52) * mm]});
            skFitSpline(sketch, "E842", {"points": [v(-8.56, 1.52) * mm, v(-8.56, 1.45) * mm, v(-8.57, 1.4) * mm, v(-8.58, 1.38) * mm]});
            skFitSpline(sketch, "E843", {"points": [v(-8.58, 1.38) * mm, v(-8.6, 1.36) * mm, v(-8.66, 1.36) * mm, v(-8.69, 1.4) * mm]});
            skFitSpline(sketch, "E844", {"points": [v(-8.69, 1.4) * mm, v(-8.7, 1.43) * mm, v(-8.72, 1.43) * mm, v(-9.16, 1.43) * mm]});
            skLineSegment(sketch, "E845", {"start": v(-9.16, 1.43) * mm, "end": v(-9.6, 1.43) * mm});
            skLineSegment(sketch, "E846", {"start": v(-9.6, 1.43) * mm, "end": v(-9.62, 1.4) * mm});
            skFitSpline(sketch, "E847", {"points": [v(-9.62, 1.4) * mm, v(-9.64, 1.32) * mm, v(-9.7, 1.3) * mm, v(-9.74, 1.35) * mm]});
            skFitSpline(sketch, "E848", {"points": [v(8.35, 1.48) * mm, v(8.34, 1.49) * mm, v(8.33, 1.51) * mm, v(8.32, 1.53) * mm]});
            skFitSpline(sketch, "E849", {"points": [v(8.32, 1.53) * mm, v(8.31, 1.57) * mm, v(8.32, 1.58) * mm, v(8.43, 1.63) * mm]});
            skFitSpline(sketch, "E850", {"points": [v(8.43, 1.63) * mm, v(8.53, 1.68) * mm, v(8.54, 1.69) * mm, v(8.54, 1.73) * mm]});
            skFitSpline(sketch, "E851", {"points": [v(8.54, 1.73) * mm, v(8.54, 1.78) * mm, v(8.52, 1.8) * mm, v(8.5, 1.77) * mm]});
            skFitSpline(sketch, "E852", {"points": [v(8.5, 1.77) * mm, v(8.47, 1.74) * mm, v(8.47, 1.75) * mm, v(8.46, 1.8) * mm]});
            skFitSpline(sketch, "E853", {"points": [v(8.46, 1.8) * mm, v(8.46, 1.84) * mm, v(8.45, 1.94) * mm, v(8.45, 2.02) * mm]});
            skFitSpline(sketch, "E854", {"points": [v(8.45, 2.02) * mm, v(8.44, 2.16) * mm, v(8.44, 2.16) * mm, v(8.45, 2.06) * mm]});
            skFitSpline(sketch, "E855", {"points": [v(8.45, 2.06) * mm, v(8.46, 2) * mm, v(8.48, 1.92) * mm, v(8.49, 1.89) * mm]});
            skLineSegment(sketch, "E856", {"start": v(8.49, 1.89) * mm, "end": v(8.5, 1.83) * mm});
            skLineSegment(sketch, "E857", {"start": v(8.5, 1.83) * mm, "end": v(8.51, 1.93) * mm});
            skFitSpline(sketch, "E858", {"points": [v(8.51, 1.93) * mm, v(8.52, 2.06) * mm, v(8.49, 2.37) * mm, v(8.47, 2.39) * mm]});
            skFitSpline(sketch, "E859", {"points": [v(8.47, 2.39) * mm, v(8.46, 2.4) * mm, v(8.4, 2.42) * mm, v(8.33, 2.44) * mm]});
            skFitSpline(sketch, "E860", {"points": [v(8.33, 2.44) * mm, v(8.22, 2.48) * mm, v(8.22, 2.48) * mm, v(8.21, 2.53) * mm]});
            skFitSpline(sketch, "E861", {"points": [v(8.21, 2.53) * mm, v(8.2, 2.59) * mm, v(8.21, 2.6) * mm, v(8.4, 2.56) * mm]});
            skFitSpline(sketch, "E862", {"points": [v(8.4, 2.56) * mm, v(8.72, 2.5) * mm, v(9.12, 2.39) * mm, v(9.29, 2.31) * mm]});
            skFitSpline(sketch, "E863", {"points": [v(9.29, 2.31) * mm, v(9.4, 2.27) * mm, v(9.4, 2.24) * mm, v(9.4, 2.1) * mm]});
            skLineSegment(sketch, "E864", {"start": v(9.4, 2.1) * mm, "end": v(9.4, 2) * mm});
            skLineSegment(sketch, "E865", {"start": v(9.4, 2) * mm, "end": v(9.16, 1.87) * mm});
            skFitSpline(sketch, "E866", {"points": [v(9.16, 1.87) * mm, v(9.03, 1.8) * mm, v(8.8, 1.68) * mm, v(8.64, 1.6) * mm]});
            skFitSpline(sketch, "E867", {"points": [v(8.64, 1.6) * mm, v(8.43, 1.49) * mm, v(8.36, 1.46) * mm, v(8.35, 1.48) * mm]});
            skFitSpline(sketch, "E868", {"points": [v(9.25, 2.07) * mm, v(9.3, 2.1) * mm, v(9.3, 2.12) * mm, v(9.23, 2.14) * mm]});
            skFitSpline(sketch, "E869", {"points": [v(9.23, 2.14) * mm, v(9.2, 2.15) * mm, v(9.16, 2.17) * mm, v(9.15, 2.18) * mm]});
            skFitSpline(sketch, "E870", {"points": [v(9.15, 2.18) * mm, v(9.11, 2.23) * mm, v(9, 2.28) * mm, v(8.82, 2.33) * mm]});
            skFitSpline(sketch, "E871", {"points": [v(8.82, 2.33) * mm, v(8.72, 2.36) * mm, v(8.63, 2.38) * mm, v(8.62, 2.38) * mm]});
            skFitSpline(sketch, "E872", {"points": [v(8.62, 2.38) * mm, v(8.6, 2.36) * mm, v(8.64, 2.26) * mm, v(8.67, 2.24) * mm]});
            skFitSpline(sketch, "E873", {"points": [v(8.67, 2.24) * mm, v(8.69, 2.23) * mm, v(8.7, 2.2) * mm, v(8.7, 2.12) * mm]});
            skFitSpline(sketch, "E874", {"points": [v(8.7, 2.12) * mm, v(8.7, 2.07) * mm, v(8.7, 1.98) * mm, v(8.71, 1.94) * mm]});
            skFitSpline(sketch, "E875", {"points": [v(8.71, 1.94) * mm, v(8.73, 1.87) * mm, v(8.73, 1.85) * mm, v(8.71, 1.83) * mm]});
            skFitSpline(sketch, "E876", {"points": [v(8.71, 1.83) * mm, v(8.7, 1.82) * mm, v(8.7, 1.8) * mm, v(8.7, 1.8) * mm]});
            skFitSpline(sketch, "E877", {"points": [v(8.7, 1.8) * mm, v(8.7, 1.78) * mm, v(9.15, 2) * mm, v(9.25, 2.07) * mm]});
            skFitSpline(sketch, "E878", {"points": [v(9.08, 2.1) * mm, v(9.08, 2.12) * mm, v(9.08, 2.13) * mm, v(9.1, 2.12) * mm]});
            skFitSpline(sketch, "E879", {"points": [v(9.1, 2.12) * mm, v(9.11, 2.11) * mm, v(9.13, 2.1) * mm, v(9.14, 2.1) * mm]});
            skFitSpline(sketch, "E880", {"points": [v(9.14, 2.1) * mm, v(9.14, 2.1) * mm, v(9.15, 2.1) * mm, v(9.15, 2.1) * mm]});
            skFitSpline(sketch, "E881", {"points": [v(9.15, 2.1) * mm, v(9.15, 2.07) * mm, v(9.1, 2.08) * mm, v(9.08, 2.1) * mm]});
            skFitSpline(sketch, "E882", {"points": [v(8.42, 2.2) * mm, v(8.42, 2.21) * mm, v(8.43, 2.22) * mm, v(8.43, 2.2) * mm]});
            skFitSpline(sketch, "E883", {"points": [v(8.43, 2.2) * mm, v(8.44, 2.2) * mm, v(8.44, 2.18) * mm, v(8.43, 2.17) * mm]});
            skFitSpline(sketch, "E884", {"points": [v(8.43, 2.17) * mm, v(8.43, 2.17) * mm, v(8.42, 2.18) * mm, v(8.42, 2.2) * mm]});
            skLineSegment(sketch, "E885", {"start": v(8.42, 2.2) * mm, "end": v(8.42, 2.2) * mm});
            skFitSpline(sketch, "E886", {"points": [v(-8.6, 2.85) * mm, v(-8.66, 2.86) * mm, v(-8.88, 2.9) * mm, v(-9.1, 2.93) * mm]});
            skFitSpline(sketch, "E887", {"points": [v(-9.1, 2.93) * mm, v(-9.63, 3) * mm, v(-9.58, 3) * mm, v(-9.58, 3.06) * mm]});
            skFitSpline(sketch, "E888", {"points": [v(-9.58, 3.06) * mm, v(-9.58, 3.1) * mm, v(-9.57, 3.13) * mm, v(-9.56, 3.14) * mm]});
            skFitSpline(sketch, "E889", {"points": [v(-9.56, 3.14) * mm, v(-9.54, 3.15) * mm, v(-9.43, 3.14) * mm, v(-9.05, 3.07) * mm]});
            skFitSpline(sketch, "E890", {"points": [v(-9.05, 3.07) * mm, v(-8.79, 3.03) * mm, v(-8.57, 3) * mm, v(-8.56, 3) * mm]});
            skFitSpline(sketch, "E891", {"points": [v(-8.56, 3) * mm, v(-8.54, 3.01) * mm, v(-8.5, 3.14) * mm, v(-8.48, 3.3) * mm]});
            skFitSpline(sketch, "E892", {"points": [v(-8.48, 3.3) * mm, v(-8.45, 3.48) * mm, v(-8.42, 3.59) * mm, v(-8.37, 3.66) * mm]});
            skFitSpline(sketch, "E893", {"points": [v(-8.37, 3.66) * mm, v(-8.33, 3.73) * mm, v(-8.32, 3.73) * mm, v(-8.28, 3.7) * mm]});
            skFitSpline(sketch, "E894", {"points": [v(-8.28, 3.7) * mm, v(-8.23, 3.66) * mm, v(-8.23, 3.64) * mm, v(-8.29, 3.45) * mm]});
            skFitSpline(sketch, "E895", {"points": [v(-8.29, 3.45) * mm, v(-8.31, 3.36) * mm, v(-8.35, 3.2) * mm, v(-8.38, 3.07) * mm]});
            skFitSpline(sketch, "E896", {"points": [v(-8.38, 3.07) * mm, v(-8.42, 2.88) * mm, v(-8.45, 2.82) * mm, v(-8.48, 2.82) * mm]});
            skFitSpline(sketch, "E897", {"points": [v(-8.48, 2.82) * mm, v(-8.49, 2.83) * mm, v(-8.54, 2.84) * mm, v(-8.6, 2.85) * mm]});
            skFitSpline(sketch, "E898", {"points": [v(8.09, 3.15) * mm, v(8.06, 3.16) * mm, v(8.02, 3.24) * mm, v(8.04, 3.26) * mm]});
            skFitSpline(sketch, "E899", {"points": [v(8.04, 3.26) * mm, v(8.04, 3.27) * mm, v(8.1, 3.3) * mm, v(8.16, 3.3) * mm]});
            skFitSpline(sketch, "E900", {"points": [v(8.16, 3.3) * mm, v(8.23, 3.33) * mm, v(8.3, 3.36) * mm, v(8.34, 3.37) * mm]});
            skLineSegment(sketch, "E901", {"start": v(8.34, 3.37) * mm, "end": v(8.4, 3.4) * mm});
            skLineSegment(sketch, "E902", {"start": v(8.4, 3.4) * mm, "end": v(8.36, 3.41) * mm});
            skFitSpline(sketch, "E903", {"points": [v(8.36, 3.41) * mm, v(8.33, 3.41) * mm, v(8.28, 3.4) * mm, v(8.24, 3.4) * mm]});
            skFitSpline(sketch, "E904", {"points": [v(8.24, 3.4) * mm, v(8.15, 3.35) * mm, v(8.15, 3.37) * mm, v(8.24, 3.41) * mm]});
            skFitSpline(sketch, "E905", {"points": [v(8.24, 3.41) * mm, v(8.35, 3.46) * mm, v(8.38, 3.49) * mm, v(8.38, 3.54) * mm]});
            skFitSpline(sketch, "E906", {"points": [v(8.38, 3.54) * mm, v(8.38, 3.6) * mm, v(8.3, 3.83) * mm, v(8.22, 4) * mm]});
            skFitSpline(sketch, "E907", {"points": [v(8.22, 4) * mm, v(8.17, 4.1) * mm, v(8.16, 4.14) * mm, v(8.17, 4.14) * mm]});
            skFitSpline(sketch, "E908", {"points": [v(8.17, 4.14) * mm, v(8.2, 4.14) * mm, v(8.24, 4.2) * mm, v(8.22, 4.23) * mm]});
            skFitSpline(sketch, "E909", {"points": [v(8.22, 4.23) * mm, v(8.2, 4.29) * mm, v(8.14, 4.27) * mm, v(7.96, 4.18) * mm]});
            skFitSpline(sketch, "E910", {"points": [v(7.96, 4.18) * mm, v(7.83, 4.11) * mm, v(7.78, 4.1) * mm, v(7.74, 4.1) * mm]});
            skFitSpline(sketch, "E911", {"points": [v(7.74, 4.1) * mm, v(7.7, 4.1) * mm, v(7.69, 4.11) * mm, v(7.68, 4.15) * mm]});
            skFitSpline(sketch, "E912", {"points": [v(7.68, 4.15) * mm, v(7.68, 4.18) * mm, v(7.69, 4.2) * mm, v(7.7, 4.21) * mm]});
            skFitSpline(sketch, "E913", {"points": [v(7.7, 4.21) * mm, v(7.7, 4.22) * mm, v(7.8, 4.27) * mm, v(7.91, 4.31) * mm]});
            skFitSpline(sketch, "E914", {"points": [v(7.91, 4.31) * mm, v(8.16, 4.41) * mm, v(8.23, 4.44) * mm, v(8.4, 4.56) * mm]});
            skFitSpline(sketch, "E915", {"points": [v(8.4, 4.56) * mm, v(8.62, 4.7) * mm, v(8.65, 4.7) * mm, v(8.7, 4.62) * mm]});
            skFitSpline(sketch, "E916", {"points": [v(8.7, 4.62) * mm, v(8.72, 4.57) * mm, v(8.72, 4.57) * mm, v(8.7, 4.54) * mm]});
            skFitSpline(sketch, "E917", {"points": [v(8.7, 4.54) * mm, v(8.67, 4.52) * mm, v(8.63, 4.5) * mm, v(8.59, 4.48) * mm]});
            skFitSpline(sketch, "E918", {"points": [v(8.59, 4.48) * mm, v(8.55, 4.47) * mm, v(8.5, 4.45) * mm, v(8.5, 4.43) * mm]});
            skFitSpline(sketch, "E919", {"points": [v(8.5, 4.43) * mm, v(8.47, 4.42) * mm, v(8.43, 4.4) * mm, v(8.4, 4.4) * mm]});
            skFitSpline(sketch, "E920", {"points": [v(8.4, 4.4) * mm, v(8.34, 4.38) * mm, v(8.3, 4.35) * mm, v(8.3, 4.31) * mm]});
            skFitSpline(sketch, "E921", {"points": [v(8.3, 4.31) * mm, v(8.3, 4.3) * mm, v(8.32, 4.26) * mm, v(8.35, 4.21) * mm]});
            skFitSpline(sketch, "E922", {"points": [v(8.35, 4.21) * mm, v(8.37, 4.17) * mm, v(8.43, 4.05) * mm, v(8.47, 3.94) * mm]});
            skFitSpline(sketch, "E923", {"points": [v(8.47, 3.94) * mm, v(8.55, 3.71) * mm, v(8.57, 3.67) * mm, v(8.64, 3.6) * mm]});
            skFitSpline(sketch, "E924", {"points": [v(8.64, 3.6) * mm, v(8.68, 3.55) * mm, v(8.68, 3.55) * mm, v(8.66, 3.53) * mm]});
            skFitSpline(sketch, "E925", {"points": [v(8.66, 3.53) * mm, v(8.63, 3.51) * mm, v(8.63, 3.5) * mm, v(8.64, 3.48) * mm]});
            skFitSpline(sketch, "E926", {"points": [v(8.64, 3.48) * mm, v(8.65, 3.47) * mm, v(8.67, 3.45) * mm, v(8.67, 3.46) * mm]});
            skFitSpline(sketch, "E927", {"points": [v(8.67, 3.46) * mm, v(8.68, 3.46) * mm, v(8.77, 3.49) * mm, v(8.87, 3.52) * mm]});
            skFitSpline(sketch, "E928", {"points": [v(8.87, 3.52) * mm, v(9.08, 3.6) * mm, v(9.1, 3.6) * mm, v(9.12, 3.5) * mm]});
            skLineSegment(sketch, "E929", {"start": v(9.12, 3.5) * mm, "end": v(9.12, 3.45) * mm});
            skLineSegment(sketch, "E930", {"start": v(9.12, 3.45) * mm, "end": v(8.97, 3.4) * mm});
            skFitSpline(sketch, "E931", {"points": [v(8.97, 3.4) * mm, v(8.9, 3.37) * mm, v(8.76, 3.33) * mm, v(8.69, 3.3) * mm]});
            skFitSpline(sketch, "E932", {"points": [v(8.69, 3.3) * mm, v(8.35, 3.2) * mm, v(8.12, 3.14) * mm, v(8.11, 3.14) * mm]});
            skFitSpline(sketch, "E933", {"points": [v(8.11, 3.14) * mm, v(8.11, 3.14) * mm, v(8.1, 3.15) * mm, v(8.09, 3.15) * mm]});
            skLineSegment(sketch, "E934", {"start": v(8.09, 3.15) * mm, "end": v(8.09, 3.15) * mm});
            skFitSpline(sketch, "E935", {"points": [v(8.5, 3.44) * mm, v(8.49, 3.48) * mm, v(8.46, 3.48) * mm, v(8.44, 3.45) * mm]});
            skFitSpline(sketch, "E936", {"points": [v(8.44, 3.45) * mm, v(8.42, 3.42) * mm, v(8.43, 3.41) * mm, v(8.46, 3.41) * mm]});
            skFitSpline(sketch, "E937", {"points": [v(8.46, 3.41) * mm, v(8.49, 3.41) * mm, v(8.5, 3.42) * mm, v(8.5, 3.44) * mm]});
            skFitSpline(sketch, "E938", {"points": [v(-3.56, 3.88) * mm, v(-3.62, 3.94) * mm, v(-3.77, 4.08) * mm, v(-3.9, 4.2) * mm]});
            skFitSpline(sketch, "E939", {"points": [v(-3.9, 4.2) * mm, v(-4.12, 4.41) * mm, v(-4.14, 4.43) * mm, v(-4.34, 4.53) * mm]});
            skFitSpline(sketch, "E940", {"points": [v(-4.34, 4.53) * mm, v(-4.62, 4.68) * mm, v(-4.79, 4.73) * mm, v(-5.17, 4.77) * mm]});
            skFitSpline(sketch, "E941", {"points": [v(-5.17, 4.77) * mm, v(-5.5, 4.8) * mm, v(-5.63, 4.85) * mm, v(-5.8, 4.95) * mm]});
            skFitSpline(sketch, "E942", {"points": [v(-5.8, 4.95) * mm, v(-6.1, 5.14) * mm, v(-6.3, 5.34) * mm, v(-6.48, 5.67) * mm]});
            skFitSpline(sketch, "E943", {"points": [v(-6.48, 5.67) * mm, v(-6.62, 5.91) * mm, v(-6.68, 6.07) * mm, v(-6.71, 6.25) * mm]});
            skFitSpline(sketch, "E944", {"points": [v(-6.71, 6.25) * mm, v(-6.73, 6.37) * mm, v(-6.73, 6.38) * mm, v(-6.7, 6.4) * mm]});
            skFitSpline(sketch, "E945", {"points": [v(-6.7, 6.4) * mm, v(-6.67, 6.42) * mm, v(-6.6, 6.43) * mm, v(-6.55, 6.4) * mm]});
            skFitSpline(sketch, "E946", {"points": [v(-6.55, 6.4) * mm, v(-6.53, 6.4) * mm, v(-6.33, 6.27) * mm, v(-6.11, 6.13) * mm]});
            skFitSpline(sketch, "E947", {"points": [v(-6.11, 6.13) * mm, v(-5.72, 5.88) * mm, v(-5.6, 5.8) * mm, v(-5.49, 5.75) * mm]});
            skFitSpline(sketch, "E948", {"points": [v(-5.49, 5.75) * mm, v(-5.43, 5.72) * mm, v(-5.43, 5.72) * mm, v(-5.35, 5.76) * mm]});
            skFitSpline(sketch, "E949", {"points": [v(-5.35, 5.76) * mm, v(-5.26, 5.8) * mm, v(-5, 6.02) * mm, v(-4.9, 6.13) * mm]});
            skFitSpline(sketch, "E950", {"points": [v(-4.9, 6.13) * mm, v(-4.83, 6.22) * mm, v(-4.71, 6.43) * mm, v(-4.67, 6.57) * mm]});
            skFitSpline(sketch, "E951", {"points": [v(-4.67, 6.57) * mm, v(-4.63, 6.68) * mm, v(-4.64, 6.9) * mm, v(-4.68, 6.96) * mm]});
            skFitSpline(sketch, "E952", {"points": [v(-4.68, 6.96) * mm, v(-4.72, 7) * mm, v(-4.82, 7.09) * mm, v(-4.92, 7.16) * mm]});
            skFitSpline(sketch, "E953", {"points": [v(-4.92, 7.16) * mm, v(-4.95, 7.18) * mm, v(-5.05, 7.24) * mm, v(-5.14, 7.3) * mm]});
            skFitSpline(sketch, "E954", {"points": [v(-5.14, 7.3) * mm, v(-5.23, 7.37) * mm, v(-5.4, 7.49) * mm, v(-5.51, 7.56) * mm]});
            skFitSpline(sketch, "E955", {"points": [v(-5.51, 7.56) * mm, v(-5.74, 7.71) * mm, v(-5.79, 7.76) * mm, v(-5.76, 7.84) * mm]});
            skFitSpline(sketch, "E956", {"points": [v(-5.76, 7.84) * mm, v(-5.74, 7.9) * mm, v(-5.7, 7.9) * mm, v(-5.34, 7.92) * mm]});
            skFitSpline(sketch, "E957", {"points": [v(-5.34, 7.92) * mm, v(-5.01, 7.93) * mm, v(-4.83, 7.9) * mm, v(-4.59, 7.82) * mm]});
            skFitSpline(sketch, "E958", {"points": [v(-4.59, 7.82) * mm, v(-4.3, 7.73) * mm, v(-4.11, 7.6) * mm, v(-3.94, 7.39) * mm]});
            skFitSpline(sketch, "E959", {"points": [v(-3.94, 7.39) * mm, v(-3.77, 7.17) * mm, v(-3.72, 7.07) * mm, v(-3.7, 6.88) * mm]});
            skFitSpline(sketch, "E960", {"points": [v(-3.7, 6.88) * mm, v(-3.68, 6.72) * mm, v(-3.58, 6.29) * mm, v(-3.55, 6.18) * mm]});
            skFitSpline(sketch, "E961", {"points": [v(-3.55, 6.18) * mm, v(-3.47, 5.97) * mm, v(-3.36, 5.73) * mm, v(-3.22, 5.51) * mm]});
            skLineSegment(sketch, "E962", {"start": v(-3.22, 5.51) * mm, "end": v(-3.11, 5.34) * mm});
            skLineSegment(sketch, "E963", {"start": v(-3.11, 5.34) * mm, "end": v(-3.17, 5.25) * mm});
            skFitSpline(sketch, "E964", {"points": [v(-3.17, 5.25) * mm, v(-3.24, 5.14) * mm, v(-3.31, 4.95) * mm, v(-3.36, 4.8) * mm]});
            skFitSpline(sketch, "E965", {"points": [v(-3.36, 4.8) * mm, v(-3.42, 4.59) * mm, v(-3.43, 4.44) * mm, v(-3.43, 4.1) * mm]});
            skFitSpline(sketch, "E966", {"points": [v(-3.43, 4.1) * mm, v(-3.43, 3.91) * mm, v(-3.44, 3.76) * mm, v(-3.44, 3.77) * mm]});
            skFitSpline(sketch, "E967", {"points": [v(-3.44, 3.77) * mm, v(-3.45, 3.77) * mm, v(-3.5, 3.82) * mm, v(-3.56, 3.88) * mm]});
            skFitSpline(sketch, "E968", {"points": [v(3.25, 4.36) * mm, v(3.24, 4.57) * mm, v(3.16, 4.87) * mm, v(3.05, 5.12) * mm]});
            skLineSegment(sketch, "E969", {"start": v(3.05, 5.12) * mm, "end": v(2.97, 5.28) * mm});
            skLineSegment(sketch, "E970", {"start": v(2.97, 5.28) * mm, "end": v(3.04, 5.35) * mm});
            skFitSpline(sketch, "E971", {"points": [v(3.04, 5.35) * mm, v(3.22, 5.54) * mm, v(3.8, 6.17) * mm, v(3.84, 6.21) * mm]});
            skFitSpline(sketch, "E972", {"points": [v(3.84, 6.21) * mm, v(3.96, 6.37) * mm, v(3.96, 6.36) * mm, v(4.05, 6.34) * mm]});
            skFitSpline(sketch, "E973", {"points": [v(4.05, 6.34) * mm, v(4.1, 6.34) * mm, v(4.15, 6.32) * mm, v(4.17, 6.3) * mm]});
            skFitSpline(sketch, "E974", {"points": [v(4.17, 6.3) * mm, v(4.19, 6.3) * mm, v(4.21, 6.28) * mm, v(4.22, 6.28) * mm]});
            skFitSpline(sketch, "E975", {"points": [v(4.22, 6.28) * mm, v(4.24, 6.28) * mm, v(4.41, 6.46) * mm, v(4.61, 6.67) * mm]});
            skFitSpline(sketch, "E976", {"points": [v(4.61, 6.67) * mm, v(5.21, 7.29) * mm, v(5.39, 7.46) * mm, v(5.52, 7.55) * mm]});
            skFitSpline(sketch, "E977", {"points": [v(5.52, 7.55) * mm, v(5.6, 7.6) * mm, v(5.73, 7.7) * mm, v(5.82, 7.77) * mm]});
            skFitSpline(sketch, "E978", {"points": [v(5.82, 7.77) * mm, v(6, 7.9) * mm, v(6.04, 7.91) * mm, v(6.04, 7.87) * mm]});
            skFitSpline(sketch, "E979", {"points": [v(6.04, 7.87) * mm, v(6.04, 7.86) * mm, v(5.94, 7.7) * mm, v(5.82, 7.52) * mm]});
            skFitSpline(sketch, "E980", {"points": [v(5.82, 7.52) * mm, v(5.64, 7.25) * mm, v(5.58, 7.17) * mm, v(5.4, 6.98) * mm]});
            skFitSpline(sketch, "E981", {"points": [v(5.4, 6.98) * mm, v(5.29, 6.86) * mm, v(5.14, 6.7) * mm, v(5.08, 6.63) * mm]});
            skFitSpline(sketch, "E982", {"points": [v(5.08, 6.63) * mm, v(4.94, 6.49) * mm, v(4.75, 6.28) * mm, v(4.6, 6.13) * mm]});
            skFitSpline(sketch, "E983", {"points": [v(4.6, 6.13) * mm, v(4.55, 6.08) * mm, v(4.5, 6.02) * mm, v(4.5, 6.01) * mm]});
            skFitSpline(sketch, "E984", {"points": [v(4.5, 6.01) * mm, v(4.5, 6) * mm, v(4.52, 5.97) * mm, v(4.54, 5.94) * mm]});
            skFitSpline(sketch, "E985", {"points": [v(4.54, 5.94) * mm, v(4.55, 5.92) * mm, v(4.57, 5.86) * mm, v(4.58, 5.8) * mm]});
            skLineSegment(sketch, "E986", {"start": v(4.58, 5.8) * mm, "end": v(4.6, 5.72) * mm});
            skLineSegment(sketch, "E987", {"start": v(4.6, 5.72) * mm, "end": v(4.52, 5.65) * mm});
            skFitSpline(sketch, "E988", {"points": [v(4.52, 5.65) * mm, v(4.44, 5.58) * mm, v(4.44, 5.57) * mm, v(4.46, 5.53) * mm]});
            skFitSpline(sketch, "E989", {"points": [v(4.46, 5.53) * mm, v(4.49, 5.44) * mm, v(4.43, 5.3) * mm, v(4.32, 5.23) * mm]});
            skFitSpline(sketch, "E990", {"points": [v(4.32, 5.23) * mm, v(4.25, 5.18) * mm, v(4.18, 5.17) * mm, v(4.15, 5.2) * mm]});
            skFitSpline(sketch, "E991", {"points": [v(4.15, 5.2) * mm, v(4.14, 5.2) * mm, v(4.12, 5.22) * mm, v(4.12, 5.22) * mm]});
            skFitSpline(sketch, "E992", {"points": [v(4.12, 5.22) * mm, v(4.1, 5.22) * mm, v(3.95, 5.06) * mm, v(3.76, 4.85) * mm]});
            skFitSpline(sketch, "E993", {"points": [v(3.76, 4.85) * mm, v(3.57, 4.65) * mm, v(3.38, 4.45) * mm, v(3.33, 4.4) * mm]});
            skLineSegment(sketch, "E994", {"start": v(3.33, 4.4) * mm, "end": v(3.25, 4.3) * mm});
            skLineSegment(sketch, "E995", {"start": v(3.25, 4.3) * mm, "end": v(3.25, 4.36) * mm});
            skFitSpline(sketch, "E996", {"points": [v(-8.25, 4.41) * mm, v(-8.33, 4.45) * mm, v(-8.5, 4.52) * mm, v(-8.61, 4.57) * mm]});
            skFitSpline(sketch, "E997", {"points": [v(-8.61, 4.57) * mm, v(-8.73, 4.62) * mm, v(-8.89, 4.68) * mm, v(-8.97, 4.7) * mm]});
            skFitSpline(sketch, "E998", {"points": [v(-8.97, 4.7) * mm, v(-9.06, 4.73) * mm, v(-9.1, 4.75) * mm, v(-9.1, 4.76) * mm]});
            skFitSpline(sketch, "E999", {"points": [v(-9.1, 4.76) * mm, v(-9.1, 4.8) * mm, v(-9.01, 5.12) * mm, v(-8.96, 5.26) * mm]});
            skFitSpline(sketch, "E1000", {"points": [v(-8.96, 5.26) * mm, v(-8.86, 5.53) * mm, v(-8.74, 5.7) * mm, v(-8.6, 5.76) * mm]});
            skFitSpline(sketch, "E1001", {"points": [v(-8.6, 5.76) * mm, v(-8.53, 5.8) * mm, v(-8.5, 5.8) * mm, v(-8.42, 5.8) * mm]});
            skFitSpline(sketch, "E1002", {"points": [v(-8.42, 5.8) * mm, v(-8.25, 5.77) * mm, v(-7.93, 5.6) * mm, v(-7.8, 5.47) * mm]});
            skFitSpline(sketch, "E1003", {"points": [v(-7.8, 5.47) * mm, v(-7.65, 5.3) * mm, v(-7.67, 5.14) * mm, v(-7.87, 4.74) * mm]});
            skFitSpline(sketch, "E1004", {"points": [v(-7.87, 4.74) * mm, v(-7.9, 4.66) * mm, v(-7.96, 4.54) * mm, v(-7.98, 4.49) * mm]});
            skFitSpline(sketch, "E1005", {"points": [v(-7.98, 4.49) * mm, v(-8, 4.39) * mm, v(-8.03, 4.36) * mm, v(-8.08, 4.36) * mm]});
            skFitSpline(sketch, "E1006", {"points": [v(-8.08, 4.36) * mm, v(-8.1, 4.36) * mm, v(-8.17, 4.38) * mm, v(-8.25, 4.41) * mm]});
            skFitSpline(sketch, "E1007", {"points": [v(-8.1, 4.55) * mm, v(-8.1, 4.56) * mm, v(-8.08, 4.58) * mm, v(-8.08, 4.59) * mm]});
            skFitSpline(sketch, "E1008", {"points": [v(-8.08, 4.59) * mm, v(-8.08, 4.6) * mm, v(-8.03, 4.7) * mm, v(-7.98, 4.83) * mm]});
            skFitSpline(sketch, "E1009", {"points": [v(-7.98, 4.83) * mm, v(-7.9, 5.06) * mm, v(-7.9, 5.07) * mm, v(-7.89, 5.2) * mm]});
            skLineSegment(sketch, "E1010", {"start": v(-7.89, 5.2) * mm, "end": v(-7.89, 5.35) * mm});
            skLineSegment(sketch, "E1011", {"start": v(-7.89, 5.35) * mm, "end": v(-7.98, 5.42) * mm});
            skFitSpline(sketch, "E1012", {"points": [v(-7.98, 5.42) * mm, v(-8.1, 5.53) * mm, v(-8.36, 5.65) * mm, v(-8.45, 5.65) * mm]});
            skFitSpline(sketch, "E1013", {"points": [v(-8.45, 5.65) * mm, v(-8.49, 5.65) * mm, v(-8.52, 5.64) * mm, v(-8.53, 5.63) * mm]});
            skFitSpline(sketch, "E1014", {"points": [v(-8.53, 5.63) * mm, v(-8.55, 5.62) * mm, v(-8.54, 5.62) * mm, v(-8.52, 5.62) * mm]});
            skFitSpline(sketch, "E1015", {"points": [v(-8.52, 5.62) * mm, v(-8.47, 5.62) * mm, v(-8.47, 5.6) * mm, v(-8.52, 5.55) * mm]});
            skFitSpline(sketch, "E1016", {"points": [v(-8.52, 5.55) * mm, v(-8.59, 5.48) * mm, v(-8.65, 5.37) * mm, v(-8.73, 5.18) * mm]});
            skFitSpline(sketch, "E1017", {"points": [v(-8.73, 5.18) * mm, v(-8.81, 4.98) * mm, v(-8.85, 4.92) * mm, v(-8.87, 4.94) * mm]});
            skFitSpline(sketch, "E1018", {"points": [v(-8.87, 4.94) * mm, v(-8.88, 4.95) * mm, v(-8.85, 5.02) * mm, v(-8.81, 5.1) * mm]});
            skFitSpline(sketch, "E1019", {"points": [v(-8.81, 5.1) * mm, v(-8.75, 5.26) * mm, v(-8.7, 5.42) * mm, v(-8.7, 5.43) * mm]});
            skFitSpline(sketch, "E1020", {"points": [v(-8.7, 5.43) * mm, v(-8.71, 5.44) * mm, v(-8.76, 5.35) * mm, v(-8.85, 5.18) * mm]});
            skFitSpline(sketch, "E1021", {"points": [v(-8.85, 5.18) * mm, v(-8.93, 5.01) * mm, v(-8.98, 4.88) * mm, v(-8.96, 4.86) * mm]});
            skFitSpline(sketch, "E1022", {"points": [v(-8.96, 4.86) * mm, v(-8.93, 4.8) * mm, v(-8.75, 4.71) * mm, v(-8.53, 4.64) * mm]});
            skFitSpline(sketch, "E1023", {"points": [v(-8.53, 4.64) * mm, v(-8.4, 4.6) * mm, v(-8.28, 4.56) * mm, v(-8.25, 4.55) * mm]});
            skFitSpline(sketch, "E1024", {"points": [v(-8.25, 4.55) * mm, v(-8.19, 4.52) * mm, v(-8.15, 4.52) * mm, v(-8.1, 4.55) * mm]});
            skLineSegment(sketch, "E1025", {"start": v(-8.1, 4.55) * mm, "end": v(-8.1, 4.55) * mm});
            skFitSpline(sketch, "E1026", {"points": [v(3.3, 8.76) * mm, v(3.3, 8.77) * mm, v(3.27, 8.8) * mm, v(3.26, 8.8) * mm]});
            skFitSpline(sketch, "E1027", {"points": [v(3.26, 8.8) * mm, v(3.25, 8.83) * mm, v(3.26, 8.82) * mm, v(3.3, 8.8) * mm]});
            skFitSpline(sketch, "E1028", {"points": [v(3.3, 8.8) * mm, v(3.33, 8.77) * mm, v(3.36, 8.75) * mm, v(3.37, 8.75) * mm]});
            skFitSpline(sketch, "E1029", {"points": [v(3.37, 8.75) * mm, v(3.37, 8.74) * mm, v(3.36, 8.74) * mm, v(3.35, 8.74) * mm]});
            skFitSpline(sketch, "E1030", {"points": [v(3.35, 8.74) * mm, v(3.34, 8.74) * mm, v(3.32, 8.75) * mm, v(3.3, 8.76) * mm]});
            skFitSpline(sketch, "E1031", {"points": [v(3.45, 8.79) * mm, v(3.43, 8.8) * mm, v(3.4, 8.81) * mm, v(3.36, 8.83) * mm]});
            skFitSpline(sketch, "E1032", {"points": [v(3.36, 8.83) * mm, v(3.3, 8.85) * mm, v(3.3, 8.86) * mm, v(3.28, 8.92) * mm]});
            skFitSpline(sketch, "E1033", {"points": [v(3.28, 8.92) * mm, v(3.24, 9.16) * mm, v(3.08, 9.76) * mm, v(3.05, 9.76) * mm]});
            skFitSpline(sketch, "E1034", {"points": [v(3.05, 9.76) * mm, v(3.04, 9.76) * mm, v(3.06, 9.53) * mm, v(3.07, 9.47) * mm]});
            skFitSpline(sketch, "E1035", {"points": [v(3.07, 9.47) * mm, v(3.08, 9.45) * mm, v(3.07, 9.47) * mm, v(3.05, 9.52) * mm]});
            skFitSpline(sketch, "E1036", {"points": [v(3.05, 9.52) * mm, v(3, 9.67) * mm, v(2.97, 9.71) * mm, v(2.94, 9.7) * mm]});
            skFitSpline(sketch, "E1037", {"points": [v(2.94, 9.7) * mm, v(2.9, 9.7) * mm, v(2.9, 9.76) * mm, v(2.96, 9.86) * mm]});
            skFitSpline(sketch, "E1038", {"points": [v(2.96, 9.86) * mm, v(3, 9.97) * mm, v(3.02, 10.05) * mm, v(2.98, 10.08) * mm]});
            skFitSpline(sketch, "E1039", {"points": [v(2.98, 10.08) * mm, v(2.94, 10.1) * mm, v(2.9, 10.07) * mm, v(2.85, 10) * mm]});
            skFitSpline(sketch, "E1040", {"points": [v(2.85, 10) * mm, v(2.82, 9.93) * mm, v(2.74, 9.65) * mm, v(2.64, 9.28) * mm]});
            skFitSpline(sketch, "E1041", {"points": [v(2.64, 9.28) * mm, v(2.6, 9.16) * mm, v(2.6, 9.15) * mm, v(2.56, 9.15) * mm]});
            skFitSpline(sketch, "E1042", {"points": [v(2.56, 9.15) * mm, v(2.53, 9.15) * mm, v(2.51, 9.16) * mm, v(2.5, 9.19) * mm]});
            skFitSpline(sketch, "E1043", {"points": [v(2.5, 9.19) * mm, v(2.49, 9.22) * mm, v(2.5, 9.25) * mm, v(2.54, 9.37) * mm]});
            skFitSpline(sketch, "E1044", {"points": [v(2.54, 9.37) * mm, v(2.57, 9.44) * mm, v(2.62, 9.61) * mm, v(2.66, 9.74) * mm]});
            skFitSpline(sketch, "E1045", {"points": [v(2.66, 9.74) * mm, v(2.8, 10.24) * mm, v(2.82, 10.26) * mm, v(2.97, 10.2) * mm]});
            skFitSpline(sketch, "E1046", {"points": [v(2.97, 10.2) * mm, v(3.01, 10.2) * mm, v(3.06, 10.17) * mm, v(3.06, 10.16) * mm]});
            skFitSpline(sketch, "E1047", {"points": [v(3.06, 10.16) * mm, v(3.1, 10.12) * mm, v(3.32, 9.4) * mm, v(3.38, 9.12) * mm]});
            skFitSpline(sketch, "E1048", {"points": [v(3.38, 9.12) * mm, v(3.4, 9) * mm, v(3.43, 8.96) * mm, v(3.46, 9) * mm]});
            skFitSpline(sketch, "E1049", {"points": [v(3.46, 9) * mm, v(3.47, 9) * mm, v(3.46, 9.06) * mm, v(3.44, 9.13) * mm]});
            skLineSegment(sketch, "E1050", {"start": v(3.44, 9.13) * mm, "end": v(3.41, 9.24) * mm});
            skLineSegment(sketch, "E1051", {"start": v(3.41, 9.24) * mm, "end": v(3.48, 9.32) * mm});
            skFitSpline(sketch, "E1052", {"points": [v(3.48, 9.32) * mm, v(3.51, 9.36) * mm, v(3.57, 9.45) * mm, v(3.6, 9.51) * mm]});
            skFitSpline(sketch, "E1053", {"points": [v(3.6, 9.51) * mm, v(3.64, 9.58) * mm, v(3.68, 9.64) * mm, v(3.68, 9.63) * mm]});
            skFitSpline(sketch, "E1054", {"points": [v(3.68, 9.63) * mm, v(3.68, 9.63) * mm, v(3.65, 9.53) * mm, v(3.6, 9.41) * mm]});
            skFitSpline(sketch, "E1055", {"points": [v(3.6, 9.41) * mm, v(3.56, 9.3) * mm, v(3.52, 9.2) * mm, v(3.53, 9.19) * mm]});
            skFitSpline(sketch, "E1056", {"points": [v(3.53, 9.19) * mm, v(3.54, 9.17) * mm, v(3.63, 9.33) * mm, v(3.7, 9.5) * mm]});
            skFitSpline(sketch, "E1057", {"points": [v(3.7, 9.5) * mm, v(3.75, 9.64) * mm, v(3.78, 9.7) * mm, v(3.83, 9.75) * mm]});
            skFitSpline(sketch, "E1058", {"points": [v(3.83, 9.75) * mm, v(3.89, 9.82) * mm, v(3.9, 9.82) * mm, v(3.92, 9.8) * mm]});
            skFitSpline(sketch, "E1059", {"points": [v(3.92, 9.8) * mm, v(3.95, 9.8) * mm, v(3.95, 9.78) * mm, v(3.95, 9.73) * mm]});
            skFitSpline(sketch, "E1060", {"points": [v(3.95, 9.73) * mm, v(3.95, 9.67) * mm, v(3.9, 9.56) * mm, v(3.73, 9.23) * mm]});
            skFitSpline(sketch, "E1061", {"points": [v(3.73, 9.23) * mm, v(3.62, 8.99) * mm, v(3.51, 8.79) * mm, v(3.5, 8.78) * mm]});
            skFitSpline(sketch, "E1062", {"points": [v(3.5, 8.78) * mm, v(3.5, 8.78) * mm, v(3.47, 8.78) * mm, v(3.45, 8.79) * mm]});
            skFitSpline(sketch, "E1063", {"points": [v(-3.8, 8.94) * mm, v(-3.81, 8.98) * mm, v(-3.9, 9.16) * mm, v(-3.97, 9.33) * mm]});
            skFitSpline(sketch, "E1064", {"points": [v(-3.97, 9.33) * mm, v(-4.05, 9.5) * mm, v(-4.14, 9.68) * mm, v(-4.16, 9.73) * mm]});
            skLineSegment(sketch, "E1065", {"start": v(-4.16, 9.73) * mm, "end": v(-4.21, 9.84) * mm});
            skLineSegment(sketch, "E1066", {"start": v(-4.21, 9.84) * mm, "end": v(-4.18, 9.87) * mm});
            skFitSpline(sketch, "E1067", {"points": [v(-4.18, 9.87) * mm, v(-4.13, 9.9) * mm, v(-4.09, 9.9) * mm, v(-4.06, 9.85) * mm]});
            skFitSpline(sketch, "E1068", {"points": [v(-4.06, 9.85) * mm, v(-4.05, 9.83) * mm, v(-3.96, 9.63) * mm, v(-3.86, 9.42) * mm]});
            skLineSegment(sketch, "E1069", {"start": v(-3.86, 9.42) * mm, "end": v(-3.68, 9.02) * mm});
            skLineSegment(sketch, "E1070", {"start": v(-3.68, 9.02) * mm, "end": v(-3.63, 9.03) * mm});
            skFitSpline(sketch, "E1071", {"points": [v(-3.63, 9.03) * mm, v(-3.6, 9.03) * mm, v(-3.5, 9.07) * mm, v(-3.4, 9.1) * mm]});
            skFitSpline(sketch, "E1072", {"points": [v(-3.4, 9.1) * mm, v(-3.19, 9.21) * mm, v(-3.14, 9.23) * mm, v(-3.05, 9.23) * mm]});
            skFitSpline(sketch, "E1073", {"points": [v(-3.05, 9.23) * mm, v(-2.97, 9.23) * mm, v(-2.95, 9.2) * mm, v(-2.97, 9.15) * mm]});
            skFitSpline(sketch, "E1074", {"points": [v(-2.97, 9.15) * mm, v(-2.98, 9.12) * mm, v(-3.02, 9.1) * mm, v(-3.11, 9.07) * mm]});
            skFitSpline(sketch, "E1075", {"points": [v(-3.11, 9.07) * mm, v(-3.18, 9.05) * mm, v(-3.34, 8.99) * mm, v(-3.47, 8.94) * mm]});
            skFitSpline(sketch, "E1076", {"points": [v(-3.47, 8.94) * mm, v(-3.6, 8.89) * mm, v(-3.71, 8.85) * mm, v(-3.73, 8.85) * mm]});
            skFitSpline(sketch, "E1077", {"points": [v(-3.73, 8.85) * mm, v(-3.74, 8.85) * mm, v(-3.77, 8.88) * mm, v(-3.8, 8.94) * mm]});
            skFitSpline(sketch, "E1078", {"points": [v(1.8, 9.39) * mm, v(1.8, 9.42) * mm, v(1.8, 9.45) * mm, v(1.82, 9.53) * mm]});
            skFitSpline(sketch, "E1079", {"points": [v(1.82, 9.53) * mm, v(1.86, 9.67) * mm, v(1.86, 9.72) * mm, v(1.81, 9.77) * mm]});
            skLineSegment(sketch, "E1080", {"start": v(1.81, 9.77) * mm, "end": v(1.78, 9.81) * mm});
            skLineSegment(sketch, "E1081", {"start": v(1.78, 9.81) * mm, "end": v(1.8, 9.75) * mm});
            skFitSpline(sketch, "E1082", {"points": [v(1.8, 9.75) * mm, v(1.8, 9.7) * mm, v(1.8, 9.67) * mm, v(1.78, 9.58) * mm]});
            skFitSpline(sketch, "E1083", {"points": [v(1.78, 9.58) * mm, v(1.75, 9.46) * mm, v(1.73, 9.48) * mm, v(1.73, 9.61) * mm]});
            skFitSpline(sketch, "E1084", {"points": [v(1.73, 9.61) * mm, v(1.73, 9.72) * mm, v(1.71, 9.75) * mm, v(1.59, 9.77) * mm]});
            skFitSpline(sketch, "E1085", {"points": [v(1.59, 9.77) * mm, v(1.46, 9.8) * mm, v(1.27, 9.82) * mm, v(1.22, 9.81) * mm]});
            skFitSpline(sketch, "E1086", {"points": [v(1.22, 9.81) * mm, v(1.16, 9.8) * mm, v(1.15, 9.82) * mm, v(1.2, 9.88) * mm]});
            skFitSpline(sketch, "E1087", {"points": [v(1.2, 9.88) * mm, v(1.24, 9.91) * mm, v(1.24, 9.91) * mm, v(1.2, 9.93) * mm]});
            skFitSpline(sketch, "E1088", {"points": [v(1.2, 9.93) * mm, v(1.16, 9.97) * mm, v(1.11, 9.96) * mm, v(1.08, 9.92) * mm]});
            skFitSpline(sketch, "E1089", {"points": [v(1.08, 9.92) * mm, v(1.07, 9.9) * mm, v(1.05, 9.83) * mm, v(1.05, 9.74) * mm]});
            skFitSpline(sketch, "E1090", {"points": [v(1.05, 9.74) * mm, v(1.04, 9.6) * mm, v(1.02, 9.54) * mm, v(0.97, 9.52) * mm]});
            skFitSpline(sketch, "E1091", {"points": [v(0.97, 9.52) * mm, v(0.95, 9.5) * mm, v(0.94, 9.5) * mm, v(0.91, 9.54) * mm]});
            skFitSpline(sketch, "E1092", {"points": [v(0.91, 9.54) * mm, v(0.88, 9.58) * mm, v(0.88, 9.59) * mm, v(0.92, 9.76) * mm]});
            skFitSpline(sketch, "E1093", {"points": [v(0.92, 9.76) * mm, v(0.94, 9.85) * mm, v(0.97, 10.08) * mm, v(0.98, 10.27) * mm]});
            skFitSpline(sketch, "E1094", {"points": [v(0.98, 10.27) * mm, v(1.02, 10.68) * mm, v(1.01, 10.66) * mm, v(1.21, 10.65) * mm]});
            skFitSpline(sketch, "E1095", {"points": [v(1.21, 10.65) * mm, v(1.53, 10.62) * mm, v(1.79, 10.57) * mm, v(1.93, 10.5) * mm]});
            skFitSpline(sketch, "E1096", {"points": [v(1.93, 10.5) * mm, v(2, 10.46) * mm, v(2.09, 10.38) * mm, v(2.1, 10.31) * mm]});
            skFitSpline(sketch, "E1097", {"points": [v(2.1, 10.31) * mm, v(2.13, 10.24) * mm, v(2.12, 10.08) * mm, v(2.08, 10) * mm]});
            skFitSpline(sketch, "E1098", {"points": [v(2.08, 10) * mm, v(2.07, 9.98) * mm, v(2.03, 9.93) * mm, v(2, 9.92) * mm]});
            skFitSpline(sketch, "E1099", {"points": [v(2, 9.92) * mm, v(1.97, 9.9) * mm, v(1.96, 9.88) * mm, v(1.97, 9.86) * mm]});
            skFitSpline(sketch, "E1100", {"points": [v(1.97, 9.86) * mm, v(1.97, 9.85) * mm, v(1.98, 9.8) * mm, v(1.98, 9.73) * mm]});
            skFitSpline(sketch, "E1101", {"points": [v(1.98, 9.73) * mm, v(1.99, 9.64) * mm, v(1.98, 9.6) * mm, v(1.94, 9.49) * mm]});
            skFitSpline(sketch, "E1102", {"points": [v(1.94, 9.49) * mm, v(1.9, 9.37) * mm, v(1.9, 9.36) * mm, v(1.86, 9.35) * mm]});
            skFitSpline(sketch, "E1103", {"points": [v(1.86, 9.35) * mm, v(1.83, 9.35) * mm, v(1.82, 9.36) * mm, v(1.8, 9.39) * mm]});
            skFitSpline(sketch, "E1104", {"points": [v(1.8, 10.02) * mm, v(1.83, 10.03) * mm, v(1.86, 10.08) * mm, v(1.87, 10.16) * mm]});
            skFitSpline(sketch, "E1105", {"points": [v(1.87, 10.16) * mm, v(1.89, 10.27) * mm, v(1.74, 10.33) * mm, v(1.41, 10.37) * mm]});
            skFitSpline(sketch, "E1106", {"points": [v(1.41, 10.37) * mm, v(1.33, 10.37) * mm, v(1.25, 10.38) * mm, v(1.25, 10.38) * mm]});
            skFitSpline(sketch, "E1107", {"points": [v(1.25, 10.38) * mm, v(1.25, 10.38) * mm, v(1.24, 10.4) * mm, v(1.24, 10.43) * mm]});
            skFitSpline(sketch, "E1108", {"points": [v(1.24, 10.43) * mm, v(1.24, 10.48) * mm, v(1.22, 10.52) * mm, v(1.2, 10.5) * mm]});
            skFitSpline(sketch, "E1109", {"points": [v(1.2, 10.5) * mm, v(1.2, 10.5) * mm, v(1.17, 10.4) * mm, v(1.15, 10.31) * mm]});
            skFitSpline(sketch, "E1110", {"points": [v(1.15, 10.31) * mm, v(1.11, 10.16) * mm, v(1.1, 10.13) * mm, v(1.13, 10.11) * mm]});
            skFitSpline(sketch, "E1111", {"points": [v(1.13, 10.11) * mm, v(1.15, 10.1) * mm, v(1.16, 10.1) * mm, v(1.23, 10.1) * mm]});
            skFitSpline(sketch, "E1112", {"points": [v(1.23, 10.1) * mm, v(1.31, 10.13) * mm, v(1.39, 10.12) * mm, v(1.6, 10.05) * mm]});
            skFitSpline(sketch, "E1113", {"points": [v(1.6, 10.05) * mm, v(1.76, 10) * mm, v(1.75, 10) * mm, v(1.8, 10.02) * mm]});
            skFitSpline(sketch, "E1114", {"points": [v(1.91, 10.03) * mm, v(1.97, 10.1) * mm, v(1.99, 10.26) * mm, v(1.94, 10.33) * mm]});
            skFitSpline(sketch, "E1115", {"points": [v(1.94, 10.33) * mm, v(1.9, 10.38) * mm, v(1.89, 10.37) * mm, v(1.92, 10.3) * mm]});
            skFitSpline(sketch, "E1116", {"points": [v(1.92, 10.3) * mm, v(1.94, 10.25) * mm, v(1.94, 10.22) * mm, v(1.93, 10.16) * mm]});
            skFitSpline(sketch, "E1117", {"points": [v(1.93, 10.16) * mm, v(1.92, 10.1) * mm, v(1.9, 10.06) * mm, v(1.89, 10.04) * mm]});
            skFitSpline(sketch, "E1118", {"points": [v(1.89, 10.04) * mm, v(1.86, 10) * mm, v(1.88, 9.99) * mm, v(1.91, 10.03) * mm]});
            skFitSpline(sketch, "E1119", {"points": [v(-2.27, 9.38) * mm, v(-2.32, 9.43) * mm, v(-2.34, 9.52) * mm, v(-2.4, 9.81) * mm]});
            skFitSpline(sketch, "E1120", {"points": [v(-2.4, 9.81) * mm, v(-2.44, 9.99) * mm, v(-2.5, 10.2) * mm, v(-2.51, 10.27) * mm]});
            skLineSegment(sketch, "E1121", {"start": v(-2.51, 10.27) * mm, "end": v(-2.55, 10.42) * mm});
            skLineSegment(sketch, "E1122", {"start": v(-2.55, 10.42) * mm, "end": v(-2.5, 10.46) * mm});
            skFitSpline(sketch, "E1123", {"points": [v(-2.5, 10.46) * mm, v(-2.37, 10.57) * mm, v(-1.73, 10.69) * mm, v(-1.58, 10.63) * mm]});
            skFitSpline(sketch, "E1124", {"points": [v(-1.58, 10.63) * mm, v(-1.54, 10.61) * mm, v(-1.54, 10.6) * mm, v(-1.55, 10.57) * mm]});
            skFitSpline(sketch, "E1125", {"points": [v(-1.55, 10.57) * mm, v(-1.56, 10.55) * mm, v(-1.58, 10.53) * mm, v(-1.6, 10.53) * mm]});
            skFitSpline(sketch, "E1126", {"points": [v(-1.6, 10.53) * mm, v(-1.62, 10.53) * mm, v(-1.64, 10.53) * mm, v(-1.66, 10.52) * mm]});
            skFitSpline(sketch, "E1127", {"points": [v(-1.66, 10.52) * mm, v(-1.67, 10.5) * mm, v(-1.67, 10.5) * mm, v(-1.65, 10.48) * mm]});
            skFitSpline(sketch, "E1128", {"points": [v(-1.65, 10.48) * mm, v(-1.63, 10.45) * mm, v(-1.63, 10.45) * mm, v(-1.68, 10.43) * mm]});
            skFitSpline(sketch, "E1129", {"points": [v(-1.68, 10.43) * mm, v(-1.72, 10.42) * mm, v(-1.85, 10.4) * mm, v(-1.98, 10.36) * mm]});
            skFitSpline(sketch, "E1130", {"points": [v(-1.98, 10.36) * mm, v(-2.27, 10.3) * mm, v(-2.3, 10.3) * mm, v(-2.24, 10.16) * mm]});
            skLineSegment(sketch, "E1131", {"start": v(-2.24, 10.16) * mm, "end": v(-2.22, 10.11) * mm});
            skLineSegment(sketch, "E1132", {"start": v(-2.22, 10.11) * mm, "end": v(-2.05, 10.13) * mm});
            skFitSpline(sketch, "E1133", {"points": [v(-2.05, 10.13) * mm, v(-1.95, 10.15) * mm, v(-1.84, 10.15) * mm, v(-1.8, 10.15) * mm]});
            skFitSpline(sketch, "E1134", {"points": [v(-1.8, 10.15) * mm, v(-1.61, 10.13) * mm, v(-1.55, 10.03) * mm, v(-1.7, 10) * mm]});
            skFitSpline(sketch, "E1135", {"points": [v(-1.7, 10) * mm, v(-1.72, 9.99) * mm, v(-1.73, 9.98) * mm, v(-1.72, 9.96) * mm]});
            skFitSpline(sketch, "E1136", {"points": [v(-1.72, 9.96) * mm, v(-1.7, 9.95) * mm, v(-1.75, 9.93) * mm, v(-1.9, 9.89) * mm]});
            skFitSpline(sketch, "E1137", {"points": [v(-1.9, 9.89) * mm, v(-2, 9.86) * mm, v(-2.1, 9.82) * mm, v(-2.1, 9.8) * mm]});
            skFitSpline(sketch, "E1138", {"points": [v(-2.1, 9.8) * mm, v(-2.12, 9.8) * mm, v(-2.13, 9.76) * mm, v(-2.13, 9.72) * mm]});
            skFitSpline(sketch, "E1139", {"points": [v(-2.13, 9.72) * mm, v(-2.13, 9.67) * mm, v(-2.13, 9.67) * mm, v(-2.16, 9.78) * mm]});
            skFitSpline(sketch, "E1140", {"points": [v(-2.16, 9.78) * mm, v(-2.18, 9.84) * mm, v(-2.2, 9.9) * mm, v(-2.2, 9.9) * mm]});
            skFitSpline(sketch, "E1141", {"points": [v(-2.2, 9.9) * mm, v(-2.2, 9.9) * mm, v(-2.22, 9.88) * mm, v(-2.24, 9.87) * mm]});
            skFitSpline(sketch, "E1142", {"points": [v(-2.24, 9.87) * mm, v(-2.26, 9.84) * mm, v(-2.26, 9.83) * mm, v(-2.25, 9.74) * mm]});
            skFitSpline(sketch, "E1143", {"points": [v(-2.25, 9.74) * mm, v(-2.23, 9.62) * mm, v(-2.19, 9.55) * mm, v(-2.14, 9.54) * mm]});
            skFitSpline(sketch, "E1144", {"points": [v(-2.14, 9.54) * mm, v(-2.1, 9.53) * mm, v(-2.1, 9.54) * mm, v(-2.12, 9.6) * mm]});
            skFitSpline(sketch, "E1145", {"points": [v(-2.12, 9.6) * mm, v(-2.12, 9.63) * mm, v(-2.12, 9.65) * mm, v(-2.12, 9.64) * mm]});
            skFitSpline(sketch, "E1146", {"points": [v(-2.12, 9.64) * mm, v(-2.1, 9.61) * mm, v(-1.96, 9.62) * mm, v(-1.8, 9.65) * mm]});
            skFitSpline(sketch, "E1147", {"points": [v(-1.8, 9.65) * mm, v(-1.66, 9.68) * mm, v(-1.54, 9.7) * mm, v(-1.58, 9.67) * mm]});
            skFitSpline(sketch, "E1148", {"points": [v(-1.58, 9.67) * mm, v(-1.59, 9.66) * mm, v(-1.56, 9.65) * mm, v(-1.5, 9.65) * mm]});
            skFitSpline(sketch, "E1149", {"points": [v(-1.5, 9.65) * mm, v(-1.45, 9.64) * mm, v(-1.4, 9.63) * mm, v(-1.39, 9.62) * mm]});
            skFitSpline(sketch, "E1150", {"points": [v(-1.39, 9.62) * mm, v(-1.36, 9.6) * mm, v(-1.36, 9.56) * mm, v(-1.39, 9.53) * mm]});
            skFitSpline(sketch, "E1151", {"points": [v(-1.39, 9.53) * mm, v(-1.4, 9.52) * mm, v(-1.52, 9.5) * mm, v(-1.67, 9.47) * mm]});
            skFitSpline(sketch, "E1152", {"points": [v(-1.67, 9.47) * mm, v(-1.8, 9.45) * mm, v(-1.98, 9.41) * mm, v(-2.06, 9.4) * mm]});
            skFitSpline(sketch, "E1153", {"points": [v(-2.06, 9.4) * mm, v(-2.22, 9.36) * mm, v(-2.25, 9.36) * mm, v(-2.27, 9.38) * mm]});
            skFitSpline(sketch, "E1154", {"points": [v(-2.21, 10.06) * mm, v(-2.21, 10.06) * mm, v(-2.22, 10.1) * mm, v(-2.24, 10.13) * mm]});
            skFitSpline(sketch, "E1155", {"points": [v(-2.24, 10.13) * mm, v(-2.26, 10.17) * mm, v(-2.29, 10.24) * mm, v(-2.3, 10.3) * mm]});
            skFitSpline(sketch, "E1156", {"points": [v(-2.3, 10.3) * mm, v(-2.31, 10.38) * mm, v(-2.32, 10.38) * mm, v(-2.33, 10.36) * mm]});
            skFitSpline(sketch, "E1157", {"points": [v(-2.33, 10.36) * mm, v(-2.36, 10.32) * mm, v(-2.36, 10.2) * mm, v(-2.34, 10.11) * mm]});
            skFitSpline(sketch, "E1158", {"points": [v(-2.34, 10.11) * mm, v(-2.32, 10.05) * mm, v(-2.32, 10.05) * mm, v(-2.27, 10.05) * mm]});
            skFitSpline(sketch, "E1159", {"points": [v(-2.27, 10.05) * mm, v(-2.24, 10.05) * mm, v(-2.22, 10.05) * mm, v(-2.21, 10.06) * mm]});
            skFitSpline(sketch, "E1160", {"points": [v(-1.85, 9.39) * mm, v(-1.71, 9.42) * mm, v(-1.66, 9.43) * mm, v(-1.68, 9.41) * mm]});
            skFitSpline(sketch, "E1161", {"points": [v(-1.68, 9.41) * mm, v(-1.7, 9.4) * mm, v(-1.86, 9.36) * mm, v(-1.9, 9.37) * mm]});
            skFitSpline(sketch, "E1162", {"points": [v(-1.9, 9.37) * mm, v(-1.91, 9.37) * mm, v(-1.89, 9.38) * mm, v(-1.85, 9.39) * mm]});
            skFitSpline(sketch, "E1163", {"points": [v(0.25, 9.61) * mm, v(0.24, 9.62) * mm, v(0.22, 9.67) * mm, v(0.2, 9.71) * mm]});
            skFitSpline(sketch, "E1164", {"points": [v(0.2, 9.71) * mm, v(0.16, 9.84) * mm, v(0.11, 9.88) * mm, v(0.06, 9.83) * mm]});
            skFitSpline(sketch, "E1165", {"points": [v(0.06, 9.83) * mm, v(0.05, 9.82) * mm, v(0.05, 9.8) * mm, v(0.07, 9.8) * mm]});
            skFitSpline(sketch, "E1166", {"points": [v(0.07, 9.8) * mm, v(0.1, 9.78) * mm, v(0.07, 9.77) * mm, v(-0.1, 9.77) * mm]});
            skFitSpline(sketch, "E1167", {"points": [v(-0.1, 9.77) * mm, v(-0.2, 9.77) * mm, v(-0.3, 9.78) * mm, v(-0.3, 9.79) * mm]});
            skFitSpline(sketch, "E1168", {"points": [v(-0.3, 9.79) * mm, v(-0.3, 9.8) * mm, v(-0.28, 9.8) * mm, v(-0.25, 9.8) * mm]});
            skFitSpline(sketch, "E1169", {"points": [v(-0.25, 9.8) * mm, v(-0.21, 9.79) * mm, v(-0.14, 9.8) * mm, v(-0.08, 9.8) * mm]});
            skFitSpline(sketch, "E1170", {"points": [v(-0.08, 9.8) * mm, v(0.06, 9.81) * mm, v(0, 9.83) * mm, v(-0.27, 9.85) * mm]});
            skFitSpline(sketch, "E1171", {"points": [v(-0.27, 9.85) * mm, v(-0.52, 9.87) * mm, v(-0.54, 9.86) * mm, v(-0.58, 9.77) * mm]});
            skFitSpline(sketch, "E1172", {"points": [v(-0.58, 9.77) * mm, v(-0.62, 9.64) * mm, v(-0.64, 9.61) * mm, v(-0.7, 9.6) * mm]});
            skFitSpline(sketch, "E1173", {"points": [v(-0.7, 9.6) * mm, v(-0.76, 9.6) * mm, v(-0.76, 9.61) * mm, v(-0.7, 9.82) * mm]});
            skFitSpline(sketch, "E1174", {"points": [v(-0.7, 9.82) * mm, v(-0.57, 10.2) * mm, v(-0.38, 10.66) * mm, v(-0.31, 10.72) * mm]});
            skFitSpline(sketch, "E1175", {"points": [v(-0.31, 10.72) * mm, v(-0.3, 10.74) * mm, v(-0.26, 10.75) * mm, v(-0.2, 10.75) * mm]});
            skFitSpline(sketch, "E1176", {"points": [v(-0.2, 10.75) * mm, v(-0.04, 10.74) * mm, v(-0.05, 10.75) * mm, v(0.03, 10.54) * mm]});
            skFitSpline(sketch, "E1177", {"points": [v(0.03, 10.54) * mm, v(0.06, 10.43) * mm, v(0.14, 10.23) * mm, v(0.19, 10.1) * mm]});
            skFitSpline(sketch, "E1178", {"points": [v(0.19, 10.1) * mm, v(0.24, 9.95) * mm, v(0.3, 9.8) * mm, v(0.32, 9.74) * mm]});
            skFitSpline(sketch, "E1179", {"points": [v(0.32, 9.74) * mm, v(0.35, 9.64) * mm, v(0.35, 9.63) * mm, v(0.33, 9.61) * mm]});
            skFitSpline(sketch, "E1180", {"points": [v(0.33, 9.61) * mm, v(0.29, 9.59) * mm, v(0.27, 9.59) * mm, v(0.25, 9.61) * mm]});
            skFitSpline(sketch, "E1181", {"points": [v(-0.37, 10.02) * mm, v(-0.35, 10.04) * mm, v(0.01, 10.04) * mm, v(0.03, 10.02) * mm]});
            skFitSpline(sketch, "E1182", {"points": [v(0.03, 10.02) * mm, v(0.06, 10) * mm, v(0.1, 10) * mm, v(0.08, 10.03) * mm]});
            skFitSpline(sketch, "E1183", {"points": [v(0.08, 10.03) * mm, v(0.07, 10.04) * mm, v(0.03, 10.14) * mm, v(0, 10.24) * mm]});
            skFitSpline(sketch, "E1184", {"points": [v(0, 10.24) * mm, v(-0.07, 10.44) * mm, v(-0.15, 10.62) * mm, v(-0.17, 10.62) * mm]});
            skFitSpline(sketch, "E1185", {"points": [v(-0.17, 10.62) * mm, v(-0.17, 10.62) * mm, v(-0.19, 10.6) * mm, v(-0.2, 10.57) * mm]});
            skFitSpline(sketch, "E1186", {"points": [v(-0.2, 10.57) * mm, v(-0.21, 10.55) * mm, v(-0.24, 10.5) * mm, v(-0.28, 10.46) * mm]});
            skFitSpline(sketch, "E1187", {"points": [v(-0.28, 10.46) * mm, v(-0.34, 10.39) * mm, v(-0.37, 10.34) * mm, v(-0.44, 10.17) * mm]});
            skFitSpline(sketch, "E1188", {"points": [v(-0.44, 10.17) * mm, v(-0.47, 10.1) * mm, v(-0.5, 10.03) * mm, v(-0.5, 10.02) * mm]});
            skFitSpline(sketch, "E1189", {"points": [v(-0.5, 10.02) * mm, v(-0.5, 10) * mm, v(-0.4, 10) * mm, v(-0.37, 10.02) * mm]});
            skFitSpline(sketch, "E1190", {"points": [v(-0.2, 10.43) * mm, v(-0.2, 10.45) * mm, v(-0.18, 10.49) * mm, v(-0.17, 10.49) * mm]});
            skFitSpline(sketch, "E1191", {"points": [v(-0.17, 10.49) * mm, v(-0.14, 10.49) * mm, v(-0.15, 10.43) * mm, v(-0.18, 10.42) * mm]});
            skFitSpline(sketch, "E1192", {"points": [v(-0.18, 10.42) * mm, v(-0.19, 10.42) * mm, v(-0.2, 10.42) * mm, v(-0.2, 10.43) * mm]});
            skSolve(sketch);
        }
        {
            var Q0;
            Q0=makeQuery(id+"F2.imprint","IMPRINT",FACE,{"disambiguationData":[TD([[makeQuery(id+"F2.imprint","IMPRINT",EDGE,{"derivedFrom":sQuery(id+"F2.wireOp",EDGE,"E279")}),-1.0]])]});
            var Q1;
            Q1=makeQuery(id+"F2.imprint","IMPRINT",FACE,{"disambiguationData":[TD([[makeQuery(id+"F2.imprint","IMPRINT",EDGE,{"derivedFrom":sQuery(id+"F2.wireOp",EDGE,"E683")}),-1.0]])]});
            var Q2;
            Q2=makeQuery(id+"F2.imprint","IMPRINT",FACE,{"disambiguationData":[TD([[makeQuery(id+"F2.imprint","IMPRINT",EDGE,{"derivedFrom":sQuery(id+"F2.wireOp",EDGE,"E633")}),-1.0]])]});
            var Q3;
            Q3=makeQuery(id+"F2.imprint","IMPRINT",FACE,{"disambiguationData":[TD([[makeQuery(id+"F2.imprint","IMPRINT",EDGE,{"derivedFrom":sQuery(id+"F2.wireOp",EDGE,"E938")}),-1.0]])]});
            var Q4;
            Q4=makeQuery(id+"F2.imprint","IMPRINT",FACE,{"disambiguationData":[TD([[makeQuery(id+"F2.imprint","IMPRINT",EDGE,{"derivedFrom":sQuery(id+"F2.wireOp",EDGE,"E968")}),-1.0]])]});
            var Q5;
            Q5=makeQuery(id+"F2.imprint","IMPRINT",FACE,{"disambiguationData":[TD([[makeQuery(id+"F2.imprint","IMPRINT",EDGE,{"derivedFrom":sQuery(id+"F2.wireOp",EDGE,"E492")}),-1.0]])]});
            var Q6;
            Q6=makeQuery(id+"F2.imprint","IMPRINT",FACE,{"disambiguationData":[TD([[makeQuery(id+"F2.imprint","IMPRINT",EDGE,{"derivedFrom":sQuery(id+"F2.wireOp",EDGE,"E460")}),-1.0]])]});
            var Q7;
            Q7=makeQuery(id+"F2.imprint","IMPRINT",FACE,{"disambiguationData":[TD([[makeQuery(id+"F2.imprint","IMPRINT",EDGE,{"derivedFrom":sQuery(id+"F2.wireOp",EDGE,"E554")}),-1.0]])]});
            var Q8;
            Q8=makeQuery(id+"F2.imprint","IMPRINT",FACE,{"disambiguationData":[TD([[makeQuery(id+"F2.imprint","IMPRINT",EDGE,{"derivedFrom":sQuery(id+"F2.wireOp",EDGE,"E705")}),-1.0]])]});
            var Q9;
            Q9=makeQuery(id+"F2.imprint","IMPRINT",FACE,{"disambiguationData":[TD([[makeQuery(id+"F2.imprint","IMPRINT",EDGE,{"derivedFrom":sQuery(id+"F2.wireOp",EDGE,"E789")}),-1.0]])]});
            var Q10;
            Q10=makeQuery(id+"F2.imprint","IMPRINT",FACE,{"disambiguationData":[TD([[makeQuery(id+"F2.imprint","IMPRINT",EDGE,{"derivedFrom":sQuery(id+"F2.wireOp",EDGE,"E836")}),-1.0]])]});
            var Q11;
            Q11=makeQuery(id+"F2.imprint","IMPRINT",FACE,{"disambiguationData":[TD([[makeQuery(id+"F2.imprint","IMPRINT",EDGE,{"derivedFrom":sQuery(id+"F2.wireOp",EDGE,"E886")}),-1.0]])]});
            var Q12;
            Q12=makeQuery(id+"F2.imprint","IMPRINT",FACE,{"disambiguationData":[TD([[makeQuery(id+"F2.imprint","IMPRINT",EDGE,{"derivedFrom":sQuery(id+"F2.wireOp",EDGE,"E996")}),-1.0]])]});
            var Q13;
            Q13=makeQuery(id+"F2.imprint","IMPRINT",FACE,{"disambiguationData":[TD([[makeQuery(id+"F2.imprint","IMPRINT",EDGE,{"derivedFrom":sQuery(id+"F2.wireOp",EDGE,"E898")}),-1.0]])]});
            var Q14;
            Q14=makeQuery(id+"F2.imprint","IMPRINT",FACE,{"disambiguationData":[TD([[makeQuery(id+"F2.imprint","IMPRINT",EDGE,{"derivedFrom":sQuery(id+"F2.wireOp",EDGE,"E848")}),-1.0]])]});
            var Q15;
            Q15=makeQuery(id+"F2.imprint","IMPRINT",FACE,{"disambiguationData":[TD([[makeQuery(id+"F2.imprint","IMPRINT",EDGE,{"derivedFrom":sQuery(id+"F2.wireOp",EDGE,"E811")}),-1.0]])]});
            var Q16;
            Q16=makeQuery(id+"F2.imprint","IMPRINT",FACE,{"disambiguationData":[TD([[makeQuery(id+"F2.imprint","IMPRINT",EDGE,{"derivedFrom":sQuery(id+"F2.wireOp",EDGE,"E757")}),-1.0]])]});
            var Q17;
            Q17=makeQuery(id+"F2.imprint","IMPRINT",FACE,{"disambiguationData":[TD([[makeQuery(id+"F2.imprint","IMPRINT",EDGE,{"derivedFrom":sQuery(id+"F2.wireOp",EDGE,"E1063")}),-1.0]])]});
            var Q18;
            Q18=makeQuery(id+"F2.imprint","IMPRINT",FACE,{"disambiguationData":[TD([[makeQuery(id+"F2.imprint","IMPRINT",EDGE,{"derivedFrom":sQuery(id+"F2.wireOp",EDGE,"E1119")}),-1.0]])]});
            var Q19;
            Q19=makeQuery(id+"F2.imprint","IMPRINT",FACE,{"disambiguationData":[TD([[makeQuery(id+"F2.imprint","IMPRINT",EDGE,{"derivedFrom":sQuery(id+"F2.wireOp",EDGE,"E1163")}),-1.0]])]});
            var Q20;
            Q20=makeQuery(id+"F2.imprint","IMPRINT",FACE,{"disambiguationData":[TD([[makeQuery(id+"F2.imprint","IMPRINT",EDGE,{"derivedFrom":sQuery(id+"F2.wireOp",EDGE,"E1078")}),-1.0]])]});
            var Q21;
            Q21=makeQuery(id+"F2.imprint","IMPRINT",FACE,{"disambiguationData":[TD([[makeQuery(id+"F2.imprint","IMPRINT",EDGE,{"derivedFrom":sQuery(id+"F2.wireOp",EDGE,"E1031")}),-1.0]])]});
            var Q22;
            Q22=makeQuery(id+"F2.imprint","IMPRINT",FACE,{"disambiguationData":[TD([[makeQuery(id+"F2.imprint","IMPRINT",EDGE,{"derivedFrom":sQuery(id+"F2.wireOp",EDGE,"E421")}),-1.0]])]});
            var Q23;
            Q23=makeQuery(id+"F2.imprint","IMPRINT",FACE,{"disambiguationData":[TD([[makeQuery(id+"F2.imprint","IMPRINT",EDGE,{"derivedFrom":sQuery(id+"F2.wireOp",EDGE,"E240")}),-1.0]])]});
            var Q24;
            Q24=makeQuery(id+"F2.imprint","IMPRINT",FACE,{"disambiguationData":[TD([[makeQuery(id+"F2.imprint","IMPRINT",EDGE,{"derivedFrom":sQuery(id+"F2.wireOp",EDGE,"E168")}),-1.0]])]});
            var Q25;
            Q25=makeQuery(id+"F2.imprint","IMPRINT",FACE,{"disambiguationData":[TD([[makeQuery(id+"F2.imprint","IMPRINT",EDGE,{"derivedFrom":sQuery(id+"F2.wireOp",EDGE,"E92")}),-1.0]])]});
            var Q26;
            Q26=makeQuery(id+"F2.imprint","IMPRINT",FACE,{"disambiguationData":[TD([[makeQuery(id+"F2.imprint","IMPRINT",EDGE,{"derivedFrom":sQuery(id+"F2.wireOp",EDGE,"E1")}),-1.0]])]});
            var Q27;
            Q27=makeQuery(id+"F2.imprint","IMPRINT",FACE,{"disambiguationData":[TD([[makeQuery(id+"F2.imprint","IMPRINT",EDGE,{"derivedFrom":sQuery(id+"F2.wireOp",EDGE,"E48")}),-1.0]])]});
            var Q28;
            Q28=makeQuery(id+"F2.imprint","IMPRINT",FACE,{"disambiguationData":[TD([[makeQuery(id+"F2.imprint","IMPRINT",EDGE,{"derivedFrom":sQuery(id+"F2.wireOp",EDGE,"E130")}),-1.0]])]});
            var Q29;
            Q29=makeQuery(id+"F2.imprint","IMPRINT",FACE,{"disambiguationData":[TD([[makeQuery(id+"F2.imprint","IMPRINT",EDGE,{"derivedFrom":sQuery(id+"F2.wireOp",EDGE,"E199")}),-1.0]])]});
            var Q30;
            Q30=makeQuery(id+"F2.imprint","IMPRINT",FACE,{"disambiguationData":[TD([[makeQuery(id+"F2.imprint","IMPRINT",EDGE,{"derivedFrom":sQuery(id+"F2.wireOp",EDGE,"E393")}),-1.0]])]});
            var Q31;
            Q31=makeQuery(id+"F2.imprint","IMPRINT",FACE,{"disambiguationData":[TD([[makeQuery(id+"F2.imprint","IMPRINT",EDGE,{"derivedFrom":sQuery(id+"F2.wireOp",EDGE,"E590")}),-1.0]])]});
            extrude(context, id + "F3", {"entities" : qUnion([Q0, Q1, Q2, Q3, Q4, Q5, Q6, Q7, Q8, Q9, Q10, Q11, Q12, Q13, Q14, Q15, Q16, Q17, Q18, Q19, Q20, Q21, Q22, Q23, Q24, Q25, Q26, Q27, Q28, Q29, Q30, Q31]), "operationType" : NewBodyOperationType.ADD, "depth" : .4 * mm, "offsetDistance" : 25.4 * mm});
        }
    });
